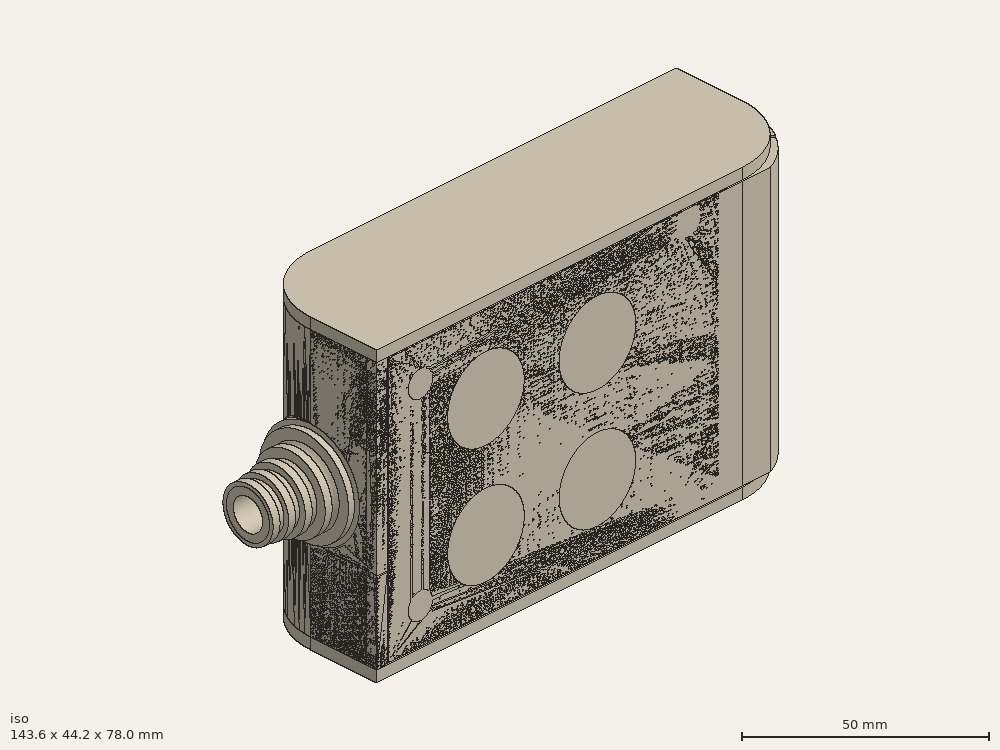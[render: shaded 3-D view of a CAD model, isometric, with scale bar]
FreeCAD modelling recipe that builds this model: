
FCSTD DOCUMENT  (FreeCAD 0.19R0.19.2)
Label: enclosure_157
License: All rights reserved
LicenseURL: http://en.wikipedia.org/wiki/All_rights_reserved
objects: Part::Feature×104, Part::Revolution×104, Part::MultiFuse×91, Sketcher::SketchObject×66, Part::Extrusion×51, Part::Cut×45, Part::Cylinder×42, Part::Fillet×41, Part::Box×27, App::MeasureDistance×4
note: 571 computed .brp shape members not serialized (recipe doc carries the construction recipe); baked Part::Feature solids carry a one-line shape summary decoded from their .brp

FEATURE [Sketcher::SketchObject] Sketch  label="topSketch"
  FullyConstrained = true
  sketch-geometry (20):
    g0: LineSegment StartX=5.21097e-06 StartY=3 StartZ=0 EndX=5.21097e-06 EndY=19 EndZ=0
    g1: ArcOfCircle CenterX=19 CenterY=19 CenterZ=0 NormalX=0 NormalY=0 NormalZ=1 AngleXU=0 Radius=19 StartAngle=1.5708 EndAngle=3.14159
    g2: ArcOfCircle CenterX=19 CenterY=19 CenterZ=0 NormalX=0 NormalY=0 NormalZ=1 AngleXU=0 Radius=16 StartAngle=1.5708 EndAngle=3.14159
    g3: LineSegment StartX=114 StartY=35 StartZ=0 EndX=19 EndY=35 EndZ=0
    g4: LineSegment StartX=5.21097e-06 StartY=3 StartZ=0 EndX=5.21097e-06 EndY=0 EndZ=0
    g5: LineSegment StartX=3 StartY=0 StartZ=0 EndX=5.21097e-06 EndY=0 EndZ=0
    g6: LineSegment StartX=3 StartY=19 StartZ=0 EndX=3 EndY=0 EndZ=0
    g7: LineSegment StartX=19 StartY=38 StartZ=0 EndX=124 EndY=38 EndZ=0
    g8: Circle CenterX=119 CenterY=35 CenterZ=0 NormalX=0 NormalY=0 NormalZ=1 AngleXU=0 Radius=1
    g9: Circle CenterX=121 CenterY=35 CenterZ=0 NormalX=0 NormalY=0 NormalZ=1 AngleXU=0 Radius=1
    g10: Circle CenterX=121 CenterY=33 CenterZ=0 NormalX=0 NormalY=0 NormalZ=1 AngleXU=0 Radius=1
    g11: BSplineCurve PolesCount=3 KnotsCount=2 Degree=2 IsPeriodic=0
    g12: GeomPoint X=119 Y=35 Z=0
    g13: GeomPoint X=121 Y=33 Z=0
    g14: LineSegment StartX=119 StartY=35 StartZ=0 EndX=114 EndY=35 EndZ=0
    g15: ArcOfCircle CenterX=105 CenterY=19 CenterZ=0 NormalX=0 NormalY=0 NormalZ=1 AngleXU=0 Radius=19 StartAngle=5.7297 EndAngle=6.28319
    g16: ArcOfCircle CenterX=105 CenterY=19 CenterZ=0 NormalX=0 NormalY=0 NormalZ=1 AngleXU=0 Radius=16 StartAngle=5.60905 EndAngle=6.28319
    g17: LineSegment StartX=121 StartY=33 StartZ=0 EndX=121 EndY=19 EndZ=0
    g18: LineSegment StartX=124 StartY=38 StartZ=0 EndX=124 EndY=19 EndZ=0
    g19: LineSegment StartX=117.5 StartY=9.01251 StartZ=0 EndX=121.163 EndY=9.0125 EndZ=0
  constraints (46):
    c: Vertical(g0)
    c: Block(g0)
    c: Coincident(g1,g0)
    c: Block(g1)
    c: Coincident(g2,g1)
    c: Block(g2)
    c: Coincident(g3,g2)
    c: Horizontal(g3)
    c: Tangent(g3,g2)
    c: Coincident(g4,g0)
    c: Distance(g4) = 3
    c: Vertical(g4)
    c: Coincident(g5,g4)
    c: Horizontal(g5)
    c: Coincident(g6,g2)
    c: Coincident(g6,g5)
    c: Vertical(g6)
    c: Horizontal(g7)
    c: Distance(g7) = 105
    c: Coincident(g7,g1)
    c: Block(g3)
    c: Weight(g8) = 1
    c: Equal(g8,g9)
    c: Equal(g8,g10)
    c: InternalAlignment(g8,g11)
    c: InternalAlignment(g9,g11)
    c: InternalAlignment(g10,g11)
    c: InternalAlignment(g12,g11)
    c: InternalAlignment(g13,g11)
    c: Block(g11)
    c: Coincident(g14,g11)
    c: Coincident(g14,g3)
    c: Horizontal(g14)
    c: Block(g15)
    c: Coincident(g16,g15)
    c: Block(g16)
    c: Coincident(g17,g11)
    c: Coincident(g17,g16)
    c: Vertical(g17)
    c: Distance(g17) = 14
    c: Coincident(g18,g7)
    c: Coincident(g18,g15)
    c: Vertical(g18)
    c: Distance(g18) = 19
    c: Coincident(g19,g16)
    c: Coincident(g19,g15)
FEATURE [Sketcher::SketchObject] Sketch001  label="bottomSketch"
  FullyConstrained = true
  sketch-geometry (32):
    g0: LineSegment StartX=3.3 StartY=-6.03275e-07 StartZ=0 EndX=98 EndY=-6.03275e-07 EndZ=0
    g1: ArcOfCircle CenterX=98 CenterY=19 CenterZ=0 NormalX=0 NormalY=0 NormalZ=1 AngleXU=0 Radius=19 StartAngle=4.71239 EndAngle=5.71103
    g2: LineSegment StartX=6.3 StartY=8 StartZ=0 EndX=3.3 EndY=8 EndZ=0
    g3: LineSegment StartX=3.3 StartY=8 StartZ=0 EndX=3.3 EndY=-6.03275e-07 EndZ=0
    g4: ArcOfCircle CenterX=8.3 CenterY=5 CenterZ=0 NormalX=0 NormalY=0 NormalZ=1 AngleXU=0 Radius=2 StartAngle=3.14159 EndAngle=4.71239
    g5: LineSegment StartX=6.3 StartY=8 StartZ=0 EndX=6.3 EndY=5 EndZ=0
    g6: ArcOfCircle CenterX=98 CenterY=19 CenterZ=0 NormalX=0 NormalY=0 NormalZ=1 AngleXU=0 Radius=12.7 StartAngle=4.71239 EndAngle=6.28319
    g7: LineSegment StartX=94.7 StartY=3 StartZ=0 EndX=8.3 EndY=3 EndZ=0
    g8-g12: Circle x5 (B-spline internal-alignment scaffolding for g13; pole/knot coordinates omitted)
    g13: BSplineCurve PolesCount=5 KnotsCount=3 Degree=3 IsPeriodic=0
    g14: GeomPoint X=98 Y=6.3 Z=0
    g15: GeomPoint X=96.3938 Y=4.71946 Z=0
    g16: GeomPoint X=94.7 Y=3 Z=0
    g17-g23: Circle x7 (B-spline internal-alignment scaffolding for g24; pole/knot coordinates omitted)
    g24: BSplineCurve PolesCount=7 KnotsCount=5 Degree=3 IsPeriodic=0
    g25-g29: GeomPoint x5 (B-spline internal-alignment scaffolding for g24; pole/knot coordinates omitted)
    g30: ArcOfCircle CenterX=98 CenterY=19 CenterZ=0 NormalX=0 NormalY=0 NormalZ=1 AngleXU=0 Radius=15.7 StartAngle=5.81226 EndAngle=6.28319
    g31: LineSegment StartX=110.7 StartY=19 StartZ=0 EndX=113.7 EndY=19 EndZ=0
  constraints (41):
    c: Horizontal(g0)
    c: Coincident(g1,g0)
    c: Block(g1)
    c: Horizontal(g2)
    c: Distance(g2) = 3
    c: Coincident(g3,g2)
    c: Vertical(g3)
    c: Coincident(g3,g0)
    c: Block(g4)
    c: Block(g2)
    c: Coincident(g5,g2)
    c: Coincident(g5,g4)
    c: Vertical(g5)
    c: Coincident(g6,g1)
    c: Block(g6)
    c: Coincident(g7,g4)
    c: Horizontal(g7)
    c: Block(g0)
    c: Block(g7)
    c: Block(g3)
    c: Coincident(g13,g6)
    c: Weight(g8) = 1
    c: Equal(g8, g9-g12) x4
    c: Coincident(g13,g7)
    c: InternalAlignment(g8-g12 -> g13) x5
    c: InternalAlignment(g14,g13)
    c: InternalAlignment(g15,g13)
    c: InternalAlignment(g16,g13)
    c: Block(g13)
    c: Weight(g17) = 1
    c: Equal(g17, g18-g23) x6
    c: Coincident(g24,g1)
    c: InternalAlignment(g17-g23 -> g24) x7
    c: InternalAlignment(g25-g29 -> g24) x5
    c: Block(g24)
    c: Coincident(g30,g24)
    c: Coincident(g31,g6)
    c: Coincident(g31,g30)
    c: Horizontal(g31)
    c: Block(g31)
    c: Block(g30)
FEATURE [Part::Extrusion] Extrude  label="top"
  Base = -> Sketch
  Dir = (0,0,1)
  DirMode = 2
  FaceMakerClass = Part::FaceMakerBullseye
  LengthFwd = 72
  LengthRev = 0
  Solid = true
  Symmetric = false
FEATURE [Part::Extrusion] Extrude001  label="bottom"
  Base = -> Sketch001
  Dir = (0,0,1)
  DirMode = 2
  FaceMakerClass = Part::FaceMakerBullseye
  LengthFwd = 71.4
  LengthRev = 0
  Placement = pos=(0,0,0.3) rot=(0,0,1;0rad)
  Solid = true
  Symmetric = false
FEATURE [Sketcher::SketchObject] Sketch002  label="topSketch001"
  FullyConstrained = true
  sketch-geometry (6):
    g0: ArcOfCircle CenterX=19 CenterY=19 CenterZ=0 NormalX=0 NormalY=0 NormalZ=1 AngleXU=0 Radius=19 StartAngle=1.5708 EndAngle=3.14159
    g1: LineSegment StartX=5.22862e-06 StartY=19 StartZ=0 EndX=5.22862e-06 EndY=1.19904e-11 EndZ=0
    g2: LineSegment StartX=19 StartY=38 StartZ=0 EndX=124 EndY=38 EndZ=0
    g3: LineSegment StartX=5.22862e-06 StartY=1.19904e-11 StartZ=0 EndX=105 EndY=1.19904e-11 EndZ=0
    g4: ArcOfCircle CenterX=105 CenterY=19 CenterZ=0 NormalX=0 NormalY=0 NormalZ=1 AngleXU=0 Radius=19 StartAngle=4.71239 EndAngle=6.28319
    g5: LineSegment StartX=124 StartY=38 StartZ=0 EndX=124 EndY=19 EndZ=0
  constraints (16):
    c: Block(g0)
    c: Coincident(g1,g0)
    c: Vertical(g1)
    c: Horizontal(g2)
    c: Distance(g2) = 105
    c: Coincident(g2,g0)
    c: Distance(g1) = 19
    c: Coincident(g3,g1)
    c: Horizontal(g3)
    c: Distance(g3) = 105
    c: Block(g4)
    c: Coincident(g4,g3)
    c: Coincident(g5,g2)
    c: Coincident(g5,g4)
    c: Vertical(g5)
    c: Distance(g5) = 19
FEATURE [Part::Extrusion] Extrude002  label="sideA"
  Base = -> Sketch002
  Dir = (0,0,1)
  DirMode = 2
  FaceMakerClass = Part::FaceMakerBullseye
  LengthFwd = 3
  LengthRev = 0
  Placement = pos=(0,0,-3) rot=(0,0,1;0rad)
  Solid = true
  Symmetric = false
FEATURE [Sketcher::SketchObject] Sketch003  label="topSketch002"
  FullyConstrained = true
  sketch-geometry (6):
    g0: LineSegment StartX=19 StartY=38 StartZ=0 EndX=117 EndY=38 EndZ=0
    g1: ArcOfCircle CenterX=19 CenterY=19 CenterZ=0 NormalX=0 NormalY=0 NormalZ=1 AngleXU=0 Radius=19 StartAngle=1.5708 EndAngle=3.14159
    g2: LineSegment StartX=117 StartY=38 StartZ=0 EndX=117 EndY=19 EndZ=0
    g3: LineSegment StartX=98 StartY=1.0161e-12 StartZ=0 EndX=5.22862e-06 EndY=1.0161e-12 EndZ=0
    g4: LineSegment StartX=5.22862e-06 StartY=19 StartZ=0 EndX=5.22862e-06 EndY=1.0161e-12 EndZ=0
    g5: ArcOfCircle CenterX=98 CenterY=19 CenterZ=0 NormalX=0 NormalY=0 NormalZ=1 AngleXU=0 Radius=19 StartAngle=4.71239 EndAngle=6.28319
  constraints (16):
    c: Horizontal(g0)
    c: Distance(g0) = 98
    c: Coincident(g1,g0)
    c: Block(g1)
    c: Coincident(g2,g0)
    c: Vertical(g2)
    c: Distance(g2) = 19
    c: Horizontal(g3)
    c: Coincident(g4,g1)
    c: Vertical(g4)
    c: Coincident(g3,g4)
    c: Block(g3)
    c: Coincident(g5,g2)
    c: Coincident(g5,g3)
    c: Block(g0)
    c: Block(g5)
FEATURE [Sketcher::SketchObject] Sketch004
  FullyConstrained = true
  MapMode = 3
  Placement = pos=(0,0,0) rot=(1,0,0;1.5708rad)
  Support = -> [Extrude]
  sketch-geometry (8):
    g0: Circle CenterX=80.351 CenterY=-67.6202 CenterZ=0 NormalX=0 NormalY=0 NormalZ=1 AngleXU=0 Radius=2
    g1: Circle CenterX=80.351 CenterY=-67.6202 CenterZ=0 NormalX=0 NormalY=0 NormalZ=1 AngleXU=0 Radius=3
    g2: Circle CenterX=80.351 CenterY=-4.92017 CenterZ=0 NormalX=0 NormalY=0 NormalZ=1 AngleXU=0 Radius=2
    g3: Circle CenterX=80.351 CenterY=-4.92017 CenterZ=0 NormalX=0 NormalY=0 NormalZ=1 AngleXU=0 Radius=3
    g4: Circle CenterX=23.851 CenterY=-4.92017 CenterZ=0 NormalX=0 NormalY=0 NormalZ=1 AngleXU=0 Radius=2
    g5: Circle CenterX=23.851 CenterY=-4.92017 CenterZ=0 NormalX=0 NormalY=0 NormalZ=1 AngleXU=0 Radius=3
    g6: Circle CenterX=23.851 CenterY=-67.6202 CenterZ=0 NormalX=0 NormalY=0 NormalZ=1 AngleXU=0 Radius=2
    g7: Circle CenterX=23.851 CenterY=-67.6202 CenterZ=0 NormalX=0 NormalY=0 NormalZ=1 AngleXU=0 Radius=3
  constraints (8):
    c: Block(g3)
    c: Block(g2)
    c: Block(g1)
    c: Block(g0)
    c: Block(g6)
    c: Block(g7)
    c: Block(g4)
    c: Block(g5)
FEATURE [Part::Extrusion] Extrude004
  Base = -> Sketch004
  Dir = (0,-1,2e-16)
  DirMode = 2
  FaceMakerClass = Part::FaceMakerBullseye
  LengthFwd = 6
  LengthRev = 0
  Placement = pos=(0,9,0) rot=(0,0,1;0rad)
  Solid = true
  Symmetric = false
FEATURE [Sketcher::SketchObject] Sketch005
  FullyConstrained = true
  MapMode = 3
  Placement = pos=(0,0,0) rot=(1,0,0;1.5708rad)
  Support = -> [Extrude]
  sketch-geometry (8):
    g0: Circle CenterX=80.351 CenterY=-67.6202 CenterZ=0 NormalX=0 NormalY=0 NormalZ=1 AngleXU=0 Radius=3
    g1: Circle CenterX=80.351 CenterY=-4.92017 CenterZ=0 NormalX=0 NormalY=0 NormalZ=1 AngleXU=0 Radius=3
    g2: Circle CenterX=23.851 CenterY=-4.92017 CenterZ=0 NormalX=0 NormalY=0 NormalZ=1 AngleXU=0 Radius=3
    g3: Circle CenterX=23.851 CenterY=-67.6202 CenterZ=0 NormalX=0 NormalY=0 NormalZ=1 AngleXU=0 Radius=3
    g4: Circle CenterX=23.851 CenterY=-67.6202 CenterZ=0 NormalX=0 NormalY=0 NormalZ=1 AngleXU=0 Radius=5
    g5: Circle CenterX=80.351 CenterY=-67.6202 CenterZ=0 NormalX=0 NormalY=0 NormalZ=1 AngleXU=0 Radius=5
    g6: Circle CenterX=23.851 CenterY=-4.92017 CenterZ=0 NormalX=0 NormalY=0 NormalZ=1 AngleXU=0 Radius=5
    g7: Circle CenterX=80.351 CenterY=-4.92017 CenterZ=0 NormalX=0 NormalY=0 NormalZ=1 AngleXU=0 Radius=5
  constraints (8):
    c: Block(g1)
    c: Block(g0)
    c: Block(g3)
    c: Block(g2)
    c: Block(g5)
    c: Block(g4)
    c: Block(g6)
    c: Block(g7)
FEATURE [Part::Extrusion] Extrude005
  Base = -> Sketch005
  Dir = (0,-1,2e-16)
  DirMode = 2
  FaceMakerClass = Part::FaceMakerBullseye
  LengthFwd = 2
  LengthRev = 0
  Solid = true
  Symmetric = false
FEATURE [Sketcher::SketchObject] Sketch006
  FullyConstrained = true
  MapMode = 3
  Placement = pos=(0,0,0) rot=(1,0,0;1.5708rad)
  sketch-geometry (8):
    g0: Circle CenterX=80.351 CenterY=-67.6202 CenterZ=0 NormalX=0 NormalY=0 NormalZ=1 AngleXU=0 Radius=3
    g1: Circle CenterX=80.351 CenterY=-4.92017 CenterZ=0 NormalX=0 NormalY=0 NormalZ=1 AngleXU=0 Radius=3
    g2: Circle CenterX=23.851 CenterY=-4.92017 CenterZ=0 NormalX=0 NormalY=0 NormalZ=1 AngleXU=0 Radius=3
    g3: Circle CenterX=23.851 CenterY=-67.6202 CenterZ=0 NormalX=0 NormalY=0 NormalZ=1 AngleXU=0 Radius=3
    g4: Circle CenterX=23.851 CenterY=-67.6202 CenterZ=0 NormalX=0 NormalY=0 NormalZ=1 AngleXU=0 Radius=5
    g5: Circle CenterX=80.351 CenterY=-67.6202 CenterZ=0 NormalX=0 NormalY=0 NormalZ=1 AngleXU=0 Radius=5
    g6: Circle CenterX=23.851 CenterY=-4.92017 CenterZ=0 NormalX=0 NormalY=0 NormalZ=1 AngleXU=0 Radius=5
    g7: Circle CenterX=80.351 CenterY=-4.92017 CenterZ=0 NormalX=0 NormalY=0 NormalZ=1 AngleXU=0 Radius=5
  constraints (8):
    c: Block(g1)
    c: Block(g0)
    c: Block(g3)
    c: Block(g2)
    c: Block(g5)
    c: Block(g4)
    c: Block(g6)
    c: Block(g7)
FEATURE [Part::Extrusion] Extrude007
  Base = -> Sketch006
  Dir = (0,-1,2e-16)
  DirMode = 2
  FaceMakerClass = Part::FaceMakerBullseye
  LengthFwd = 2
  LengthRev = 0
  Solid = true
  Symmetric = false
FEATURE [Part::Fillet] Fillet
  Base = -> Extrude007
  Edges = 4 edges r=1.99: [Edge6,Edge12,Edge18,Edge24]
FEATURE [Part::Cut] Cut
  Base = -> Extrude005
  Placement = pos=(0,5,0) rot=(0,0,1;0rad)
  Tool = -> Fillet
FEATURE [Part::MultiFuse] Fusion  label="pCBScrews"
  Placement = pos=(-2.5,0,72.3) rot=(0,0,1;0rad)
  Shapes = -> [Extrude004,Cut]
FEATURE [App::MeasureDistance] Distance  label="Distance: 0.69 mm"
  Distance = 0.685967
  P1 = (24.0138,2.9647,0.3)
  P2 = (23.8901,3,-0.373787)
FEATURE [App::MeasureDistance] Distance001  label="Distance: 0.53 mm"
  Distance = 0.533607
  P1 = (80.2939,3,72.2334)
  P2 = (80.281,2.99661,71.7)
FEATURE [Part::Fillet] Fillet001
  Base = -> Extrude001
  Edges = 1 edges r=2.4: [Edge17]
FEATURE [Part::Fillet] Fillet002  label="bottom001"
  Base = -> Fillet001
  Edges = 1 edges r=2.4: [Edge36]
FEATURE [Part::Fillet] Fillet003  label="top001"
  Base = -> Extrude
  Edges = 1 edges r=2: [Edge1]
FEATURE [Sketcher::SketchObject] Sketch007
  FullyConstrained = true
  sketch-geometry (16):
    g0: LineSegment StartX=4 StartY=0 StartZ=0 EndX=4 EndY=2.4 EndZ=0
    g1: LineSegment StartX=4 StartY=2.4 StartZ=0 EndX=7 EndY=2.4 EndZ=0
    g2: LineSegment StartX=4 StartY=0 StartZ=0 EndX=5.7 EndY=0 EndZ=0
    g3: LineSegment StartX=5.7 StartY=0 StartZ=0 EndX=5.7 EndY=-5.6 EndZ=0
    g4-g8: Circle x5 (B-spline internal-alignment scaffolding for g9; pole/knot coordinates omitted)
    g9: BSplineCurve PolesCount=5 KnotsCount=3 Degree=3 IsPeriodic=0
    g10: GeomPoint X=7 Y=2.4 Z=0
    g11: GeomPoint X=10.4582 Y=-1.55472 Z=0
    g12: GeomPoint X=14 Y=-5.6 Z=0
    g13: LineSegment StartX=14 StartY=-5.6 StartZ=0 EndX=14 EndY=-14.1 EndZ=0
    g14: LineSegment StartX=14 StartY=-14.1 StartZ=0 EndX=6.5 EndY=-14.1 EndZ=0
    g15: LineSegment StartX=5.7 StartY=-5.6 StartZ=0 EndX=6.5 EndY=-14.1 EndZ=0
  constraints (28):
    c: Distance(g0) = 2.4
    c: Vertical(g0)
    c: Block(g0)
    c: Coincident(g1,g0)
    c: Horizontal(g1)
    c: Distance(g1) = 3
    c: Coincident(g2,g0)
    c: Horizontal(g2)
    c: Distance(g2) = 1.7
    c: Coincident(g3,g2)
    c: Vertical(g3)
    c: Distance(g3) = 5.6
    c: Coincident(g9,g1)
    c: Weight(g4) = 1
    c: Equal(g4, g5-g8) x4
    c: InternalAlignment(g4-g8 -> g9) x5
    c: InternalAlignment(g10,g9)
    c: InternalAlignment(g11,g9)
    c: InternalAlignment(g12,g9)
    c: Block(g9)
    c: Coincident(g13,g9)
    c: Vertical(g13)
    c: Distance(g13) = 8.5
    c: Coincident(g14,g13)
    c: Horizontal(g14)
    c: Distance(g14) = 7.5
    c: Coincident(g15,g3)
    c: Coincident(g15,g14)
FEATURE [Part::Feature] Face
  shape: bbox 10 x 16.5 x 2e-07 mm, 1 faces, 0 solids (baked)
FEATURE [Part::Revolution] Revolve  label="plugHousing"
  Angle = 360
  Axis = (0,1,0)
  Base = (0,0,0)
  FaceMakerClass = Part::FaceMakerBullseye
  Placement = pos=(0,0,36.15) rot=(0,0,1;0rad)
  Solid = false
  Source = -> Face
  Symmetric = false
FEATURE [Part::Feature] Face001
  shape: bbox 10 x 16.5 x 2e-07 mm, 1 faces, 0 solids (baked)
FEATURE [Part::Revolution] Revolve001  label="plugHousing001"
  Angle = 360
  Axis = (0,1,0)
  Base = (0,0,0)
  FaceMakerClass = Part::FaceMakerBullseye
  Placement = pos=(0,0,36.15) rot=(0,0,1;0rad)
  Solid = false
  Source = -> Face001
  Symmetric = false
FEATURE [Part::MultiFuse] Fusion001  label="plugHousing002"
  Placement = pos=(0,0,0) rot=(0,0,1;1.5708rad)
  Shapes = -> [Revolve001,Revolve]
FEATURE [Part::Feature] Face002
  shape: bbox 10 x 16.5 x 2e-07 mm, 1 faces, 0 solids (baked)
FEATURE [Part::Revolution] Revolve003  label="plugHousing005"
  Angle = 360
  Axis = (0,1,0)
  Base = (0,0,0)
  FaceMakerClass = Part::FaceMakerBullseye
  Placement = pos=(0,0,36.15) rot=(0,0,1;0rad)
  Solid = false
  Source = -> Face002
  Symmetric = false
FEATURE [Part::Feature] Face003
  shape: bbox 10 x 16.5 x 2e-07 mm, 1 faces, 0 solids (baked)
FEATURE [Part::Revolution] Revolve002  label="plugHousing003"
  Angle = 360
  Axis = (0,1,0)
  Base = (0,0,0)
  FaceMakerClass = Part::FaceMakerBullseye
  Placement = pos=(0,0,36.15) rot=(0,0,1;0rad)
  Solid = false
  Source = -> Face003
  Symmetric = false
FEATURE [Part::MultiFuse] Fusion002  label="plugHousing004"
  Placement = pos=(0,0,0) rot=(0,0,1;1.5708rad)
  Shapes = -> [Revolve002,Revolve003]
FEATURE [Part::MultiFuse] Fusion003  label="plugHousing006"
  Placement = pos=(0,19,0) rot=(0,0,1;3.14159rad)
  Shapes = -> [Fusion002,Fusion001]
FEATURE [Part::Feature] Face004
  shape: bbox 10 x 16.5 x 2e-07 mm, 1 faces, 0 solids (baked)
FEATURE [Part::Revolution] Revolve006  label="plugHousing010"
  Angle = 360
  Axis = (0,1,0)
  Base = (0,0,0)
  FaceMakerClass = Part::FaceMakerBullseye
  Placement = pos=(0,0,36.15) rot=(0,0,1;0rad)
  Solid = false
  Source = -> Face004
  Symmetric = false
FEATURE [Part::Feature] Face005
  shape: bbox 10 x 16.5 x 2e-07 mm, 1 faces, 0 solids (baked)
FEATURE [Part::Revolution] Revolve007  label="plugHousing011"
  Angle = 360
  Axis = (0,1,0)
  Base = (0,0,0)
  FaceMakerClass = Part::FaceMakerBullseye
  Placement = pos=(0,0,36.15) rot=(0,0,1;0rad)
  Solid = false
  Source = -> Face005
  Symmetric = false
FEATURE [Part::Feature] Face006
  shape: bbox 10 x 16.5 x 2e-07 mm, 1 faces, 0 solids (baked)
FEATURE [Part::Revolution] Revolve004  label="plugHousing007"
  Angle = 360
  Axis = (0,1,0)
  Base = (0,0,0)
  FaceMakerClass = Part::FaceMakerBullseye
  Placement = pos=(0,0,36.15) rot=(0,0,1;0rad)
  Solid = false
  Source = -> Face006
  Symmetric = false
FEATURE [Part::MultiFuse] Fusion004  label="plugHousing009"
  Placement = pos=(0,0,0) rot=(0,0,1;1.5708rad)
  Shapes = -> [Revolve004,Revolve007]
FEATURE [Part::Feature] Face007
  shape: bbox 10 x 16.5 x 2e-07 mm, 1 faces, 0 solids (baked)
FEATURE [Part::Revolution] Revolve005  label="plugHousing008"
  Angle = 360
  Axis = (0,1,0)
  Base = (0,0,0)
  FaceMakerClass = Part::FaceMakerBullseye
  Placement = pos=(0,0,36.15) rot=(0,0,1;0rad)
  Solid = false
  Source = -> Face007
  Symmetric = false
FEATURE [Part::MultiFuse] Fusion005  label="plugHousing012"
  Placement = pos=(0,0,0) rot=(0,0,1;1.5708rad)
  Shapes = -> [Revolve006,Revolve005]
FEATURE [Part::MultiFuse] Fusion006  label="plugHousing013"
  Placement = pos=(0,19,0) rot=(0,0,1;3.14159rad)
  Shapes = -> [Fusion005,Fusion004]
FEATURE [Part::MultiFuse] Fusion007  label="plugHousing014"
  Placement = pos=(122.621,0,-0.15) rot=(0,0,1;0rad)
  Shapes = -> [Fusion003,Fusion006]
FEATURE [Part::Cylinder] Cylinder002
  Angle = 360
  AttacherType = Attacher::AttachEngine3D
  Height = 20
  Placement = pos=(0,0,36.15) rot=(0,0,1;0rad)
  Radius = 4
FEATURE [Part::Cylinder] Cylinder003
  Angle = 360
  AttacherType = Attacher::AttachEngine3D
  Height = 10
  Placement = pos=(0,0,36.15) rot=(0,0,1;0rad)
  Radius = 4
FEATURE [Part::MultiFuse] Fusion009  label="removeToCreateHoleForPlugHousing"
  Placement = pos=(70,19,36.15) rot=(0,1,0;1.5708rad)
  Shapes = -> [Cylinder002,Cylinder003]
FEATURE [Part::Cylinder] Cylinder004
  Angle = 360
  AttacherType = Attacher::AttachEngine3D
  Height = 20
  Placement = pos=(0,0,36.15) rot=(0,0,1;0rad)
  Radius = 4
FEATURE [Part::Cylinder] Cylinder005
  Angle = 360
  AttacherType = Attacher::AttachEngine3D
  Height = 10
  Placement = pos=(0,0,36.15) rot=(0,0,1;0rad)
  Radius = 4
FEATURE [Part::MultiFuse] Fusion010  label="removeToCreateHoleForPlugHousing001"
  Placement = pos=(70,19,36.15) rot=(0,1,0;1.5708rad)
  Shapes = -> [Cylinder004,Cylinder005]
FEATURE [Part::Cut] Cut001
  Base = -> Fillet003
  Tool = -> Fusion010
FEATURE [Part::Cut] Cut002  label="Bottom"
  Base = -> Fillet002
  Tool = -> Fusion009
FEATURE [Part::Feature] Face008
  shape: bbox 10 x 16.5 x 2e-07 mm, 1 faces, 0 solids (baked)
FEATURE [Part::Revolution] Revolve011  label="plugHousing021"
  Angle = 360
  Axis = (0,1,0)
  Base = (0,0,0)
  FaceMakerClass = Part::FaceMakerBullseye
  Placement = pos=(0,0,36.15) rot=(0,0,1;0rad)
  Solid = false
  Source = -> Face008
  Symmetric = false
FEATURE [Part::Feature] Face009
  shape: bbox 10 x 16.5 x 2e-07 mm, 1 faces, 0 solids (baked)
FEATURE [Part::Revolution] Revolve012  label="plugHousing022"
  Angle = 360
  Axis = (0,1,0)
  Base = (0,0,0)
  FaceMakerClass = Part::FaceMakerBullseye
  Placement = pos=(0,0,36.15) rot=(0,0,1;0rad)
  Solid = false
  Source = -> Face009
  Symmetric = false
FEATURE [Part::Feature] Face010 .. Face013  x4 (patterned run collapsed; names and placements below)
  shape: bbox 10 x 16.5 x 2e-07 mm, 1 faces, 0 solids (baked)
FEATURE [Part::Revolution] Revolve015  label="plugHousing027"
  Angle = 360
  Axis = (0,1,0)
  Base = (0,0,0)
  FaceMakerClass = Part::FaceMakerBullseye
  Placement = pos=(0,0,36.15) rot=(0,0,1;0rad)
  Solid = false
  Source = -> Face013
  Symmetric = false
FEATURE [Part::Feature] Face014
  shape: bbox 10 x 16.5 x 2e-07 mm, 1 faces, 0 solids (baked)
FEATURE [Part::Feature] Face015
  shape: bbox 10 x 16.5 x 2e-07 mm, 1 faces, 0 solids (baked)
FEATURE [Part::Feature] Face016
  shape: bbox 10 x 16.5 x 2e-07 mm, 1 faces, 0 solids (baked)
FEATURE [Part::Revolution] Revolve019  label="plugHousing033"
  Angle = 360
  Axis = (0,1,0)
  Base = (0,0,0)
  FaceMakerClass = Part::FaceMakerBullseye
  Placement = pos=(0,0,36.15) rot=(0,0,1;0rad)
  Solid = false
  Source = -> Face016
  Symmetric = false
FEATURE [Part::Feature] Face017
  shape: bbox 10 x 16.5 x 2e-07 mm, 1 faces, 0 solids (baked)
FEATURE [Part::Revolution] Revolve020  label="plugHousing034"
  Angle = 360
  Axis = (0,1,0)
  Base = (0,0,0)
  FaceMakerClass = Part::FaceMakerBullseye
  Placement = pos=(0,0,36.15) rot=(0,0,1;0rad)
  Solid = false
  Source = -> Face017
  Symmetric = false
FEATURE [Part::Feature] Face018
  shape: bbox 10 x 16.5 x 2e-07 mm, 1 faces, 0 solids (baked)
FEATURE [Part::Revolution] Revolve016  label="plugHousing030"
  Angle = 360
  Axis = (0,1,0)
  Base = (0,0,0)
  FaceMakerClass = Part::FaceMakerBullseye
  Placement = pos=(0,0,36.15) rot=(0,0,1;0rad)
  Solid = false
  Source = -> Face018
  Symmetric = false
FEATURE [Part::MultiFuse] Fusion020  label="plugHousing038"
  Placement = pos=(0,0,0) rot=(0,0,1;1.5708rad)
  Shapes = -> [Revolve016,Revolve020]
FEATURE [Part::Feature] Face019
  shape: bbox 10 x 16.5 x 2e-07 mm, 1 faces, 0 solids (baked)
FEATURE [Part::Feature] Face020
  shape: bbox 10 x 16.5 x 2e-07 mm, 1 faces, 0 solids (baked)
FEATURE [Part::Revolution] Revolve017  label="plugHousing031"
  Angle = 360
  Axis = (0,1,0)
  Base = (0,0,0)
  FaceMakerClass = Part::FaceMakerBullseye
  Placement = pos=(0,0,36.15) rot=(0,0,1;0rad)
  Solid = false
  Source = -> Face020
  Symmetric = false
FEATURE [Part::MultiFuse] Fusion021  label="plugHousing039"
  Placement = pos=(0,0,0) rot=(0,0,1;1.5708rad)
  Shapes = -> [Revolve019,Revolve017]
FEATURE [Part::MultiFuse] Fusion023  label="plugHousing041"
  Placement = pos=(0,19,0) rot=(0,0,1;3.14159rad)
  Shapes = -> [Fusion021,Fusion020]
FEATURE [Part::Revolution] Revolve022  label="plugHousing043"
  Angle = 360
  Axis = (0,1,0)
  Base = (0,0,0)
  FaceMakerClass = Part::FaceMakerBullseye
  Placement = pos=(0,0,36.15) rot=(0,0,1;0rad)
  Solid = false
  Source = -> Face019
  Symmetric = false
FEATURE [Part::Feature] Face021
  shape: bbox 10 x 16.5 x 2e-07 mm, 1 faces, 0 solids (baked)
FEATURE [Part::Revolution] Revolve023  label="plugHousing044"
  Angle = 360
  Axis = (0,1,0)
  Base = (0,0,0)
  FaceMakerClass = Part::FaceMakerBullseye
  Placement = pos=(0,0,36.15) rot=(0,0,1;0rad)
  Solid = false
  Source = -> Face021
  Symmetric = false
FEATURE [Part::Feature] Face022
  shape: bbox 10 x 16.5 x 2e-07 mm, 1 faces, 0 solids (baked)
FEATURE [Part::Revolution] Revolve018  label="plugHousing032"
  Angle = 360
  Axis = (0,1,0)
  Base = (0,0,0)
  FaceMakerClass = Part::FaceMakerBullseye
  Placement = pos=(0,0,36.15) rot=(0,0,1;0rad)
  Solid = false
  Source = -> Face022
  Symmetric = false
FEATURE [Part::MultiFuse] Fusion022  label="plugHousing040"
  Placement = pos=(0,0,0) rot=(0,0,1;1.5708rad)
  Shapes = -> [Revolve018,Revolve023]
FEATURE [Part::Feature] Face023
  shape: bbox 10 x 16.5 x 2e-07 mm, 1 faces, 0 solids (baked)
FEATURE [Part::Revolution] Revolve021  label="plugHousing035"
  Angle = 360
  Axis = (0,1,0)
  Base = (0,0,0)
  FaceMakerClass = Part::FaceMakerBullseye
  Placement = pos=(0,0,36.15) rot=(0,0,1;0rad)
  Solid = false
  Source = -> Face023
  Symmetric = false
FEATURE [Part::MultiFuse] Fusion018  label="plugHousing036"
  Placement = pos=(0,0,0) rot=(0,0,1;1.5708rad)
  Shapes = -> [Revolve022,Revolve021]
FEATURE [Part::MultiFuse] Fusion019  label="plugHousing037"
  Placement = pos=(0,19,0) rot=(0,0,1;3.14159rad)
  Shapes = -> [Fusion018,Fusion022]
FEATURE [Part::MultiFuse] Fusion024  label="plugHousing042"
  Placement = pos=(122.621,0,-0.15) rot=(0,0,1;0rad)
  Shapes = -> [Fusion023,Fusion019]
FEATURE [Part::Cylinder] Cylinder006
  Angle = 360
  AttacherType = Attacher::AttachEngine3D
  Height = 20
  Placement = pos=(0,0,36.15) rot=(0,0,1;0rad)
  Radius = 14.3
FEATURE [Part::Cylinder] Cylinder007
  Angle = 360
  AttacherType = Attacher::AttachEngine3D
  Height = 10
  Placement = pos=(0,0,36.15) rot=(0,0,1;0rad)
  Radius = 4
FEATURE [Part::MultiFuse] Fusion026  label="removeToCreteHoleForPlugHousing"
  Placement = pos=(70,19,36) rot=(0,1,0;1.5708rad)
  Shapes = -> [Cylinder006,Cylinder007]
FEATURE [Part::Box] Box001  label="Cube001"
  AttacherType = Attacher::AttachEngine3D
  Height = 28
  Length = 3
  Placement = pos=(110.7,19,22) rot=(0,0,1;0rad)
  Width = 15.7
FEATURE [Part::Cut] Cut003  label="top002"
  Base = -> Cut001
  Tool = -> Fusion007
FEATURE [Part::Revolution] Revolve008  label="plugHousing015"
  Angle = 360
  Axis = (0,1,0)
  Base = (0,0,0)
  FaceMakerClass = Part::FaceMakerBullseye
  Placement = pos=(0,0,36.15) rot=(0,0,1;0rad)
  Solid = false
  Source = -> Face010
  Symmetric = false
FEATURE [Part::MultiFuse] Fusion013  label="plugHousing020"
  Placement = pos=(0,0,0) rot=(0,0,1;1.5708rad)
  Shapes = -> [Revolve008,Revolve012]
FEATURE [Part::Cut] Cut004  label="top003"
  Base = -> Cut003
  Placement = pos=(1,0,0) rot=(0,0,1;0rad)
  Tool = -> Fusion026
FEATURE [Part::Cylinder] Cylinder008
  Angle = 360
  AttacherType = Attacher::AttachEngine3D
  Height = 20
  Placement = pos=(0,0,36.15) rot=(0,0,1;0rad)
  Radius = 10.3
FEATURE [Part::Cylinder] Cylinder009
  Angle = 360
  AttacherType = Attacher::AttachEngine3D
  Height = 10
  Placement = pos=(0,0,36.15) rot=(0,0,1;0rad)
  Radius = 4
FEATURE [Part::MultiFuse] Fusion027  label="removeToCreteHoleForPlugHousing001"
  Placement = pos=(70,19,36) rot=(0,1,0;1.5708rad)
  Shapes = -> [Cylinder008,Cylinder009]
FEATURE [Part::Cut] Cut005  label="plugHousingTab"
  Base = -> Box001
  Tool = -> Fusion027
FEATURE [Part::MultiFuse] Fusion028  label="plugHousing045"
  Shapes = -> [Fusion024,Cut005]
FEATURE [Part::Box] Box002  label="Cube002"
  AttacherType = Attacher::AttachEngine3D
  Height = 28.8
  Length = 3
  Placement = pos=(107.3,28,21.6) rot=(0,0,1;0rad)
  Width = 7
FEATURE [Part::Box] Box003  label="Cube003"
  AttacherType = Attacher::AttachEngine3D
  Height = 3
  Length = 6.4
  Placement = pos=(107.3,28,18.6) rot=(0,0,1;0rad)
  Width = 7
FEATURE [Part::Box] Box004  label="Cube004"
  AttacherType = Attacher::AttachEngine3D
  Height = 3
  Length = 6.4
  Placement = pos=(107.3,28,50.4) rot=(0,0,1;0rad)
  Width = 7
FEATURE [Part::MultiFuse] Fusion029  label="plugHousingBracketHolder"
  Shapes = -> [Box004,Box002,Box003]
FEATURE [Part::Cylinder] Cylinder010
  Angle = 360
  AttacherType = Attacher::AttachEngine3D
  Height = 20
  Placement = pos=(0,0,36.15) rot=(0,0,1;0rad)
  Radius = 14.3
FEATURE [Part::Cylinder] Cylinder011
  Angle = 360
  AttacherType = Attacher::AttachEngine3D
  Height = 10
  Placement = pos=(0,0,36.15) rot=(0,0,1;0rad)
  Radius = 4
FEATURE [Part::MultiFuse] Fusion030  label="removeToCreteHoleForPlugHousing002"
  Placement = pos=(70,19,36) rot=(0,1,0;1.5708rad)
  Shapes = -> [Cylinder010,Cylinder011]
FEATURE [Part::Cut] Cut006  label="plugHousingBracketHolder001"
  Base = -> Fusion029
  Tool = -> Fusion030
FEATURE [Part::Cylinder] Cylinder012
  Angle = 360
  AttacherType = Attacher::AttachEngine3D
  Height = 20
  Placement = pos=(0,0,36.15) rot=(0,0,1;0rad)
  Radius = 7
FEATURE [Part::Cylinder] Cylinder013
  Angle = 360
  AttacherType = Attacher::AttachEngine3D
  Height = 10
  Placement = pos=(0,0,36.15) rot=(0,0,1;0rad)
  Radius = 4
FEATURE [Part::MultiFuse] Fusion032  label="removeToCreteHoleForPlugHousing003"
  Placement = pos=(70,19,36) rot=(0,1,0;1.5708rad)
  Shapes = -> [Cylinder012,Cylinder013]
FEATURE [Part::Cut] Cut007  label="bottom002"
  Base = -> Cut002
  Tool = -> Fusion032
FEATURE [Sketcher::SketchObject] Sketch008
  FullyConstrained = true
  sketch-geometry (54):
    g0: LineSegment StartX=-4.2 StartY=0 StartZ=0 EndX=-6.2 EndY=0 EndZ=0
    g1: LineSegment StartX=-14 StartY=-18 StartZ=0 EndX=-14 EndY=-26.5 EndZ=0
    g2: LineSegment StartX=-4.2 StartY=0 StartZ=0 EndX=-4.2 EndY=-13.4877 EndZ=0
    g3: Circle CenterX=-4.2 CenterY=-13.4877 CenterZ=0 NormalX=0 NormalY=0 NormalZ=1 AngleXU=0 Radius=1
    g4: Circle CenterX=-4.2 CenterY=-26.5 CenterZ=0 NormalX=0 NormalY=0 NormalZ=1 AngleXU=0 Radius=1
    g5: Circle CenterX=-8.2 CenterY=-26.5 CenterZ=0 NormalX=0 NormalY=0 NormalZ=1 AngleXU=0 Radius=1
    g6: BSplineCurve PolesCount=3 KnotsCount=2 Degree=2 IsPeriodic=0
    g7: GeomPoint X=-4.2 Y=-13.4877 Z=0
    g8: GeomPoint X=-8.2 Y=-26.5 Z=0
    g9: LineSegment StartX=-14 StartY=-26.5 StartZ=0 EndX=-8.2 EndY=-26.5 EndZ=0
    g10: LineSegment StartX=-10.15 StartY=-12 StartZ=0 EndX=-10.15 EndY=-14 EndZ=0
    g11: LineSegment StartX=-12.8401 StartY=-16 StartZ=0 EndX=-10.1571 EndY=-16 EndZ=0
    g12: LineSegment StartX=-10.15 StartY=-14 StartZ=0 EndX=-8.70761 EndY=-14 EndZ=0
    g13: LineSegment StartX=-12.8401 StartY=-16 StartZ=0 EndX=-12.8401 EndY=-17.6958 EndZ=0
    g14: LineSegment StartX=-10.15 StartY=-12 StartZ=0 EndX=-7.79258 EndY=-12 EndZ=0
    g15: Circle CenterX=-6.2215 CenterY=-2 CenterZ=0 NormalX=0 NormalY=0 NormalZ=1 AngleXU=0 Radius=1
    g16: Circle CenterX=-6.22762 CenterY=-2.58724 CenterZ=0 NormalX=0 NormalY=0 NormalZ=1 AngleXU=0 Radius=1
    g17: Circle CenterX=-6.32538 CenterY=-4 CenterZ=0 NormalX=0 NormalY=0 NormalZ=1 AngleXU=0 Radius=1
    g18: BSplineCurve PolesCount=3 KnotsCount=2 Degree=2 IsPeriodic=0
    g19: GeomPoint X=-6.2215 Y=-2 Z=0
    g20: GeomPoint X=-6.32538 Y=-4 Z=0
    g21: Circle CenterX=-6.48644 CenterY=-5.99526 CenterZ=0 NormalX=0 NormalY=0 NormalZ=1 AngleXU=0 Radius=1
    g22: Circle CenterX=-6.58486 CenterY=-6.99526 CenterZ=0 NormalX=0 NormalY=0 NormalZ=1 AngleXU=0 Radius=1
    g23: Circle CenterX=-6.77343 CenterY=-8 CenterZ=0 NormalX=0 NormalY=0 NormalZ=1 AngleXU=0 Radius=1
    g24: BSplineCurve PolesCount=3 KnotsCount=2 Degree=2 IsPeriodic=0
    g25: GeomPoint X=-6.48644 Y=-5.99526 Z=0
    g26: GeomPoint X=-6.77343 Y=-8 Z=0
    g27: Circle CenterX=-7.19003 CenterY=-10 CenterZ=0 NormalX=0 NormalY=0 NormalZ=1 AngleXU=0 Radius=1
    g28: Circle CenterX=-7.44407 CenterY=-11.0915 CenterZ=0 NormalX=0 NormalY=0 NormalZ=1 AngleXU=0 Radius=1
    g29: Circle CenterX=-7.79258 CenterY=-12 CenterZ=0 NormalX=0 NormalY=0 NormalZ=1 AngleXU=0 Radius=1
    g30: BSplineCurve PolesCount=3 KnotsCount=2 Degree=2 IsPeriodic=0
    g31: GeomPoint X=-7.19003 Y=-10 Z=0
    g32: GeomPoint X=-7.79258 Y=-12 Z=0
    g33: Circle CenterX=-8.70761 CenterY=-14 CenterZ=0 NormalX=0 NormalY=0 NormalZ=1 AngleXU=0 Radius=1
    g34: Circle CenterX=-9.33087 CenterY=-15.1837 CenterZ=0 NormalX=0 NormalY=0 NormalZ=1 AngleXU=0 Radius=1
    g35: Circle CenterX=-10.1571 CenterY=-16 CenterZ=0 NormalX=0 NormalY=0 NormalZ=1 AngleXU=0 Radius=1
    g36: BSplineCurve PolesCount=3 KnotsCount=2 Degree=2 IsPeriodic=0
    g37: GeomPoint X=-8.70761 Y=-14 Z=0
    g38: GeomPoint X=-10.1571 Y=-16 Z=0
    g39: Circle CenterX=-12.8401 CenterY=-17.6958 CenterZ=0 NormalX=0 NormalY=0 NormalZ=1 AngleXU=0 Radius=1
    g40: Circle CenterX=-13.3521 CenterY=-17.9027 CenterZ=0 NormalX=0 NormalY=0 NormalZ=1 AngleXU=0 Radius=1
    g41: Circle CenterX=-14 CenterY=-18 CenterZ=0 NormalX=0 NormalY=0 NormalZ=1 AngleXU=0 Radius=1
    g42: BSplineCurve PolesCount=3 KnotsCount=2 Degree=2 IsPeriodic=0
    g43: GeomPoint X=-12.8401 Y=-17.6958 Z=0
    g44: GeomPoint X=-14 Y=-18 Z=0
    g45: LineSegment StartX=-6.2 StartY=0 StartZ=0 EndX=-7.2 EndY=0 EndZ=0
    g46: LineSegment StartX=-7.2 StartY=0 StartZ=0 EndX=-7.2 EndY=-2 EndZ=0
    g47: LineSegment StartX=-7.2 StartY=-2 StartZ=0 EndX=-6.2215 EndY=-2 EndZ=0
    g48: LineSegment StartX=-6.32538 StartY=-4 StartZ=0 EndX=-7.65538 EndY=-4 EndZ=0
    g49: LineSegment StartX=-7.65538 StartY=-4 StartZ=0 EndX=-7.65538 EndY=-5.99526 EndZ=0
    g50: LineSegment StartX=-7.65538 StartY=-5.99526 StartZ=0 EndX=-6.48644 EndY=-5.99526 EndZ=0
    g51: LineSegment StartX=-6.77343 StartY=-8 StartZ=0 EndX=-8.43343 EndY=-8 EndZ=0
    g52: LineSegment StartX=-8.43343 StartY=-8 StartZ=0 EndX=-8.43343 EndY=-10 EndZ=0
    g53: LineSegment StartX=-8.43343 StartY=-10 StartZ=0 EndX=-7.19003 EndY=-10 EndZ=0
  constraints (112):
    c: Horizontal(g0)
    c: Distance(g0) = 2
    c: Block(g0)
    c: Vertical(g1)
    c: Coincident(g2,g0)
    c: Vertical(g2)
    c: Block(g2)
    c: Coincident(g6,g2)
    c: Weight(g3) = 1
    c: Equal(g3,g4)
    c: Equal(g3,g5)
    c: InternalAlignment(g3,g6)
    c: InternalAlignment(g4,g6)
    c: InternalAlignment(g5,g6)
    c: InternalAlignment(g7,g6)
    c: InternalAlignment(g8,g6)
    c: Block(g6)
    c: Coincident(g9,g1)
    c: Coincident(g9,g6)
    c: Horizontal(g9)
    c: Vertical(g10)
    c: Block(g10)
    c: Horizontal(g11)
    c: Block(g11)
    c: Coincident(g12,g10)
    c: Horizontal(g12)
    c: Block(g12)
    c: Coincident(g13,g11)
    c: Vertical(g13)
    c: Block(g13)
    c: Coincident(g14,g10)
    c: Horizontal(g14)
    c: Block(g14)
    c: Block(g9)
    c: Block(g1)
    c: Weight(g15) = 1
    c: Equal(g15,g16)
    c: Equal(g15,g17)
    c: InternalAlignment(g15,g18)
    c: InternalAlignment(g16,g18)
    c: InternalAlignment(g17,g18)
    c: InternalAlignment(g19,g18)
    c: InternalAlignment(g20,g18)
    c: Weight(g21) = 1
    c: Equal(g21,g22)
    c: Equal(g21,g23)
    c: InternalAlignment(g21,g24)
    c: InternalAlignment(g22,g24)
    c: InternalAlignment(g23,g24)
    c: InternalAlignment(g25,g24)
    c: InternalAlignment(g26,g24)
    c: Weight(g27) = 1
    c: Equal(g27,g28)
    c: Equal(g27,g29)
    c: Coincident(g30,g14)
    c: InternalAlignment(g27,g30)
    c: InternalAlignment(g28,g30)
    c: InternalAlignment(g29,g30)
    c: InternalAlignment(g31,g30)
    c: InternalAlignment(g32,g30)
    c: Coincident(g36,g12)
    c: Weight(g33) = 1
    c: Equal(g33,g34)
    c: Equal(g33,g35)
    c: Coincident(g36,g11)
    c: InternalAlignment(g33,g36)
    c: InternalAlignment(g34,g36)
    c: InternalAlignment(g35,g36)
    c: InternalAlignment(g37,g36)
    c: InternalAlignment(g38,g36)
    c: Coincident(g42,g13)
    c: Weight(g39) = 1
    c: Equal(g39,g40)
    c: Equal(g39,g41)
    c: Coincident(g42,g1)
    c: InternalAlignment(g39,g42)
    c: InternalAlignment(g40,g42)
    c: InternalAlignment(g41,g42)
    c: InternalAlignment(g43,g42)
    c: InternalAlignment(g44,g42)
    c: Block(g18)
    c: Block(g24)
    c: Block(g30)
    c: Block(g36)
    c: Block(g42)
    c: Horizontal(g45)
    c: Coincident(g45,g0)
    c: Vertical(g46)
    c: Coincident(g46,g45)
    c: Coincident(g47,g46)
    c: Coincident(g47,g18)
    c: Horizontal(g47)
    c: Block(g46)
    c: Coincident(g48,g18)
    c: Horizontal(g48)
    c: Distance(g48) = 1.33
    c: Vertical(g49)
    c: Coincident(g49,g48)
    c: Coincident(g50,g49)
    c: Coincident(g50,g24)
    c: Horizontal(g50)
    c: Tangent(g50,g22)
    c: Horizontal(g51)
    c: Coincident(g51,g24)
    c: Block(g51)
    c: Vertical(g52)
    c: Block(g52)
    c: Coincident(g52,g51)
    c: Coincident(g53,g52)
    c: Coincident(g53,g30)
    c: Horizontal(g53)
    c: Distance(g1) = 8.5
FEATURE [Part::Feature] Face024
  shape: bbox 9.8 x 26.5 x 2e-07 mm, 1 faces, 0 solids (baked)
FEATURE [Part::Revolution] Revolve024
  Angle = 360
  Axis = (0,1,0)
  Base = (0,0,0)
  FaceMakerClass = Part::FaceMakerBullseye
  Placement = pos=(0,0,0) rot=(0,0,1;1.5708rad)
  Solid = false
  Source = -> Face024
  Symmetric = false
FEATURE [Part::Feature] Face025
  shape: bbox 9.8 x 26.5 x 2e-07 mm, 1 faces, 0 solids (baked)
FEATURE [Part::Revolution] Revolve025
  Angle = 360
  Axis = (0,1,0)
  Base = (0,0,0)
  FaceMakerClass = Part::FaceMakerBullseye
  Placement = pos=(0,0,0) rot=(0,0,1;1.5708rad)
  Solid = false
  Source = -> Face025
  Symmetric = false
FEATURE [Part::MultiFuse] Fusion033
  Placement = pos=(-18,19,36) rot=(0,0,1;0rad)
  Shapes = -> [Revolve025,Revolve024]
FEATURE [Part::Cylinder] Cylinder014
  Angle = 360
  AttacherType = Attacher::AttachEngine3D
  Height = 20
  Placement = pos=(0,0,36.15) rot=(0,0,1;0rad)
  Radius = 14.3
FEATURE [Part::Cylinder] Cylinder015
  Angle = 360
  AttacherType = Attacher::AttachEngine3D
  Height = 10
  Placement = pos=(0,0,36.15) rot=(0,0,1;0rad)
  Radius = 4
FEATURE [Part::MultiFuse] Fusion034  label="removeToCreteHoleForPlugHousing004"
  Placement = pos=(-42,19,36) rot=(0,1,0;1.5708rad)
  Shapes = -> [Cylinder014,Cylinder015]
FEATURE [Part::Cut] Cut008  label="top004"
  Base = -> Cut004
  Placement = pos=(-1,0,0) rot=(0,0,1;0rad)
  Tool = -> Fusion034
FEATURE [Part::Box] Box005  label="Cube005"
  AttacherType = Attacher::AttachEngine3D
  Height = 28
  Length = 3
  Placement = pos=(110.7,19,22) rot=(0,0,1;0rad)
  Width = 15.7
FEATURE [Part::Cylinder] Cylinder016
  Angle = 360
  AttacherType = Attacher::AttachEngine3D
  Height = 10
  Placement = pos=(0,0,36.15) rot=(0,0,1;0rad)
  Radius = 4
FEATURE [Part::Cylinder] Cylinder017
  Angle = 360
  AttacherType = Attacher::AttachEngine3D
  Height = 20
  Placement = pos=(0,0,36.15) rot=(0,0,1;0rad)
  Radius = 10.3
FEATURE [Part::MultiFuse] Fusion035  label="removeToCreteHoleForPlugHousing005"
  Placement = pos=(70,19,36) rot=(0,1,0;1.5708rad)
  Shapes = -> [Cylinder017,Cylinder016]
FEATURE [Part::Cut] Cut009  label="plugHousingTab001"
  Base = -> Box005
  Placement = pos=(-107.4,-14,0) rot=(0,0,1;0rad)
  Tool = -> Fusion035
FEATURE [Part::Box] Box006  label="Cube006"
  AttacherType = Attacher::AttachEngine3D
  Height = 28
  Length = 3
  Placement = pos=(110.7,19,22) rot=(0,0,1;0rad)
  Width = 15.7
FEATURE [Part::Cylinder] Cylinder018
  Angle = 360
  AttacherType = Attacher::AttachEngine3D
  Height = 10
  Placement = pos=(0,0,36.15) rot=(0,0,1;0rad)
  Radius = 4
FEATURE [Part::Cylinder] Cylinder019
  Angle = 360
  AttacherType = Attacher::AttachEngine3D
  Height = 20
  Placement = pos=(0,0,36.15) rot=(0,0,1;0rad)
  Radius = 10.3
FEATURE [Part::MultiFuse] Fusion036  label="removeToCreteHoleForPlugHousing006"
  Placement = pos=(70,19,36) rot=(0,1,0;1.5708rad)
  Shapes = -> [Cylinder019,Cylinder018]
FEATURE [Part::Cut] Cut010  label="plugHousingTab002"
  Base = -> Box006
  Placement = pos=(-107.4,-14,0) rot=(0,0,1;0rad)
  Tool = -> Fusion036
FEATURE [Part::MultiFuse] Fusion037
  Placement = pos=(9.6,23,0) rot=(0,0,1;3.14159rad)
  Shapes = -> [Cut009,Cut010]
FEATURE [Part::Box] Box  label="Cube"
  AttacherType = Attacher::AttachEngine3D
  Height = 10
  Length = 3
  Placement = pos=(3.3,4,12) rot=(0,0,1;0rad)
  Width = 10
FEATURE [Part::Fillet] Fillet004
  Base = -> Fusion028
  Edges = 1 edges r=2: [Edge25]
FEATURE [Part::Fillet] Fillet005  label="plugHousing046"
  Base = -> Fillet004
  Edges = 1 edges r=2: [Edge8]
FEATURE [Part::Fillet] Fillet006
  Base = -> Box
  Edges = 1 edges r=2: [Edge11]
FEATURE [Part::Box] Box007  label="Cube007"
  AttacherType = Attacher::AttachEngine3D
  Height = 10
  Length = 3
  Placement = pos=(3.3,4,50) rot=(0,0,1;0rad)
  Width = 10
FEATURE [Part::Fillet] Fillet007
  Base = -> Box007
  Edges = 1 edges r=2: [Edge12]
FEATURE [Part::Box] Box008  label="Cube008"
  AttacherType = Attacher::AttachEngine3D
  Height = 28
  Length = 4
  Placement = pos=(5,0,22) rot=(0,0,1;0rad)
  Width = 10
FEATURE [Part::Fillet] Fillet008
  Base = -> Box008
  Edges = 1 edges r=1: [Edge7]
FEATURE [Part::Fillet] Fillet009
  Base = -> Fillet008
  Edges = 1 edges r=2: [Edge5]
FEATURE [Part::Fillet] Fillet010
  Base = -> Fillet009
  Edges = 1 edges r=2: [Edge2]
FEATURE [Sketcher::SketchObject] Sketch009  label="topSketch003"
  FullyConstrained = true
  sketch-geometry (4):
    g0: LineSegment StartX=16.8446 StartY=31.512 StartZ=0 EndX=16.3251 EndY=34.4666 EndZ=0
    g1: ArcOfCircle CenterX=19 CenterY=19.2524 CenterZ=0 NormalX=0 NormalY=0 NormalZ=1 AngleXU=0 Radius=15.4476 StartAngle=1.74483 EndAngle=2.72717
    g2: ArcOfCircle CenterX=19 CenterY=19.2524 CenterZ=0 NormalX=0 NormalY=0 NormalZ=1 AngleXU=0 Radius=12.4476 StartAngle=1.74483 EndAngle=2.73189
    g3: LineSegment StartX=4.86004 StartY=25.4725 StartZ=0 EndX=7.58253 EndY=24.2107 EndZ=0
  constraints (7):
    c: Block(g0)
    c: Coincident(g1,g0)
    c: Coincident(g2,g0)
    c: Coincident(g3,g1)
    c: Coincident(g3,g2)
    c: Block(g1)
    c: Block(g2)
FEATURE [Part::Extrusion] Extrude008
  Base = -> Sketch009
  Dir = (0,0,1)
  DirMode = 2
  FaceMakerClass = Part::FaceMakerBullseye
  LengthFwd = 10
  LengthRev = 0
  Placement = pos=(0,0,31) rot=(0,0,1;0rad)
  Solid = true
  Symmetric = false
FEATURE [Part::Cylinder] Cylinder020
  Angle = 360
  AttacherType = Attacher::AttachEngine3D
  Height = 20
  Placement = pos=(0,0,36.15) rot=(0,0,1;0rad)
  Radius = 8.2
FEATURE [Part::Cylinder] Cylinder021
  Angle = 360
  AttacherType = Attacher::AttachEngine3D
  Height = 10
  Placement = pos=(0,0,36.15) rot=(0,0,1;0rad)
  Radius = 4
FEATURE [Part::MultiFuse] Fusion038  label="removeToCreteHoleForPlugHousing007"
  Placement = pos=(-42,19,36) rot=(0,1,0;1.5708rad)
  Shapes = -> [Cylinder020,Cylinder021]
FEATURE [Part::Cut] Cut011
  Base = -> Extrude008
  Tool = -> Fusion038
FEATURE [Part::Fillet] Fillet011
  Base = -> Cut011
  Edges = 1 edges r=2: [Edge1]
FEATURE [Part::Fillet] Fillet012
  Base = -> Fillet011
  Edges = 1 edges r=2.5: [Edge1]
FEATURE [Part::Fillet] Fillet013
  Base = -> Fillet012
  Edges = 1 edges r=2.5: [Edge2]
FEATURE [Part::Box] Box010  label="Cube010"
  AttacherType = Attacher::AttachEngine3D
  Height = 16
  Length = 8
  Placement = pos=(12.7,31.52,28) rot=(0,0,1;0rad)
  Width = 4
FEATURE [Sketcher::SketchObject] Sketch010  label="topSketch004"
  FullyConstrained = true
  sketch-geometry (4):
    g0: LineSegment StartX=16.8446 StartY=31.512 StartZ=0 EndX=16.3251 EndY=34.4666 EndZ=0
    g1: ArcOfCircle CenterX=19 CenterY=19.2524 CenterZ=0 NormalX=0 NormalY=0 NormalZ=1 AngleXU=0 Radius=15.4476 StartAngle=1.74483 EndAngle=2.72717
    g2: ArcOfCircle CenterX=19 CenterY=19.2524 CenterZ=0 NormalX=0 NormalY=0 NormalZ=1 AngleXU=0 Radius=12.4476 StartAngle=1.74483 EndAngle=2.73189
    g3: LineSegment StartX=4.86004 StartY=25.4725 StartZ=0 EndX=7.58253 EndY=24.2107 EndZ=0
  constraints (7):
    c: Block(g0)
    c: Coincident(g1,g0)
    c: Coincident(g2,g0)
    c: Coincident(g3,g1)
    c: Coincident(g3,g2)
    c: Block(g1)
    c: Block(g2)
FEATURE [Part::Cylinder] Cylinder022
  Angle = 360
  AttacherType = Attacher::AttachEngine3D
  Height = 10
  Placement = pos=(0,0,36.15) rot=(0,0,1;0rad)
  Radius = 4
FEATURE [Sketcher::SketchObject] Sketch011  label="topSketch005"
  FullyConstrained = true
  sketch-geometry (4):
    g0: LineSegment StartX=16.8446 StartY=31.512 StartZ=0 EndX=16.3251 EndY=34.4666 EndZ=0
    g1: ArcOfCircle CenterX=19 CenterY=19.2524 CenterZ=0 NormalX=0 NormalY=0 NormalZ=1 AngleXU=0 Radius=15.4476 StartAngle=1.74483 EndAngle=2.72717
    g2: ArcOfCircle CenterX=19 CenterY=19.2524 CenterZ=0 NormalX=0 NormalY=0 NormalZ=1 AngleXU=0 Radius=12.4476 StartAngle=1.74483 EndAngle=2.73189
    g3: LineSegment StartX=4.86004 StartY=25.4725 StartZ=0 EndX=7.58253 EndY=24.2107 EndZ=0
  constraints (7):
    c: Block(g0)
    c: Coincident(g1,g0)
    c: Coincident(g2,g0)
    c: Coincident(g3,g1)
    c: Coincident(g3,g2)
    c: Block(g1)
    c: Block(g2)
FEATURE [Part::Extrusion] Extrude010
  Base = -> Sketch011
  Dir = (0,0,1)
  DirMode = 2
  FaceMakerClass = Part::FaceMakerBullseye
  LengthFwd = 10.6
  LengthRev = 0
  Placement = pos=(0,0,31) rot=(0,0,1;0rad)
  Solid = true
  Symmetric = false
FEATURE [Part::Cylinder] Cylinder023
  Angle = 360
  AttacherType = Attacher::AttachEngine3D
  Height = 20
  Placement = pos=(0,0,36.15) rot=(0,0,1;0rad)
  Radius = 8.2
FEATURE [Part::MultiFuse] Fusion039  label="removeToCreteHoleForPlugHousing008"
  Placement = pos=(-42,19,36) rot=(0,1,0;1.5708rad)
  Shapes = -> [Cylinder023,Cylinder022]
FEATURE [Part::Cut] Cut012
  Base = -> Extrude010
  Placement = pos=(0,0,-0.3) rot=(0,0,1;0rad)
  Tool = -> Fusion039
FEATURE [Part::Cut] Cut013
  Base = -> Box010
  Tool = -> Cut012
FEATURE [Part::Fillet] Fillet014
  Base = -> Cut013
  Edges = 1 edges r=0.7: [Edge13]
FEATURE [Part::Fillet] Fillet015
  Base = -> Fillet014
  Edges = 1 edges r=0.7: [Edge13]
FEATURE [Part::Fillet] Fillet016
  Base = -> Fillet015
  Edges = 1 edges r=0.7: [Edge16]
FEATURE [Part::Fillet] Fillet017
  Base = -> Fillet016
  Edges = 1 edges r=0.7: [Edge11]
FEATURE [Part::Fillet] Fillet018
  Base = -> Fillet017
  Edges = 1 edges r=0.7: [Edge10]
FEATURE [Part::Fillet] Fillet019
  Base = -> Fillet018
  Edges = 1 edges r=1.2: [Edge5]
FEATURE [Part::Fillet] Fillet020
  Base = -> Fillet019
  Edges = 1 edges r=1.2: [Edge12]
FEATURE [Part::Fillet] Fillet021
  Base = -> Fillet020
  Edges = 1 edges r=2: [Edge1]
  Placement = pos=(0.3,0,0) rot=(0,0,1;0rad)
FEATURE [Part::MultiFuse] Fusion040  label="top005"
  Shapes = -> [Cut008,Fillet021]
FEATURE [Part::MultiFuse] Fusion041  label="wireHolder"
  Shapes = -> [Fusion033,Fillet013]
FEATURE [Part::MultiFuse] Fusion042
  Shapes = -> [Fillet007,Fusion041]
FEATURE [Part::MultiFuse] Fusion043  label="wireHolder001"
  Shapes = -> [Fusion042,Fillet010]
FEATURE [Part::MultiFuse] Fusion044  label="wireHolder002"
  Shapes = -> [Fillet006,Fusion037,Fusion043]
FEATURE [Part::Feature] Face026
  shape: bbox 11 x 6 x 2e-07 mm, 1 faces, 0 solids (baked)
FEATURE [Part::Revolution] Revolve026
  Angle = 360
  Axis = (0,1,0)
  Base = (0,0,0)
  FaceMakerClass = Part::FaceMakerBullseye
  Placement = pos=(30.3,-1,19.7) rot=(0,0,1;0rad)
  Solid = false
  Source = -> Face026
  Symmetric = false
FEATURE [Sketcher::SketchObject] Sketch013  label="topSketch006"
  FullyConstrained = true
  sketch-geometry (13):
    g0: LineSegment StartX=117 StartY=19 StartZ=0 EndX=117 EndY=38 EndZ=0
    g1: ArcOfCircle CenterX=98 CenterY=19 CenterZ=0 NormalX=0 NormalY=0 NormalZ=1 AngleXU=0 Radius=19 StartAngle=5.7297 EndAngle=6.28319
    g2: LineSegment StartX=0 StartY=3 StartZ=0 EndX=0 EndY=19 EndZ=0
    g3: LineSegment StartX=19 StartY=38 StartZ=0 EndX=117 EndY=38 EndZ=0
    g4: ArcOfCircle CenterX=19 CenterY=19 CenterZ=0 NormalX=0 NormalY=0 NormalZ=1 AngleXU=0 Radius=19 StartAngle=1.5708 EndAngle=3.14159
    g5: ArcOfCircle CenterX=19 CenterY=19 CenterZ=0 NormalX=0 NormalY=0 NormalZ=1 AngleXU=0 Radius=16 StartAngle=1.5708 EndAngle=3.14159
    g6: ArcOfCircle CenterX=98 CenterY=19 CenterZ=0 NormalX=0 NormalY=0 NormalZ=1 AngleXU=0 Radius=16 StartAngle=5.60905 EndAngle=6.28319
    g7: LineSegment StartX=114 StartY=19 StartZ=0 EndX=114 EndY=35 EndZ=0
    g8: LineSegment StartX=110.5 StartY=9.01251 StartZ=0 EndX=114.163 EndY=9.01251 EndZ=0
    g9: LineSegment StartX=114 StartY=35 StartZ=0 EndX=19 EndY=35 EndZ=0
    g10: LineSegment StartX=0 StartY=3 StartZ=0 EndX=0 EndY=0 EndZ=0
    g11: LineSegment StartX=3 StartY=0 StartZ=0 EndX=0 EndY=0 EndZ=0
    g12: LineSegment StartX=3 StartY=19 StartZ=0 EndX=3 EndY=0 EndZ=0
  constraints (33):
    c: Vertical(g0)
    c: Distance(g0) = 19
    c: Block(g0)
    c: Coincident(g1,g0)
    c: Block(g1)
    c: Vertical(g2)
    c: Block(g2)
    c: Coincident(g3,g0)
    c: Horizontal(g3)
    c: Distance(g3) = 98
    c: Coincident(g4,g3)
    c: Coincident(g4,g2)
    c: Block(g4)
    c: Coincident(g5,g4)
    c: Coincident(g6,g1)
    c: Block(g6)
    c: Block(g5)
    c: Coincident(g7,g6)
    c: Vertical(g7)
    c: Coincident(g8,g6)
    c: Coincident(g8,g1)
    c: Coincident(g9,g7)
    c: Coincident(g9,g5)
    c: Horizontal(g9)
    c: Tangent(g9,g5)
    c: Coincident(g10,g2)
    c: Distance(g10) = 3
    c: Vertical(g10)
    c: Coincident(g11,g10)
    c: Horizontal(g11)
    c: Coincident(g12,g5)
    c: Coincident(g12,g11)
    c: Vertical(g12)
FEATURE [Part::Extrusion] Extrude011  label="top006"
  Base = -> Sketch013
  Dir = (0,0,1)
  DirMode = 2
  FaceMakerClass = Part::FaceMakerBullseye
  LengthFwd = 72
  LengthRev = 0
  Solid = true
  Symmetric = false
FEATURE [Sketcher::SketchObject] Sketch014
  FullyConstrained = true
  MapMode = 3
  Placement = pos=(0,0,0) rot=(1,0,0;1.5708rad)
  Support = -> [Extrude011]
  sketch-geometry (8):
    g0: Circle CenterX=80.351 CenterY=-67.6202 CenterZ=0 NormalX=0 NormalY=0 NormalZ=1 AngleXU=0 Radius=2
    g1: Circle CenterX=80.351 CenterY=-67.6202 CenterZ=0 NormalX=0 NormalY=0 NormalZ=1 AngleXU=0 Radius=3
    g2: Circle CenterX=80.351 CenterY=-4.92017 CenterZ=0 NormalX=0 NormalY=0 NormalZ=1 AngleXU=0 Radius=2
    g3: Circle CenterX=80.351 CenterY=-4.92017 CenterZ=0 NormalX=0 NormalY=0 NormalZ=1 AngleXU=0 Radius=3
    g4: Circle CenterX=23.851 CenterY=-4.92017 CenterZ=0 NormalX=0 NormalY=0 NormalZ=1 AngleXU=0 Radius=2
    g5: Circle CenterX=23.851 CenterY=-4.92017 CenterZ=0 NormalX=0 NormalY=0 NormalZ=1 AngleXU=0 Radius=3
    g6: Circle CenterX=23.851 CenterY=-67.6202 CenterZ=0 NormalX=0 NormalY=0 NormalZ=1 AngleXU=0 Radius=2
    g7: Circle CenterX=23.851 CenterY=-67.6202 CenterZ=0 NormalX=0 NormalY=0 NormalZ=1 AngleXU=0 Radius=3
  constraints (8):
    c: Block(g3)
    c: Block(g2)
    c: Block(g1)
    c: Block(g0)
    c: Block(g6)
    c: Block(g7)
    c: Block(g4)
    c: Block(g5)
FEATURE [Part::Feature] Face027
  shape: bbox 11 x 6 x 2e-07 mm, 1 faces, 0 solids (baked)
FEATURE [Part::Revolution] Revolve027
  Angle = 360
  Axis = (0,1,0)
  Base = (0,0,0)
  FaceMakerClass = Part::FaceMakerBullseye
  Placement = pos=(30.3,-1,51.7) rot=(0,0,1;0rad)
  Solid = false
  Source = -> Face027
  Symmetric = false
FEATURE [Part::Feature] Face028
  shape: bbox 11 x 6 x 2e-07 mm, 1 faces, 0 solids (baked)
FEATURE [Part::Revolution] Revolve028
  Angle = 360
  Axis = (0,1,0)
  Base = (0,0,0)
  FaceMakerClass = Part::FaceMakerBullseye
  Placement = pos=(62.3,-1,19.7) rot=(0,0,1;0rad)
  Solid = false
  Source = -> Face028
  Symmetric = false
FEATURE [Part::Feature] Face029
  shape: bbox 11 x 6 x 2e-07 mm, 1 faces, 0 solids (baked)
FEATURE [Part::Revolution] Revolve029
  Angle = 360
  Axis = (0,1,0)
  Base = (0,0,0)
  FaceMakerClass = Part::FaceMakerBullseye
  Placement = pos=(62.3,-1,51.7) rot=(0,0,1;0rad)
  Solid = false
  Source = -> Face029
  Symmetric = false
FEATURE [Part::Feature] Wire
  shape: bbox 11 x 5.2 x 2e-07 mm, 0 faces, 0 solids (baked)
FEATURE [Part::Revolution] Revolve030
  Angle = 360
  Axis = (0,1,0)
  Base = (0,0,0)
  FaceMakerClass = Part::FaceMakerBullseye
  Placement = pos=(30.3,38,19.7) rot=(0,0,1;0rad)
  Solid = true
  Source = -> Wire
  Symmetric = false
FEATURE [Part::Feature] Wire001
  shape: bbox 11 x 5.2 x 2e-07 mm, 0 faces, 0 solids (baked)
FEATURE [Part::Revolution] Revolve031
  Angle = 360
  Axis = (0,1,0)
  Base = (0,0,0)
  FaceMakerClass = Part::FaceMakerBullseye
  Placement = pos=(30.3,38,51.7) rot=(0,0,1;0rad)
  Solid = true
  Source = -> Wire001
  Symmetric = false
FEATURE [Part::Feature] Wire002
  shape: bbox 11 x 5.2 x 2e-07 mm, 0 faces, 0 solids (baked)
FEATURE [Part::Revolution] Revolve032
  Angle = 360
  Axis = (0,1,0)
  Base = (0,0,0)
  FaceMakerClass = Part::FaceMakerBullseye
  Placement = pos=(62.3,38,51.7) rot=(0,0,1;0rad)
  Solid = true
  Source = -> Wire002
  Symmetric = false
FEATURE [Part::Feature] Wire003
  shape: bbox 11 x 5.2 x 2e-07 mm, 0 faces, 0 solids (baked)
FEATURE [Part::Revolution] Revolve033
  Angle = 360
  Axis = (0,1,0)
  Base = (0,0,0)
  FaceMakerClass = Part::FaceMakerBullseye
  Placement = pos=(62.3,38,19.7) rot=(0,0,1;0rad)
  Solid = true
  Source = -> Wire003
  Symmetric = false
FEATURE [Part::MultiFuse] Fusion045  label="altRandScrewHousing"
  Shapes = -> [Revolve029,Revolve027,Revolve028,Revolve026]
FEATURE [Part::MultiFuse] Fusion046  label="fanScrewHousing"
  Shapes = -> [Revolve033,Revolve032,Revolve031,Revolve030]
FEATURE [Sketcher::SketchObject] Sketch015
  FullyConstrained = true
  sketch-geometry (17):
    g0: Circle CenterX=-3.5 CenterY=23.5 CenterZ=0 NormalX=0 NormalY=0 NormalZ=1 AngleXU=0 Radius=1
    g1: Circle CenterX=-1 CenterY=15.25 CenterZ=0 NormalX=0 NormalY=0 NormalZ=1 AngleXU=0 Radius=1
    g2: Circle CenterX=-3.5 CenterY=7 CenterZ=0 NormalX=0 NormalY=0 NormalZ=1 AngleXU=0 Radius=1
    g3: BSplineCurve PolesCount=3 KnotsCount=2 Degree=2 IsPeriodic=0
    g4: GeomPoint X=-3.5 Y=23.5 Z=0
    g5: GeomPoint X=-3.5 Y=7 Z=0
    g6: Circle CenterX=-4.8 CenterY=30.5 CenterZ=0 NormalX=0 NormalY=0 NormalZ=1 AngleXU=0 Radius=1
    g7: Circle CenterX=-3.5 CenterY=30.5 CenterZ=0 NormalX=0 NormalY=0 NormalZ=1 AngleXU=0 Radius=1
    g8: Circle CenterX=-3.5 CenterY=29.2 CenterZ=0 NormalX=0 NormalY=0 NormalZ=1 AngleXU=0 Radius=1
    g9: BSplineCurve PolesCount=3 KnotsCount=2 Degree=2 IsPeriodic=0
    g10: GeomPoint X=-4.8 Y=30.5 Z=0
    g11: GeomPoint X=-3.5 Y=29.2 Z=0
    g12: LineSegment StartX=-3.5 StartY=29.2 StartZ=0 EndX=-3.5 EndY=23.5 EndZ=0
    g13: LineSegment StartX=-4.8 StartY=30.5 StartZ=0 EndX=0 EndY=30.5 EndZ=0
    g14: LineSegment StartX=-3.5 StartY=0.3 StartZ=0 EndX=0 EndY=0.3 EndZ=0
    g15: LineSegment StartX=-3.5 StartY=0.3 StartZ=0 EndX=-3.5 EndY=7 EndZ=0
    g16: LineSegment StartX=0 StartY=0.3 StartZ=0 EndX=0 EndY=30.5 EndZ=0
  constraints (33):
    c: Weight(g0) = 1
    c: Equal(g0,g1)
    c: Equal(g0,g2)
    c: InternalAlignment(g0,g3)
    c: InternalAlignment(g1,g3)
    c: InternalAlignment(g2,g3)
    c: InternalAlignment(g4,g3)
    c: InternalAlignment(g5,g3)
    c: Block(g3)
    c: Weight(g6) = 1
    c: Equal(g6,g7)
    c: Equal(g6,g8)
    c: InternalAlignment(g6,g9)
    c: InternalAlignment(g7,g9)
    c: InternalAlignment(g8,g9)
    c: InternalAlignment(g10,g9)
    c: InternalAlignment(g11,g9)
    c: Block(g9)
    c: Coincident(g12,g9)
    c: Coincident(g12,g3)
    c: Vertical(g12)
    c: Coincident(g13,g9)
    c: Horizontal(g13)
    c: Distance(g13) = 4.8
    c: Horizontal(g14)
    c: Block(g14)
    c: Coincident(g15,g14)
    c: Coincident(g15,g3)
    c: Vertical(g15)
    c: Coincident(g16,g14)
    c: Coincident(g16,g13)
    c: Vertical(g16)
    c: Tangent(g16,g1)
FEATURE [Sketcher::SketchObject] Sketch016
  FullyConstrained = true
  sketch-geometry (16):
    g0: Circle CenterX=-3.5 CenterY=23.5 CenterZ=0 NormalX=0 NormalY=0 NormalZ=1 AngleXU=0 Radius=1
    g1: Circle CenterX=-1 CenterY=15.25 CenterZ=0 NormalX=0 NormalY=0 NormalZ=1 AngleXU=0 Radius=1
    g2: Circle CenterX=-3.5 CenterY=7 CenterZ=0 NormalX=0 NormalY=0 NormalZ=1 AngleXU=0 Radius=1
    g3: BSplineCurve PolesCount=3 KnotsCount=2 Degree=2 IsPeriodic=0
    g4: GeomPoint X=-3.5 Y=23.5 Z=0
    g5: GeomPoint X=-3.5 Y=7 Z=0
    g6: LineSegment StartX=-3.5 StartY=28.2 StartZ=0 EndX=-3.5 EndY=23.5 EndZ=0
    g7: LineSegment StartX=0 StartY=29.5 StartZ=0 EndX=0 EndY=30 EndZ=0
    g8: LineSegment StartX=-3.5 StartY=28.2 StartZ=0 EndX=-3.5 EndY=30 EndZ=0
    g9: LineSegment StartX=0 StartY=30 StartZ=0 EndX=0 EndY=30.5 EndZ=0
    g10: LineSegment StartX=0 StartY=30.5 StartZ=0 EndX=-3.5 EndY=30.5 EndZ=0
    g11: LineSegment StartX=-3.5 StartY=30.5 StartZ=0 EndX=-3.5 EndY=30 EndZ=0
    g12: LineSegment StartX=0 StartY=29.5 StartZ=0 EndX=0 EndY=5 EndZ=0
    g13: LineSegment StartX=-3.5 StartY=0.3 StartZ=0 EndX=-3.5 EndY=7 EndZ=0
    g14: LineSegment StartX=-3.5 StartY=0.3 StartZ=0 EndX=0 EndY=0.3 EndZ=0
    g15: LineSegment StartX=0 StartY=5 StartZ=0 EndX=0 EndY=0.3 EndZ=0
  constraints (39):
    c: Weight(g0) = 1
    c: Equal(g0,g1)
    c: Equal(g0,g2)
    c: InternalAlignment(g0,g3)
    c: InternalAlignment(g1,g3)
    c: InternalAlignment(g2,g3)
    c: InternalAlignment(g4,g3)
    c: InternalAlignment(g5,g3)
    c: Block(g3)
    c: Coincident(g6,g3)
    c: Vertical(g6)
    c: Vertical(g7)
    c: Distance(g7) = 0.5
    c: Coincident(g8,g6)
    c: Vertical(g8)
    c: Block(g6)
    c: Block(g7)
    c: Vertical(g9)
    c: Equal(g7,g9) = 0.5
    c: Block(g9)
    c: Coincident(g9,g7)
    c: Horizontal(g10)
    c: Coincident(g10,g9)
    c: Coincident(g11,g10)
    c: Coincident(g11,g8)
    c: Vertical(g11)
    c: Block(g11)
    c: Coincident(g12,g7)
    c: Vertical(g12)
    c: Coincident(g13,g3)
    c: Vertical(g13)
    c: Distance(g13) = 6.7
    c: Coincident(g14,g13)
    c: Horizontal(g14)
    c: Block(g14)
    c: Coincident(g15,g12)
    c: Coincident(g15,g14)
    c: Vertical(g15)
    c: Block(g15)
FEATURE [Sketcher::SketchObject] Sketch017
  FullyConstrained = true
  sketch-geometry (11):
    g0: LineSegment StartX=-3.5 StartY=1e-16 StartZ=0 EndX=-1.6 EndY=1e-16 EndZ=0
    g1: LineSegment StartX=-1.6 StartY=1e-16 StartZ=0 EndX=-1.6 EndY=1.5 EndZ=0
    g2: LineSegment StartX=-3.5 StartY=1.5 StartZ=0 EndX=-1.6 EndY=1.5 EndZ=0
    g3: LineSegment StartX=-3.5 StartY=1e-16 StartZ=0 EndX=-4.8 EndY=1e-16 EndZ=0
    g4: Circle CenterX=-3.5 CenterY=1.3 CenterZ=0 NormalX=0 NormalY=0 NormalZ=1 AngleXU=0 Radius=1
    g5: Circle CenterX=-3.5 CenterY=1e-16 CenterZ=0 NormalX=0 NormalY=0 NormalZ=1 AngleXU=0 Radius=1
    g6: Circle CenterX=-4.8 CenterY=1e-16 CenterZ=0 NormalX=0 NormalY=0 NormalZ=1 AngleXU=0 Radius=1
    g7: BSplineCurve PolesCount=3 KnotsCount=2 Degree=2 IsPeriodic=0
    g8: GeomPoint X=-3.5 Y=1.3 Z=0
    g9: GeomPoint X=-4.8 Y=1e-16 Z=0
    g10: LineSegment StartX=-3.5 StartY=1.3 StartZ=0 EndX=-3.5 EndY=1.5 EndZ=0
  constraints (24):
    c: Horizontal(g0)
    c: Distance(g0) = 1.9
    c: Block(g0)
    c: Coincident(g1,g0)
    c: Vertical(g1)
    c: Coincident(g2,g1)
    c: Horizontal(g2)
    c: Coincident(g3,g0)
    c: Horizontal(g3)
    c: Distance(g3) = 1.3
    c: Weight(g4) = 1
    c: Equal(g4,g5)
    c: Coincident(g5,g0)
    c: Equal(g4,g6)
    c: Coincident(g7,g3)
    c: InternalAlignment(g4,g7)
    c: InternalAlignment(g5,g7)
    c: InternalAlignment(g6,g7)
    c: InternalAlignment(g8,g7)
    c: InternalAlignment(g9,g7)
    c: Coincident(g10,g7)
    c: Coincident(g10,g2)
    c: Vertical(g10)
    c: Block(g10)
FEATURE [Part::Feature] Face035
  shape: bbox 3.2 x 1.5 x 2e-07 mm, 1 faces, 0 solids (baked)
FEATURE [Part::Revolution] Revolve039  label="backCaseScrewRetainer"
  Angle = 360
  Axis = (0,1,0)
  Base = (0,0,0)
  FaceMakerClass = Part::FaceMakerBullseye
  Placement = pos=(12.5,3,62) rot=(0,0,1;0rad)
  Solid = false
  Source = -> Face035
  Symmetric = false
FEATURE [Part::Feature] Face036
  shape: bbox 3.2 x 1.5 x 2e-07 mm, 1 faces, 0 solids (baked)
FEATURE [Part::Feature] Face039
  shape: bbox 4.8 x 30.2 x 2e-07 mm, 1 faces, 0 solids (baked)
FEATURE [Part::Revolution] Revolve043  label="frontCaseScrewPost002"
  Angle = 360
  Axis = (0,1,0)
  Base = (0,0,0)
  FaceMakerClass = Part::FaceMakerBullseye
  Placement = pos=(89.5,4.5,3.5) rot=(0,0,1;0rad)
  Solid = false
  Source = -> Face039
  Symmetric = false
FEATURE [Part::Feature] Face042
  shape: bbox 4.8 x 30.2 x 2e-07 mm, 1 faces, 0 solids (baked)
FEATURE [Part::Revolution] Revolve046  label="frontCaseScrewPost003"
  Angle = 360
  Axis = (0,1,0)
  Base = (0,0,0)
  FaceMakerClass = Part::FaceMakerBullseye
  Placement = pos=(89.5,4.5,68.5) rot=(0,0,1;0rad)
  Solid = false
  Source = -> Face042
  Symmetric = false
FEATURE [Part::Feature] Face043
  shape: bbox 3.2 x 1.5 x 2e-07 mm, 1 faces, 0 solids (baked)
FEATURE [Part::Revolution] Revolve047  label="frontCaseScrewRetainer002"
  Angle = 360
  Axis = (0,1,0)
  Base = (0,0,0)
  FaceMakerClass = Part::FaceMakerBullseye
  Placement = pos=(89.5,3,68.5) rot=(0,0,1;0rad)
  Solid = false
  Source = -> Face043
  Symmetric = false
FEATURE [Part::Feature] Face044
  shape: bbox 3.2 x 1.5 x 2e-07 mm, 1 faces, 0 solids (baked)
FEATURE [Part::Revolution] Revolve048  label="frontCaseScrewRetainer003"
  Angle = 360
  Axis = (0,1,0)
  Base = (0,0,0)
  FaceMakerClass = Part::FaceMakerBullseye
  Placement = pos=(89.5,3,3.5) rot=(0,0,1;0rad)
  Solid = false
  Source = -> Face044
  Symmetric = false
FEATURE [App::MeasureDistance] Distance002  label="Distance: 1.67 mm"
  Distance = 1.66921
  P1 = (99.2361,4.7524,71.7)
  P2 = (99.2347,6.42161,71.7)
FEATURE [Sketcher::SketchObject] Sketch018
  FullyConstrained = true
  sketch-geometry (7):
    g0: LineSegment StartX=0 StartY=0 StartZ=0 EndX=0 EndY=6 EndZ=0
    g1: Circle CenterX=0 CenterY=0 CenterZ=0 NormalX=0 NormalY=0 NormalZ=1 AngleXU=0 Radius=1
    g2: Circle CenterX=8 CenterY=6 CenterZ=0 NormalX=0 NormalY=0 NormalZ=1 AngleXU=0 Radius=1
    g3: BSplineCurve PolesCount=3 KnotsCount=2 Degree=2 IsPeriodic=0
    g4: GeomPoint X=0 Y=0 Z=0
    g5: GeomPoint X=8 Y=6 Z=0
    g6: LineSegment StartX=0 StartY=6 StartZ=0 EndX=8 EndY=6 EndZ=0
  constraints (14):
    c: Coincident(g0,g-1)
    c: Distance(g0) = 6
    c: Vertical(g0)
    c: Coincident(g3,g0)
    c: Weight(g1) = 1
    c: Equal(g1,g2)
    c: InternalAlignment(g1,g3)
    c: InternalAlignment(g2,g3)
    c: InternalAlignment(g4,g3)
    c: InternalAlignment(g5,g3)
    c: Block(g3)
    c: Coincident(g6,g0)
    c: Coincident(g6,g3)
    c: Horizontal(g6)
FEATURE [Part::Extrusion] Extrude012  label="caseScrewPillarBracket"
  Base = -> Sketch018
  Dir = (0,0,1)
  DirMode = 2
  FaceMakerClass = Part::FaceMakerBullseye
  LengthFwd = 2.4
  LengthRev = 0
  Placement = pos=(15.76,29,8.8) rot=(0,1,0;0rad)
  Solid = true
  Symmetric = false
FEATURE [Sketcher::SketchObject] Sketch019
  FullyConstrained = true
  sketch-geometry (7):
    g0: LineSegment StartX=0 StartY=0 StartZ=0 EndX=0 EndY=6 EndZ=0
    g1: Circle CenterX=0 CenterY=0 CenterZ=0 NormalX=0 NormalY=0 NormalZ=1 AngleXU=0 Radius=1
    g2: Circle CenterX=8 CenterY=6 CenterZ=0 NormalX=0 NormalY=0 NormalZ=1 AngleXU=0 Radius=1
    g3: BSplineCurve PolesCount=3 KnotsCount=2 Degree=2 IsPeriodic=0
    g4: GeomPoint X=0 Y=0 Z=0
    g5: GeomPoint X=8 Y=6 Z=0
    g6: LineSegment StartX=0 StartY=6 StartZ=0 EndX=8 EndY=6 EndZ=0
  constraints (14):
    c: Coincident(g0,g-1)
    c: Distance(g0) = 6
    c: Vertical(g0)
    c: Coincident(g3,g0)
    c: Weight(g1) = 1
    c: Equal(g1,g2)
    c: InternalAlignment(g1,g3)
    c: InternalAlignment(g2,g3)
    c: InternalAlignment(g4,g3)
    c: InternalAlignment(g5,g3)
    c: Block(g3)
    c: Coincident(g6,g0)
    c: Coincident(g6,g3)
    c: Horizontal(g6)
FEATURE [Part::Extrusion] Extrude013  label="caseScrewPillarBracket001"
  Base = -> Sketch019
  Dir = (0,0,1)
  DirMode = 2
  FaceMakerClass = Part::FaceMakerBullseye
  LengthFwd = 2.4
  LengthRev = 0
  Placement = pos=(15.76,29,60.8) rot=(0,0,1;0rad)
  Solid = true
  Symmetric = false
FEATURE [Sketcher::SketchObject] Sketch020
  FullyConstrained = true
  sketch-geometry (7):
    g0: LineSegment StartX=0 StartY=0 StartZ=0 EndX=0 EndY=6 EndZ=0
    g1: Circle CenterX=0 CenterY=0 CenterZ=0 NormalX=0 NormalY=0 NormalZ=1 AngleXU=0 Radius=1
    g2: Circle CenterX=8 CenterY=6 CenterZ=0 NormalX=0 NormalY=0 NormalZ=1 AngleXU=0 Radius=1
    g3: BSplineCurve PolesCount=3 KnotsCount=2 Degree=2 IsPeriodic=0
    g4: GeomPoint X=0 Y=0 Z=0
    g5: GeomPoint X=8 Y=6 Z=0
    g6: LineSegment StartX=0 StartY=6 StartZ=0 EndX=8 EndY=6 EndZ=0
  constraints (14):
    c: Coincident(g0,g-1)
    c: Distance(g0) = 6
    c: Vertical(g0)
    c: Coincident(g3,g0)
    c: Weight(g1) = 1
    c: Equal(g1,g2)
    c: InternalAlignment(g1,g3)
    c: InternalAlignment(g2,g3)
    c: InternalAlignment(g4,g3)
    c: InternalAlignment(g5,g3)
    c: Block(g3)
    c: Coincident(g6,g0)
    c: Coincident(g6,g3)
    c: Horizontal(g6)
FEATURE [Part::Extrusion] Extrude014  label="caseScrewPillarBracket002"
  Base = -> Sketch020
  Dir = (0,0,1)
  DirMode = 2
  FaceMakerClass = Part::FaceMakerBullseye
  LengthFwd = 2.4
  LengthRev = 0
  Placement = pos=(13.7,29,13.26) rot=(0,-1,0;1.5708rad)
  Solid = true
  Symmetric = false
FEATURE [Sketcher::SketchObject] Sketch021
  FullyConstrained = true
  sketch-geometry (7):
    g0: LineSegment StartX=0 StartY=0 StartZ=0 EndX=0 EndY=6 EndZ=0
    g1: Circle CenterX=0 CenterY=0 CenterZ=0 NormalX=0 NormalY=0 NormalZ=1 AngleXU=0 Radius=1
    g2: Circle CenterX=8 CenterY=6 CenterZ=0 NormalX=0 NormalY=0 NormalZ=1 AngleXU=0 Radius=1
    g3: BSplineCurve PolesCount=3 KnotsCount=2 Degree=2 IsPeriodic=0
    g4: GeomPoint X=0 Y=0 Z=0
    g5: GeomPoint X=8 Y=6 Z=0
    g6: LineSegment StartX=0 StartY=6 StartZ=0 EndX=8 EndY=6 EndZ=0
  constraints (14):
    c: Coincident(g0,g-1)
    c: Distance(g0) = 6
    c: Vertical(g0)
    c: Coincident(g3,g0)
    c: Weight(g1) = 1
    c: Equal(g1,g2)
    c: InternalAlignment(g1,g3)
    c: InternalAlignment(g2,g3)
    c: InternalAlignment(g4,g3)
    c: InternalAlignment(g5,g3)
    c: Block(g3)
    c: Coincident(g6,g0)
    c: Coincident(g6,g3)
    c: Horizontal(g6)
FEATURE [Part::Extrusion] Extrude015  label="caseScrewPillarBracket003"
  Base = -> Sketch021
  Dir = (0,0,1)
  DirMode = 2
  FaceMakerClass = Part::FaceMakerBullseye
  LengthFwd = 2.4
  LengthRev = 0
  Placement = pos=(11.3,29,58.74) rot=(0,1,0;1.5708rad)
  Solid = true
  Symmetric = false
FEATURE [Sketcher::SketchObject] Sketch022
  FullyConstrained = true
  sketch-geometry (7):
    g0: LineSegment StartX=0 StartY=0 StartZ=0 EndX=0 EndY=6 EndZ=0
    g1: Circle CenterX=0 CenterY=0 CenterZ=0 NormalX=0 NormalY=0 NormalZ=1 AngleXU=0 Radius=1
    g2: Circle CenterX=8 CenterY=6 CenterZ=0 NormalX=0 NormalY=0 NormalZ=1 AngleXU=0 Radius=1
    g3: BSplineCurve PolesCount=3 KnotsCount=2 Degree=2 IsPeriodic=0
    g4: GeomPoint X=0 Y=0 Z=0
    g5: GeomPoint X=8 Y=6 Z=0
    g6: LineSegment StartX=0 StartY=6 StartZ=0 EndX=8 EndY=6 EndZ=0
  constraints (14):
    c: Coincident(g0,g-1)
    c: Distance(g0) = 6
    c: Vertical(g0)
    c: Coincident(g3,g0)
    c: Weight(g1) = 1
    c: Equal(g1,g2)
    c: InternalAlignment(g1,g3)
    c: InternalAlignment(g2,g3)
    c: InternalAlignment(g4,g3)
    c: InternalAlignment(g5,g3)
    c: Block(g3)
    c: Coincident(g6,g0)
    c: Coincident(g6,g3)
    c: Horizontal(g6)
FEATURE [Part::Extrusion] Extrude016  label="caseScrewPillarBracket004"
  Base = -> Sketch022
  Dir = (0,0,1)
  DirMode = 2
  FaceMakerClass = Part::FaceMakerBullseye
  LengthFwd = 2.4
  LengthRev = 0
  Placement = pos=(88.3,29,65.23) rot=(0,1,0;1.5708rad)
  Solid = true
  Symmetric = false
FEATURE [Sketcher::SketchObject] Sketch023
  FullyConstrained = true
  sketch-geometry (7):
    g0: LineSegment StartX=0 StartY=0 StartZ=0 EndX=0 EndY=6 EndZ=0
    g1: Circle CenterX=0 CenterY=0 CenterZ=0 NormalX=0 NormalY=0 NormalZ=1 AngleXU=0 Radius=1
    g2: Circle CenterX=8 CenterY=6 CenterZ=0 NormalX=0 NormalY=0 NormalZ=1 AngleXU=0 Radius=1
    g3: BSplineCurve PolesCount=3 KnotsCount=2 Degree=2 IsPeriodic=0
    g4: GeomPoint X=0 Y=0 Z=0
    g5: GeomPoint X=8 Y=6 Z=0
    g6: LineSegment StartX=0 StartY=6 StartZ=0 EndX=8 EndY=6 EndZ=0
  constraints (14):
    c: Coincident(g0,g-1)
    c: Distance(g0) = 6
    c: Vertical(g0)
    c: Coincident(g3,g0)
    c: Weight(g1) = 1
    c: Equal(g1,g2)
    c: InternalAlignment(g1,g3)
    c: InternalAlignment(g2,g3)
    c: InternalAlignment(g4,g3)
    c: InternalAlignment(g5,g3)
    c: Block(g3)
    c: Coincident(g6,g0)
    c: Coincident(g6,g3)
    c: Horizontal(g6)
FEATURE [Part::Extrusion] Extrude017  label="caseScrewPillarBracket005"
  Base = -> Sketch023
  Dir = (0,0,1)
  DirMode = 2
  FaceMakerClass = Part::FaceMakerBullseye
  LengthFwd = 2.4
  LengthRev = 0
  Placement = pos=(90.7,29,6.77) rot=(0,-1,0;1.5708rad)
  Solid = true
  Symmetric = false
FEATURE [Sketcher::SketchObject] Sketch024
  FullyConstrained = true
  sketch-geometry (7):
    g0: LineSegment StartX=0 StartY=0 StartZ=0 EndX=0 EndY=6 EndZ=0
    g1: Circle CenterX=0 CenterY=0 CenterZ=0 NormalX=0 NormalY=0 NormalZ=1 AngleXU=0 Radius=1
    g2: Circle CenterX=8 CenterY=6 CenterZ=0 NormalX=0 NormalY=0 NormalZ=1 AngleXU=0 Radius=1
    g3: BSplineCurve PolesCount=3 KnotsCount=2 Degree=2 IsPeriodic=0
    g4: GeomPoint X=0 Y=0 Z=0
    g5: GeomPoint X=8 Y=6 Z=0
    g6: LineSegment StartX=0 StartY=6 StartZ=0 EndX=8 EndY=6 EndZ=0
  constraints (14):
    c: Coincident(g0,g-1)
    c: Distance(g0) = 6
    c: Vertical(g0)
    c: Coincident(g3,g0)
    c: Weight(g1) = 1
    c: Equal(g1,g2)
    c: InternalAlignment(g1,g3)
    c: InternalAlignment(g2,g3)
    c: InternalAlignment(g4,g3)
    c: InternalAlignment(g5,g3)
    c: Block(g3)
    c: Coincident(g6,g0)
    c: Coincident(g6,g3)
    c: Horizontal(g6)
FEATURE [Part::Extrusion] Extrude018  label="caseScrewPillarBracket006"
  Base = -> Sketch024
  Dir = (0,0,1)
  DirMode = 2
  FaceMakerClass = Part::FaceMakerBullseye
  LengthFwd = 2.4
  LengthRev = 0
  Placement = pos=(103.7,29,6.77) rot=(0,-1,0;1.5708rad)
  Solid = true
  Symmetric = false
FEATURE [Sketcher::SketchObject] Sketch025
  FullyConstrained = true
  sketch-geometry (7):
    g0: LineSegment StartX=0 StartY=0 StartZ=0 EndX=0 EndY=6 EndZ=0
    g1: Circle CenterX=0 CenterY=0 CenterZ=0 NormalX=0 NormalY=0 NormalZ=1 AngleXU=0 Radius=1
    g2: Circle CenterX=8 CenterY=6 CenterZ=0 NormalX=0 NormalY=0 NormalZ=1 AngleXU=0 Radius=1
    g3: BSplineCurve PolesCount=3 KnotsCount=2 Degree=2 IsPeriodic=0
    g4: GeomPoint X=0 Y=0 Z=0
    g5: GeomPoint X=8 Y=6 Z=0
    g6: LineSegment StartX=0 StartY=6 StartZ=0 EndX=8 EndY=6 EndZ=0
  constraints (14):
    c: Coincident(g0,g-1)
    c: Distance(g0) = 6
    c: Vertical(g0)
    c: Coincident(g3,g0)
    c: Weight(g1) = 1
    c: Equal(g1,g2)
    c: InternalAlignment(g1,g3)
    c: InternalAlignment(g2,g3)
    c: InternalAlignment(g4,g3)
    c: InternalAlignment(g5,g3)
    c: Block(g3)
    c: Coincident(g6,g0)
    c: Coincident(g6,g3)
    c: Horizontal(g6)
FEATURE [Part::Extrusion] Extrude019  label="caseScrewPillarBracket007"
  Base = -> Sketch025
  Dir = (0,0,1)
  DirMode = 2
  FaceMakerClass = Part::FaceMakerBullseye
  LengthFwd = 2.4
  LengthRev = 0
  Placement = pos=(101.3,29,65.23) rot=(0,1,0;1.5708rad)
  Solid = true
  Symmetric = false
FEATURE [Part::Box] Box011  label="frontCaseScrewPillarBracket"
  AttacherType = Attacher::AttachEngine3D
  Height = 2.4
  Length = 16
  Placement = pos=(87,28,2.3) rot=(0,0,1;0rad)
  Width = 7
FEATURE [Part::Box] Box012  label="frontCaseScrewPillarBracket001"
  AttacherType = Attacher::AttachEngine3D
  Height = 2.4
  Length = 16
  Placement = pos=(87,28,67.3) rot=(0,0,1;0rad)
  Width = 7
FEATURE [Sketcher::SketchObject] Sketch026
  FullyConstrained = true
  sketch-geometry (17):
    g0: Circle CenterX=-3.5 CenterY=23.5 CenterZ=0 NormalX=0 NormalY=0 NormalZ=1 AngleXU=0 Radius=1
    g1: Circle CenterX=-1 CenterY=15.25 CenterZ=0 NormalX=0 NormalY=0 NormalZ=1 AngleXU=0 Radius=1
    g2: Circle CenterX=-3.5 CenterY=7 CenterZ=0 NormalX=0 NormalY=0 NormalZ=1 AngleXU=0 Radius=1
    g3: BSplineCurve PolesCount=3 KnotsCount=2 Degree=2 IsPeriodic=0
    g4: GeomPoint X=-3.5 Y=23.5 Z=0
    g5: GeomPoint X=-3.5 Y=7 Z=0
    g6: Circle CenterX=-4.8 CenterY=30.5 CenterZ=0 NormalX=0 NormalY=0 NormalZ=1 AngleXU=0 Radius=1
    g7: Circle CenterX=-3.5 CenterY=30.5 CenterZ=0 NormalX=0 NormalY=0 NormalZ=1 AngleXU=0 Radius=1
    g8: Circle CenterX=-3.5 CenterY=29.2 CenterZ=0 NormalX=0 NormalY=0 NormalZ=1 AngleXU=0 Radius=1
    g9: BSplineCurve PolesCount=3 KnotsCount=2 Degree=2 IsPeriodic=0
    g10: GeomPoint X=-4.8 Y=30.5 Z=0
    g11: GeomPoint X=-3.5 Y=29.2 Z=0
    g12: LineSegment StartX=-3.5 StartY=29.2 StartZ=0 EndX=-3.5 EndY=23.5 EndZ=0
    g13: LineSegment StartX=-4.8 StartY=30.5 StartZ=0 EndX=0 EndY=30.5 EndZ=0
    g14: LineSegment StartX=-3.5 StartY=5 StartZ=0 EndX=-3.5 EndY=7 EndZ=0
    g15: LineSegment StartX=0 StartY=5 StartZ=0 EndX=0 EndY=30.5 EndZ=0
    g16: LineSegment StartX=-3.5 StartY=5 StartZ=0 EndX=0 EndY=5 EndZ=0
  constraints (33):
    c: Weight(g0) = 1
    c: Equal(g0,g1)
    c: Equal(g0,g2)
    c: InternalAlignment(g0,g3)
    c: InternalAlignment(g1,g3)
    c: InternalAlignment(g2,g3)
    c: InternalAlignment(g4,g3)
    c: InternalAlignment(g5,g3)
    c: Block(g3)
    c: Weight(g6) = 1
    c: Equal(g6,g7)
    c: Equal(g6,g8)
    c: InternalAlignment(g6,g9)
    c: InternalAlignment(g7,g9)
    c: InternalAlignment(g8,g9)
    c: InternalAlignment(g10,g9)
    c: InternalAlignment(g11,g9)
    c: Block(g9)
    c: Coincident(g12,g9)
    c: Coincident(g12,g3)
    c: Vertical(g12)
    c: Coincident(g13,g9)
    c: Horizontal(g13)
    c: Distance(g13) = 4.8
    c: Coincident(g14,g3)
    c: Vertical(g14)
    c: Coincident(g15,g13)
    c: Vertical(g15)
    c: Tangent(g15,g1)
    c: Distance(g14) = 2
    c: Coincident(g16,g14)
    c: Horizontal(g16)
    c: Coincident(g15,g16)
FEATURE [Part::Feature] Face050
  shape: bbox 4.8 x 25.5 x 2e-07 mm, 1 faces, 0 solids (baked)
FEATURE [Part::Revolution] Revolve054  label="moreFrontCaseScrewPost001"
  Angle = 360
  Axis = (0,1,0)
  Base = (0,0,0)
  FaceMakerClass = Part::FaceMakerBullseye
  Placement = pos=(102.5,4.5,3.5) rot=(0,0,1;0rad)
  Solid = false
  Source = -> Face050
  Symmetric = false
FEATURE [Part::Feature] Face051
  shape: bbox 4.8 x 25.5 x 2e-07 mm, 1 faces, 0 solids (baked)
FEATURE [Part::Revolution] Revolve055  label="moreFrontCaseScrewPost002"
  Angle = 360
  Axis = (0,1,0)
  Base = (0,0,0)
  FaceMakerClass = Part::FaceMakerBullseye
  Placement = pos=(102.5,4.5,68.5) rot=(0,0,1;0rad)
  Solid = false
  Source = -> Face051
  Symmetric = false
FEATURE [Sketcher::SketchObject] Sketch027
  FullyConstrained = true
  sketch-geometry (10):
    g0: LineSegment StartX=-1.6 StartY=4.7 StartZ=0 EndX=-1.6 EndY=1.7 EndZ=0
    g1: LineSegment StartX=-3.5 StartY=4.7 StartZ=0 EndX=-1.6 EndY=4.7 EndZ=0
    g2: LineSegment StartX=-1.6 StartY=1.7 StartZ=0 EndX=-1.6 EndY=1.5 EndZ=0
    g3: LineSegment StartX=-1.6 StartY=1.5 StartZ=0 EndX=-5.2 EndY=1.5 EndZ=0
    g4: Circle CenterX=-3.5 CenterY=4.7 CenterZ=0 NormalX=0 NormalY=0 NormalZ=1 AngleXU=0 Radius=1
    g5: Circle CenterX=-3.59627 CenterY=2.99743 CenterZ=0 NormalX=0 NormalY=0 NormalZ=1 AngleXU=0 Radius=1
    g6: Circle CenterX=-5.2 CenterY=1.5 CenterZ=0 NormalX=0 NormalY=0 NormalZ=1 AngleXU=0 Radius=1
    g7: BSplineCurve PolesCount=3 KnotsCount=2 Degree=2 IsPeriodic=0
    g8: GeomPoint X=-3.5 Y=4.7 Z=0
    g9: GeomPoint X=-5.2 Y=1.5 Z=0
  constraints (23):
    c: Vertical(g0)
    c: Distance(g0) = 3
    c: Coincident(g1,g0)
    c: Horizontal(g1)
    c: Block(g0)
    c: Block(g1)
    c: Coincident(g2,g0)
    c: Vertical(g2)
    c: Distance(g2) = 0.2
    c: Coincident(g3,g2)
    c: Horizontal(g3)
    c: Block(g3)
    c: Coincident(g7,g1)
    c: Weight(g4) = 1
    c: Equal(g4,g5)
    c: Equal(g4,g6)
    c: Coincident(g7,g3)
    c: InternalAlignment(g4,g7)
    c: InternalAlignment(g5,g7)
    c: InternalAlignment(g6,g7)
    c: InternalAlignment(g8,g7)
    c: InternalAlignment(g9,g7)
    c: Block(g7)
FEATURE [Sketcher::SketchObject] Sketch028
  FullyConstrained = true
  sketch-geometry (18):
    g0: LineSegment StartX=0 StartY=3e-16 StartZ=0 EndX=0 EndY=1.7 EndZ=0
    g1: LineSegment StartX=-3.5 StartY=0 StartZ=0 EndX=-3.5 EndY=0.9 EndZ=0
    g2: Circle CenterX=-2.7 CenterY=1.7 CenterZ=0 NormalX=0 NormalY=0 NormalZ=1 AngleXU=0 Radius=1
    g3: Circle CenterX=-3.5 CenterY=1.7 CenterZ=0 NormalX=0 NormalY=0 NormalZ=1 AngleXU=0 Radius=1
    g4: Circle CenterX=-3.5 CenterY=0.9 CenterZ=0 NormalX=0 NormalY=0 NormalZ=1 AngleXU=0 Radius=1
    g5: BSplineCurve PolesCount=3 KnotsCount=2 Degree=2 IsPeriodic=0
    g6: GeomPoint X=-2.7 Y=1.7 Z=0
    g7: GeomPoint X=-3.5 Y=0.9 Z=0
    g8: LineSegment StartX=-3.5 StartY=0 StartZ=0 EndX=-3.5 EndY=-7 EndZ=0
    g9: LineSegment StartX=0 StartY=3e-16 StartZ=0 EndX=0 EndY=-7 EndZ=0
    g10: LineSegment StartX=-3.5 StartY=-7 StartZ=0 EndX=0 EndY=-7 EndZ=0
    g11: LineSegment StartX=-2.7 StartY=1.7 StartZ=0 EndX=-1.6 EndY=1.7 EndZ=0
    g12: LineSegment StartX=0 StartY=1.7 StartZ=0 EndX=0 EndY=4.5 EndZ=0
    g13: LineSegment StartX=0 StartY=4.5 StartZ=0 EndX=0 EndY=10.8 EndZ=0
    g14: LineSegment StartX=0 StartY=10.8 StartZ=0 EndX=-2 EndY=10.8 EndZ=0
    g15: LineSegment StartX=-1.6 StartY=4.7 StartZ=0 EndX=-1.6 EndY=1.7 EndZ=0
    g16: LineSegment StartX=-1.6 StartY=4.7 StartZ=0 EndX=-2 EndY=4.7 EndZ=0
    g17: LineSegment StartX=-2 StartY=4.7 StartZ=0 EndX=-2 EndY=10.8 EndZ=0
  constraints (44):
    c: Vertical(g0)
    c: Vertical(g1)
    c: Distance(g1) = 0.9
    c: Block(g0)
    c: Distance(g0) = 1.7
    c: Weight(g2) = 1
    c: Equal(g2,g3)
    c: Equal(g2,g4)
    c: Coincident(g5,g1)
    c: InternalAlignment(g2,g5)
    c: InternalAlignment(g3,g5)
    c: InternalAlignment(g4,g5)
    c: InternalAlignment(g6,g5)
    c: InternalAlignment(g7,g5)
    c: Block(g5)
    c: Coincident(g8,g1)
    c: Vertical(g8)
    c: Distance(g8) = 7
    c: Vertical(g9)
    c: Equal(g8,g9) = 7
    c: Coincident(g9,g0)
    c: Coincident(g10,g8)
    c: Coincident(g10,g9)
    c: Horizontal(g10)
    c: Coincident(g11,g5)
    c: Horizontal(g11)
    c: Coincident(g12,g0)
    c: Vertical(g12)
    c: Distance(g12) = 2.8
    c: Coincident(g13,g12)
    c: Vertical(g13)
    c: Distance(g13) = 6.3
    c: Coincident(g14,g13)
    c: Horizontal(g14)
    c: Distance(g14) = 2
    c: Vertical(g15)
    c: Distance(g15) = 3
    c: Block(g11)
    c: Coincident(g15,g11)
    c: Coincident(g16,g15)
    c: Horizontal(g16)
    c: Coincident(g17,g16)
    c: Coincident(g17,g14)
    c: Vertical(g17)
FEATURE [Part::Revolution] Revolve040  label="backCaseScrewRetainer001"
  Angle = 360
  Axis = (0,1,0)
  Base = (0,0,0)
  FaceMakerClass = Part::FaceMakerBullseye
  Placement = pos=(12.5,3,10) rot=(0,0,1;0rad)
  Solid = false
  Source = -> Face036
  Symmetric = false
FEATURE [Part::Feature] Face055
  shape: bbox 3.5 x 30.2 x 2e-07 mm, 1 faces, 0 solids (baked)
FEATURE [Part::Revolution] Revolve059  label="backCaseScrewPost"
  Angle = 360
  Axis = (0,1,0)
  Base = (0,0,0)
  FaceMakerClass = Part::FaceMakerBullseye
  Placement = pos=(12.5,4.5,10) rot=(0,0,1;0rad)
  Solid = false
  Source = -> Face055
  Symmetric = false
FEATURE [Part::Feature] Face056
  shape: bbox 3.5 x 30.2 x 2e-07 mm, 1 faces, 0 solids (baked)
FEATURE [Part::Revolution] Revolve060  label="backCaseScrewPost001"
  Angle = 360
  Axis = (0,1,0)
  Base = (0,0,0)
  FaceMakerClass = Part::FaceMakerBullseye
  Placement = pos=(12.5,4.5,62) rot=(0,0,1;0rad)
  Solid = false
  Source = -> Face056
  Symmetric = false
FEATURE [Part::Feature] Face057
  shape: bbox 3.5 x 17.8 x 2e-07 mm, 1 faces, 0 solids (baked)
FEATURE [Part::Revolution] Revolve061  label="removeToCreateScrewAndThreadedInsertHole"
  Angle = 360
  Axis = (0,1,0)
  Base = (0,0,0)
  FaceMakerClass = Part::FaceMakerBullseye
  Placement = pos=(12.5,0,10) rot=(0,0,1;0rad)
  Solid = false
  Source = -> Face057
  Symmetric = false
FEATURE [Part::Feature] Face058
  shape: bbox 3.5 x 17.8 x 2e-07 mm, 1 faces, 0 solids (baked)
FEATURE [Part::Revolution] Revolve062  label="removeToCreateScrewAndThreadedInsertHole001"
  Angle = 360
  Axis = (0,1,0)
  Base = (0,0,0)
  FaceMakerClass = Part::FaceMakerBullseye
  Placement = pos=(12.5,0,62) rot=(0,0,1;0rad)
  Solid = false
  Source = -> Face058
  Symmetric = false
FEATURE [Part::Feature] Face059
  shape: bbox 3.5 x 17.8 x 2e-07 mm, 1 faces, 0 solids (baked)
FEATURE [Part::Revolution] Revolve063  label="removeToCreateScrewAndThreadedInsertHole002"
  Angle = 360
  Axis = (0,1,0)
  Base = (0,0,0)
  FaceMakerClass = Part::FaceMakerBullseye
  Placement = pos=(89.5,0,68.5) rot=(0,0,1;0rad)
  Solid = false
  Source = -> Face059
  Symmetric = false
FEATURE [Part::Feature] Face060
  shape: bbox 3.5 x 17.8 x 2e-07 mm, 1 faces, 0 solids (baked)
FEATURE [Part::Revolution] Revolve064  label="removeToCreateScrewAndThreadedInsertHole003"
  Angle = 360
  Axis = (0,1,0)
  Base = (0,0,0)
  FaceMakerClass = Part::FaceMakerBullseye
  Placement = pos=(89.5,0,3.5) rot=(0,0,1;0rad)
  Solid = false
  Source = -> Face060
  Symmetric = false
FEATURE [Part::Feature] Face061
  shape: bbox 3.5 x 17.8 x 2e-07 mm, 1 faces, 0 solids (baked)
FEATURE [Part::Revolution] Revolve065  label="removeToCreateScrewAndThreadedInsertHole004"
  Angle = 360
  Axis = (0,1,0)
  Base = (0,0,0)
  FaceMakerClass = Part::FaceMakerBullseye
  Placement = pos=(102.5,4.7,3.5) rot=(0,0,1;0rad)
  Solid = false
  Source = -> Face061
  Symmetric = false
FEATURE [Part::Feature] Face062
  shape: bbox 3.5 x 17.8 x 2e-07 mm, 1 faces, 0 solids (baked)
FEATURE [Part::Revolution] Revolve066  label="removeToCreateScrewAndThreadedInsertHole005"
  Angle = 360
  Axis = (0,1,0)
  Base = (0,0,0)
  FaceMakerClass = Part::FaceMakerBullseye
  Placement = pos=(102.5,4.7,68.5) rot=(0,0,1;0rad)
  Solid = false
  Source = -> Face062
  Symmetric = false
FEATURE [Part::MultiFuse] Fusion047  label="makeHoles"
  Shapes = -> [Revolve066,Revolve065,Revolve064,Revolve063,Revolve062,Revolve061]
FEATURE [Part::Feature] Face063
  shape: bbox 3.6 x 3.2 x 2e-07 mm, 1 faces, 0 solids (baked)
FEATURE [Part::Revolution] Revolve067  label="moreFrontCaseScrewRetainer002"
  Angle = 360
  Axis = (0,1,0)
  Base = (0,0,0)
  FaceMakerClass = Part::FaceMakerBullseye
  Placement = pos=(102.5,4.5,68.5) rot=(0,0,1;0rad)
  Solid = false
  Source = -> Face063
  Symmetric = false
FEATURE [Part::Feature] Face064
  shape: bbox 3.6 x 3.2 x 2e-07 mm, 1 faces, 0 solids (baked)
FEATURE [Part::Revolution] Revolve068  label="moreFrontCaseScrewRetainer003"
  Angle = 360
  Axis = (0,1,0)
  Base = (0,0,0)
  FaceMakerClass = Part::FaceMakerBullseye
  Placement = pos=(102.5,4.5,3.5) rot=(0,0,1;0rad)
  Solid = false
  Source = -> Face064
  Symmetric = false
FEATURE [Part::Feature] Face065
  shape: bbox 3.5 x 17.8 x 2e-07 mm, 1 faces, 0 solids (baked)
FEATURE [Part::Revolution] Revolve069  label="removeToCreateScrewAndThreadedInsertHole006"
  Angle = 360
  Axis = (0,1,0)
  Base = (0,0,0)
  FaceMakerClass = Part::FaceMakerBullseye
  Placement = pos=(12.5,0,10) rot=(0,0,1;0rad)
  Solid = false
  Source = -> Face065
  Symmetric = false
FEATURE [Part::Feature] Face066
  shape: bbox 3.5 x 17.8 x 2e-07 mm, 1 faces, 0 solids (baked)
FEATURE [Part::Revolution] Revolve070  label="removeToCreateScrewAndThreadedInsertHole007"
  Angle = 360
  Axis = (0,1,0)
  Base = (0,0,0)
  FaceMakerClass = Part::FaceMakerBullseye
  Placement = pos=(12.5,0,62) rot=(0,0,1;0rad)
  Solid = false
  Source = -> Face066
  Symmetric = false
FEATURE [Part::Feature] Face067
  shape: bbox 3.5 x 17.8 x 2e-07 mm, 1 faces, 0 solids (baked)
FEATURE [Part::Revolution] Revolve071  label="removeToCreateScrewAndThreadedInsertHole008"
  Angle = 360
  Axis = (0,1,0)
  Base = (0,0,0)
  FaceMakerClass = Part::FaceMakerBullseye
  Placement = pos=(89.5,0,68.5) rot=(0,0,1;0rad)
  Solid = false
  Source = -> Face067
  Symmetric = false
FEATURE [Part::Feature] Face068
  shape: bbox 3.5 x 17.8 x 2e-07 mm, 1 faces, 0 solids (baked)
FEATURE [Part::Revolution] Revolve072  label="removeToCreateScrewAndThreadedInsertHole009"
  Angle = 360
  Axis = (0,1,0)
  Base = (0,0,0)
  FaceMakerClass = Part::FaceMakerBullseye
  Placement = pos=(89.5,0,3.5) rot=(0,0,1;0rad)
  Solid = false
  Source = -> Face068
  Symmetric = false
FEATURE [Part::Feature] Face069
  shape: bbox 3.5 x 17.8 x 2e-07 mm, 1 faces, 0 solids (baked)
FEATURE [Part::Feature] Face070
  shape: bbox 3.5 x 17.8 x 2e-07 mm, 1 faces, 0 solids (baked)
FEATURE [Part::Revolution] Revolve073  label="removeToCreateScrewAndThreadedInsertHole010"
  Angle = 360
  Axis = (0,1,0)
  Base = (0,0,0)
  FaceMakerClass = Part::FaceMakerBullseye
  Placement = pos=(102.5,4.7,3.5) rot=(0,0,1;0rad)
  Solid = false
  Source = -> Face069
  Symmetric = false
FEATURE [Part::Revolution] Revolve074  label="removeToCreateScrewAndThreadedInsertHole011"
  Angle = 360
  Axis = (0,1,0)
  Base = (0,0,0)
  FaceMakerClass = Part::FaceMakerBullseye
  Placement = pos=(102.5,4.7,68.5) rot=(0,0,1;0rad)
  Solid = false
  Source = -> Face070
  Symmetric = false
FEATURE [Part::MultiFuse] Fusion048  label="makeHoles001"
  Shapes = -> [Revolve074,Revolve073,Revolve072,Revolve071,Revolve070,Revolve069]
FEATURE [Part::MultiFuse] Fusion049  label="caseScrewRetainers"
  Shapes = -> [Revolve067,Revolve068,Revolve048,Revolve047,Revolve039,Revolve040]
FEATURE [Part::Cut] Cut015  label="caseScrewRetainers001"
  Base = -> Fusion049
  Tool = -> Fusion048
FEATURE [Part::MultiFuse] Fusion050  label="casePillars"
  Shapes = -> [Revolve055,Revolve054,Revolve043,Revolve046,Revolve059,Revolve060]
FEATURE [Part::Feature] Face071 .. Face076  x6 (patterned run collapsed; names and placements below)
  shape: bbox 3.5 x 17.8 x 2e-07 mm, 1 faces, 0 solids (baked)
FEATURE [Part::Revolution] Revolve075  label="removeToCreateScrewAndThreadedInsertHole012"
  Angle = 360
  Axis = (0,1,0)
  Base = (0,0,0)
  FaceMakerClass = Part::FaceMakerBullseye
  Placement = pos=(12.5,0,10) rot=(0,0,1;0rad)
  Solid = false
  Source = -> Face071
  Symmetric = false
FEATURE [Part::Revolution] Revolve076  label="removeToCreateScrewAndThreadedInsertHole013"
  Angle = 360
  Axis = (0,1,0)
  Base = (0,0,0)
  FaceMakerClass = Part::FaceMakerBullseye
  Placement = pos=(12.5,0,62) rot=(0,0,1;0rad)
  Solid = false
  Source = -> Face072
  Symmetric = false
FEATURE [Part::Revolution] Revolve077  label="removeToCreateScrewAndThreadedInsertHole014"
  Angle = 360
  Axis = (0,1,0)
  Base = (0,0,0)
  FaceMakerClass = Part::FaceMakerBullseye
  Placement = pos=(89.5,0,68.5) rot=(0,0,1;0rad)
  Solid = false
  Source = -> Face073
  Symmetric = false
FEATURE [Part::Revolution] Revolve078  label="removeToCreateScrewAndThreadedInsertHole015"
  Angle = 360
  Axis = (0,1,0)
  Base = (0,0,0)
  FaceMakerClass = Part::FaceMakerBullseye
  Placement = pos=(89.5,0,3.5) rot=(0,0,1;0rad)
  Solid = false
  Source = -> Face074
  Symmetric = false
FEATURE [Part::Revolution] Revolve079  label="removeToCreateScrewAndThreadedInsertHole016"
  Angle = 360
  Axis = (0,1,0)
  Base = (0,0,0)
  FaceMakerClass = Part::FaceMakerBullseye
  Placement = pos=(102.5,4.7,3.5) rot=(0,0,1;0rad)
  Solid = false
  Source = -> Face075
  Symmetric = false
FEATURE [Part::Revolution] Revolve080  label="removeToCreateScrewAndThreadedInsertHole017"
  Angle = 360
  Axis = (0,1,0)
  Base = (0,0,0)
  FaceMakerClass = Part::FaceMakerBullseye
  Placement = pos=(102.5,4.7,68.5) rot=(0,0,1;0rad)
  Solid = false
  Source = -> Face076
  Symmetric = false
FEATURE [Part::MultiFuse] Fusion051  label="makeHoles002"
  Shapes = -> [Revolve080,Revolve079,Revolve078,Revolve077,Revolve076,Revolve075]
FEATURE [Part::Cut] Cut016  label="caesPillars"
  Base = -> Fusion050
  Tool = -> Fusion051
FEATURE [Part::Revolution] Revolve009  label="plugHousing016"
  Angle = 360
  Axis = (0,1,0)
  Base = (0,0,0)
  FaceMakerClass = Part::FaceMakerBullseye
  Placement = pos=(0,0,36.15) rot=(0,0,1;0rad)
  Solid = false
  Source = -> Face012
  Symmetric = false
FEATURE [Part::MultiFuse] Fusion014  label="plugHousing023"
  Placement = pos=(0,0,0) rot=(0,0,1;1.5708rad)
  Shapes = -> [Revolve011,Revolve009]
FEATURE [Part::Revolution] Revolve010  label="plugHousing017"
  Angle = 360
  Axis = (0,1,0)
  Base = (0,0,0)
  FaceMakerClass = Part::FaceMakerBullseye
  Placement = pos=(0,0,36.15) rot=(0,0,1;0rad)
  Solid = false
  Source = -> Face014
  Symmetric = false
FEATURE [Part::MultiFuse] Fusion015  label="plugHousing024"
  Placement = pos=(0,0,0) rot=(0,0,1;1.5708rad)
  Shapes = -> [Revolve010,Revolve015]
FEATURE [Part::Revolution] Revolve014  label="plugHousing026"
  Angle = 360
  Axis = (0,1,0)
  Base = (0,0,0)
  FaceMakerClass = Part::FaceMakerBullseye
  Placement = pos=(0,0,36.15) rot=(0,0,1;0rad)
  Solid = false
  Source = -> Face011
  Symmetric = false
FEATURE [Part::Revolution] Revolve013  label="plugHousing025"
  Angle = 360
  Axis = (0,1,0)
  Base = (0,0,0)
  FaceMakerClass = Part::FaceMakerBullseye
  Placement = pos=(0,0,36.15) rot=(0,0,1;0rad)
  Solid = false
  Source = -> Face015
  Symmetric = false
FEATURE [Part::MultiFuse] Fusion016  label="plugHousing028"
  Placement = pos=(0,19,0) rot=(0,0,1;3.14159rad)
  Shapes = -> [Fusion014,Fusion013]
FEATURE [Part::MultiFuse] Fusion011  label="plugHousing018"
  Placement = pos=(0,0,0) rot=(0,0,1;1.5708rad)
  Shapes = -> [Revolve014,Revolve013]
FEATURE [Part::MultiFuse] Fusion012  label="plugHousing019"
  Placement = pos=(0,19,0) rot=(0,0,1;3.14159rad)
  Shapes = -> [Fusion011,Fusion015]
FEATURE [Part::MultiFuse] Fusion017  label="plugHousing029"
  Placement = pos=(122.621,0,-0.15) rot=(0,0,1;0rad)
  Shapes = -> [Fusion016,Fusion012]
FEATURE [Part::MultiFuse] Fusion052  label="casePillarRetainers"
  Shapes = -> [Extrude012,Extrude013,Extrude014,Extrude015,Extrude016,Extrude017,Extrude018,Extrude019,Box011,Box012]
FEATURE [Part::Feature] Face077
  shape: bbox 3.5 x 17.8 x 2e-07 mm, 1 faces, 0 solids (baked)
FEATURE [Part::Revolution] Revolve081  label="removeToCreateScrewAndThreadedInsertHole018"
  Angle = 360
  Axis = (0,1,0)
  Base = (0,0,0)
  FaceMakerClass = Part::FaceMakerBullseye
  Placement = pos=(62.3,30.3,19.7) rot=(0,0,1;0rad)
  Solid = false
  Source = -> Face077
  Symmetric = false
FEATURE [Part::Feature] Face078
  shape: bbox 3.5 x 17.8 x 2e-07 mm, 1 faces, 0 solids (baked)
FEATURE [Part::Revolution] Revolve082  label="removeToCreateScrewAndThreadedInsertHole019"
  Angle = 360
  Axis = (0,1,0)
  Base = (0,0,0)
  FaceMakerClass = Part::FaceMakerBullseye
  Placement = pos=(62.3,30.3,51.7) rot=(0,0,1;0rad)
  Solid = false
  Source = -> Face078
  Symmetric = false
FEATURE [Part::Feature] Face079
  shape: bbox 3.5 x 17.8 x 2e-07 mm, 1 faces, 0 solids (baked)
FEATURE [Part::Revolution] Revolve083  label="removeToCreateScrewAndThreadedInsertHole020"
  Angle = 360
  Axis = (0,1,0)
  Base = (0,0,0)
  FaceMakerClass = Part::FaceMakerBullseye
  Placement = pos=(30.3,30.3,19.7) rot=(0,0,1;0rad)
  Solid = false
  Source = -> Face079
  Symmetric = false
FEATURE [Part::Feature] Face080
  shape: bbox 3.5 x 17.8 x 2e-07 mm, 1 faces, 0 solids (baked)
FEATURE [Part::Revolution] Revolve084  label="removeToCreateScrewAndThreadedInsertHole021"
  Angle = 360
  Axis = (0,1,0)
  Base = (0,0,0)
  FaceMakerClass = Part::FaceMakerBullseye
  Placement = pos=(30.3,30.3,51.7) rot=(0,0,1;0rad)
  Solid = false
  Source = -> Face080
  Symmetric = false
FEATURE [Part::MultiFuse] Fusion053  label="createThreadedInsertHolesForFan"
  Shapes = -> [Revolve081,Revolve082,Revolve083,Revolve084]
FEATURE [Part::Cut] Cut017  label="fanScrewHousing001"
  Base = -> Fusion046
  Tool = -> Fusion053
FEATURE [Part::Feature] Face081
  shape: bbox 3.5 x 17.8 x 2e-07 mm, 1 faces, 0 solids (baked)
FEATURE [Part::Revolution] Revolve085  label="removeToCreateScrewAndThreadedInsertHole022"
  Angle = 360
  Axis = (0,1,0)
  Base = (0,0,0)
  FaceMakerClass = Part::FaceMakerBullseye
  Placement = pos=(62.3,30.3,19.7) rot=(0,0,1;0rad)
  Solid = false
  Source = -> Face081
  Symmetric = false
FEATURE [Part::Feature] Face082
  shape: bbox 3.5 x 17.8 x 2e-07 mm, 1 faces, 0 solids (baked)
FEATURE [Part::Revolution] Revolve086  label="removeToCreateScrewAndThreadedInsertHole023"
  Angle = 360
  Axis = (0,1,0)
  Base = (0,0,0)
  FaceMakerClass = Part::FaceMakerBullseye
  Placement = pos=(62.3,30.3,51.7) rot=(0,0,1;0rad)
  Solid = false
  Source = -> Face082
  Symmetric = false
FEATURE [Part::Feature] Face083
  shape: bbox 3.5 x 17.8 x 2e-07 mm, 1 faces, 0 solids (baked)
FEATURE [Part::Revolution] Revolve087  label="removeToCreateScrewAndThreadedInsertHole024"
  Angle = 360
  Axis = (0,1,0)
  Base = (0,0,0)
  FaceMakerClass = Part::FaceMakerBullseye
  Placement = pos=(30.3,30.3,19.7) rot=(0,0,1;0rad)
  Solid = false
  Source = -> Face083
  Symmetric = false
FEATURE [Part::Feature] Face084
  shape: bbox 3.5 x 17.8 x 2e-07 mm, 1 faces, 0 solids (baked)
FEATURE [Part::Revolution] Revolve088  label="removeToCreateScrewAndThreadedInsertHole025"
  Angle = 360
  Axis = (0,1,0)
  Base = (0,0,0)
  FaceMakerClass = Part::FaceMakerBullseye
  Placement = pos=(30.3,30.3,51.7) rot=(0,0,1;0rad)
  Solid = false
  Source = -> Face084
  Symmetric = false
FEATURE [Part::MultiFuse] Fusion054  label="createThreadedInsertHolesForFan001"
  Shapes = -> [Revolve085,Revolve086,Revolve087,Revolve088]
FEATURE [Part::Cut] Cut018  label="top007"
  Base = -> Fusion040
  Tool = -> Fusion054
FEATURE [Sketcher::SketchObject] Sketch029
  FullyConstrained = false
  Placement = pos=(0,0,0) rot=(1,0,0;1.5708rad)
  sketch-geometry (24):
    g0: ArcOfCircle CenterX=-4 CenterY=-10.5 CenterZ=0 NormalX=0 NormalY=0 NormalZ=1 AngleXU=0 Radius=1.5 StartAngle=6e-16 EndAngle=3.14159
    g1: ArcOfCircle CenterX=-34.2 CenterY=-10.5 CenterZ=0 NormalX=0 NormalY=0 NormalZ=1 AngleXU=0 Radius=1.5 StartAngle=0 EndAngle=3.14159
    g2: ArcOfCircle CenterX=-34.2 CenterY=-27.7 CenterZ=0 NormalX=0 NormalY=0 NormalZ=1 AngleXU=0 Radius=1.5 StartAngle=3.14159 EndAngle=6.28319
    g3: ArcOfCircle CenterX=-4 CenterY=-27.7 CenterZ=0 NormalX=0 NormalY=0 NormalZ=1 AngleXU=0 Radius=1.5 StartAngle=3.1416 EndAngle=6.28319
    g4: ArcOfCircle CenterX=-10 CenterY=-4.3 CenterZ=0 NormalX=0 NormalY=0 NormalZ=1 AngleXU=0 Radius=1.5 StartAngle=2e-16 EndAngle=3.14159
    g5: ArcOfCircle CenterX=-16.1 CenterY=-1.8 CenterZ=0 NormalX=0 NormalY=0 NormalZ=1 AngleXU=0 Radius=1.5 StartAngle=5e-16 EndAngle=3.14159
    g6: ArcOfCircle CenterX=-22.1 CenterY=-1.8 CenterZ=0 NormalX=0 NormalY=0 NormalZ=1 AngleXU=0 Radius=1.5 StartAngle=5e-16 EndAngle=3.14159
    g7: ArcOfCircle CenterX=-28.2 CenterY=-4.3 CenterZ=0 NormalX=0 NormalY=0 NormalZ=1 AngleXU=0 Radius=1.5 StartAngle=2e-16 EndAngle=3.14159
    g8: ArcOfCircle CenterX=-10 CenterY=-33.9 CenterZ=0 NormalX=0 NormalY=0 NormalZ=1 AngleXU=0 Radius=1.5 StartAngle=3.14159 EndAngle=6.28319
    g9: ArcOfCircle CenterX=-16.1 CenterY=-36.4 CenterZ=0 NormalX=0 NormalY=0 NormalZ=1 AngleXU=0 Radius=1.5 StartAngle=3.14159 EndAngle=6.28319
    g10: ArcOfCircle CenterX=-22.1 CenterY=-36.4 CenterZ=0 NormalX=0 NormalY=0 NormalZ=1 AngleXU=0 Radius=1.5 StartAngle=3.14159 EndAngle=6.28319
    g11: ArcOfCircle CenterX=-28.2 CenterY=-33.9 CenterZ=0 NormalX=0 NormalY=0 NormalZ=1 AngleXU=0 Radius=1.5 StartAngle=3.14159 EndAngle=6.28319
    g12: LineSegment StartX=-35.7 StartY=-10.5 StartZ=0 EndX=-35.7 EndY=-27.7 EndZ=0
    g13: LineSegment StartX=-32.7 StartY=-10.5 StartZ=0 EndX=-32.7 EndY=-27.7 EndZ=0
    g14: LineSegment StartX=-29.7 StartY=-33.9 StartZ=0 EndX=-29.7 EndY=-4.3 EndZ=0
    g15: LineSegment StartX=-26.7 StartY=-33.9 StartZ=0 EndX=-26.7 EndY=-4.3 EndZ=0
    g16: LineSegment StartX=-2.5 StartY=-10.5 StartZ=0 EndX=-2.5 EndY=-27.7 EndZ=0
    g17: LineSegment StartX=-8.5 StartY=-4.3 StartZ=0 EndX=-8.5 EndY=-33.9 EndZ=0
    g18: LineSegment StartX=-5.5 StartY=-10.5 StartZ=0 EndX=-5.5 EndY=-27.7 EndZ=0
    g19: LineSegment StartX=-11.5 StartY=-4.3 StartZ=0 EndX=-11.5 EndY=-33.9 EndZ=0
    g20: LineSegment StartX=-14.6 StartY=-1.8 StartZ=0 EndX=-14.6 EndY=-36.4 EndZ=0
    g21: LineSegment StartX=-17.6 StartY=-1.8 StartZ=0 EndX=-17.6 EndY=-36.4 EndZ=0
    g22: LineSegment StartX=-20.6 StartY=-36.4 StartZ=0 EndX=-20.6 EndY=-1.8 EndZ=0
    g23: LineSegment StartX=-23.6 StartY=-1.8 StartZ=0 EndX=-23.6 EndY=-36.4 EndZ=0
  constraints (48):
    c: Block(g0)
    c: Block(g1)
    c: Block(g2)
    c: Block(g3)
    c: Block(g4)
    c: Block(g5)
    c: Block(g6)
    c: Block(g7)
    c: Block(g8)
    c: Block(g9)
    c: Block(g10)
    c: Block(g11)
    c: Coincident(g12,g1)
    c: Coincident(g12,g2)
    c: Vertical(g12)
    c: Coincident(g13,g1)
    c: Coincident(g13,g2)
    c: Vertical(g13)
    c: Coincident(g14,g11)
    c: Coincident(g14,g7)
    c: Vertical(g14)
    c: Coincident(g15,g11)
    c: Coincident(g15,g7)
    c: Vertical(g15)
    c: Coincident(g16,g0)
    c: Coincident(g16,g3)
    c: Vertical(g16)
    c: Coincident(g17,g4)
    c: Coincident(g17,g8)
    c: Vertical(g17)
    c: Coincident(g18,g0)
    c: Coincident(g18,g3)
    c: Vertical(g18)
    c: Coincident(g19,g4)
    c: Coincident(g19,g8)
    c: Vertical(g19)
    c: Coincident(g20,g5)
    c: Coincident(g20,g9)
    c: Vertical(g20)
    c: Coincident(g21,g5)
    c: Coincident(g21,g9)
    c: Vertical(g21)
    c: Coincident(g22,g10)
    c: Coincident(g22,g6)
    c: Vertical(g22)
    c: Coincident(g23,g6)
    c: Coincident(g23,g10)
    c: Vertical(g23)
FEATURE [Part::Extrusion] Extrude020  label="removeToCreateFanGrillHoles"
  Base = -> Sketch029
  Dir = (0,-1,6e-16)
  DirMode = 2
  FaceMakerClass = Part::FaceMakerBullseye
  LengthFwd = 10
  LengthRev = 0
  Placement = pos=(65.4,44,54.82) rot=(0,0,1;0rad)
  Solid = true
  Symmetric = false
FEATURE [Part::MultiFuse] Fusion055  label="top008"
  Shapes = -> [Cut017,Cut018]
FEATURE [Part::Cut] Cut019  label="top009"
  Base = -> Fusion055
  Tool = -> Extrude020
FEATURE [App::MeasureDistance] Distance003  label="Distance: 71.95 mm"
  Distance = 71.9513
  P1 = (117,38,72)
  P2 = (117,38,0.0487319)
FEATURE [Sketcher::SketchObject] Sketch030
  FullyConstrained = true
  Placement = pos=(117,19,0) rot=(0.57735,0.57735,0.57735;2.0944rad)
  sketch-geometry (48):
    g0: LineSegment StartX=-49.19 StartY=69.25 StartZ=0 EndX=-49.19 EndY=66.25 EndZ=0
    g1: LineSegment StartX=-49.19 StartY=63.5 StartZ=0 EndX=-49.19 EndY=60.5 EndZ=0
    g2: LineSegment StartX=-49.19 StartY=57.75 StartZ=0 EndX=-49.19 EndY=54.75 EndZ=0
    g3: LineSegment StartX=-49.19 StartY=52 StartZ=0 EndX=-49.19 EndY=49 EndZ=0
    g4: LineSegment StartX=-49.19 StartY=46.25 StartZ=0 EndX=-49.19 EndY=43.25 EndZ=0
    g5: LineSegment StartX=-49.19 StartY=40.5 StartZ=0 EndX=-49.19 EndY=37.5 EndZ=0
    g6: LineSegment StartX=-49.19 StartY=34.5 StartZ=0 EndX=-49.19 EndY=31.5 EndZ=0
    g7: LineSegment StartX=-49.19 StartY=28.75 StartZ=0 EndX=-49.19 EndY=25.75 EndZ=0
    g8: LineSegment StartX=-49.19 StartY=23 StartZ=0 EndX=-49.19 EndY=20 EndZ=0
    g9: LineSegment StartX=-49.19 StartY=17.25 StartZ=0 EndX=-49.19 EndY=14.25 EndZ=0
    g10: LineSegment StartX=-49.19 StartY=11.5 StartZ=0 EndX=-49.19 EndY=8.5 EndZ=0
    g11: LineSegment StartX=-49.19 StartY=5.75 StartZ=0 EndX=-49.19 EndY=2.75 EndZ=0
    g12: ArcOfCircle CenterX=-1.5 CenterY=67.75 CenterZ=0 NormalX=0 NormalY=0 NormalZ=1 AngleXU=0 Radius=1.5 StartAngle=4.71239 EndAngle=7.85398
    g13: ArcOfCircle CenterX=-1.5 CenterY=62 CenterZ=0 NormalX=0 NormalY=0 NormalZ=1 AngleXU=0 Radius=1.5 StartAngle=4.71239 EndAngle=7.85398
    g14: ArcOfCircle CenterX=-1.5 CenterY=56.25 CenterZ=0 NormalX=0 NormalY=0 NormalZ=1 AngleXU=0 Radius=1.5 StartAngle=4.71239 EndAngle=7.85398
    g15: ArcOfCircle CenterX=-11.49 CenterY=50.5 CenterZ=0 NormalX=0 NormalY=0 NormalZ=1 AngleXU=0 Radius=1.5 StartAngle=4.71239 EndAngle=7.85398
    g16: ArcOfCircle CenterX=-16.28 CenterY=44.75 CenterZ=0 NormalX=0 NormalY=0 NormalZ=1 AngleXU=0 Radius=1.5 StartAngle=4.71239 EndAngle=7.85398
    g17: ArcOfCircle CenterX=-18.2337 CenterY=39 CenterZ=0 NormalX=0 NormalY=0 NormalZ=1 AngleXU=0 Radius=1.5 StartAngle=4.71485 EndAngle=7.85398
    g18: ArcOfCircle CenterX=-16.2837 CenterY=27.25 CenterZ=0 NormalX=0 NormalY=0 NormalZ=1 AngleXU=0 Radius=1.5 StartAngle=4.71485 EndAngle=7.85398
    g19: ArcOfCircle CenterX=-18.2337 CenterY=33 CenterZ=0 NormalX=0 NormalY=0 NormalZ=1 AngleXU=0 Radius=1.5 StartAngle=4.71485 EndAngle=7.85398
    g20: ArcOfCircle CenterX=-11.49 CenterY=21.5 CenterZ=0 NormalX=0 NormalY=0 NormalZ=1 AngleXU=0 Radius=1.5 StartAngle=4.71239 EndAngle=7.85398
    g21: ArcOfCircle CenterX=-1.5 CenterY=4.25 CenterZ=0 NormalX=0 NormalY=0 NormalZ=1 AngleXU=0 Radius=1.5 StartAngle=4.71239 EndAngle=7.85398
    g22: ArcOfCircle CenterX=-1.5 CenterY=10 CenterZ=0 NormalX=0 NormalY=0 NormalZ=1 AngleXU=0 Radius=1.5 StartAngle=4.71239 EndAngle=7.85398
    g23: ArcOfCircle CenterX=-1.5 CenterY=15.75 CenterZ=0 NormalX=0 NormalY=0 NormalZ=1 AngleXU=0 Radius=1.5 StartAngle=4.71239 EndAngle=7.85398
    g24: LineSegment StartX=-49.19 StartY=69.25 StartZ=0 EndX=-1.5 EndY=69.25 EndZ=0
    g25: LineSegment StartX=-49.19 StartY=66.25 StartZ=0 EndX=-1.5 EndY=66.25 EndZ=0
    g26: LineSegment StartX=-49.19 StartY=63.5 StartZ=0 EndX=-1.5 EndY=63.5 EndZ=0
    g27: LineSegment StartX=-49.19 StartY=60.5 StartZ=0 EndX=-1.5 EndY=60.5 EndZ=0
    g28: LineSegment StartX=-49.19 StartY=57.75 StartZ=0 EndX=-1.5 EndY=57.75 EndZ=0
    g29: LineSegment StartX=-49.19 StartY=54.75 StartZ=0 EndX=-1.5 EndY=54.75 EndZ=0
    g30: LineSegment StartX=-49.19 StartY=52 StartZ=0 EndX=-11.49 EndY=52 EndZ=0
    g31: LineSegment StartX=-49.19 StartY=49 StartZ=0 EndX=-11.49 EndY=49 EndZ=0
    g32: LineSegment StartX=-49.19 StartY=46.25 StartZ=0 EndX=-16.28 EndY=46.25 EndZ=0
    g33: LineSegment StartX=-49.19 StartY=43.25 StartZ=0 EndX=-16.28 EndY=43.25 EndZ=0
    g34: LineSegment StartX=-49.19 StartY=40.5 StartZ=0 EndX=-18.2337 EndY=40.5 EndZ=0
    g35: LineSegment StartX=-49.19 StartY=37.5 StartZ=0 EndX=-18.23 EndY=37.5 EndZ=0
    g36: LineSegment StartX=-49.19 StartY=34.5 StartZ=0 EndX=-18.2337 EndY=34.5 EndZ=0
    g37: LineSegment StartX=-49.19 StartY=31.5 StartZ=0 EndX=-18.23 EndY=31.5 EndZ=0
    g38: LineSegment StartX=-49.19 StartY=28.75 StartZ=0 EndX=-16.2837 EndY=28.75 EndZ=0
    g39: LineSegment StartX=-49.19 StartY=25.75 StartZ=0 EndX=-16.28 EndY=25.75 EndZ=0
    g40: LineSegment StartX=-49.19 StartY=23 StartZ=0 EndX=-11.49 EndY=23 EndZ=0
    g41: LineSegment StartX=-49.19 StartY=20 StartZ=0 EndX=-11.49 EndY=20 EndZ=0
    g42: LineSegment StartX=-49.19 StartY=17.25 StartZ=0 EndX=-1.5 EndY=17.25 EndZ=0
    g43: LineSegment StartX=-49.19 StartY=14.25 StartZ=0 EndX=-1.5 EndY=14.25 EndZ=0
    g44: LineSegment StartX=-49.19 StartY=11.5 StartZ=0 EndX=-1.5 EndY=11.5 EndZ=0
    g45: LineSegment StartX=-49.19 StartY=8.5 StartZ=0 EndX=-1.5 EndY=8.5 EndZ=0
    g46: LineSegment StartX=-49.19 StartY=5.75 StartZ=0 EndX=-1.5 EndY=5.75 EndZ=0
    g47: LineSegment StartX=-49.19 StartY=2.75 StartZ=0 EndX=-1.5 EndY=2.75 EndZ=0
  constraints (120):
    c: Vertical(g0)
    c: Distance(g0) = 3
    c: Block(g0)
    c: Vertical(g1)
    c: Distance(g1) = 3
    c: Vertical(g2)
    c: Equal(g0,g2) = 3
    c: Block(g2)
    c: Vertical(g3)
    c: Equal(g1,g3) = 3
    c: Vertical(g4)
    c: Equal(g0,g4) = 3
    c: Block(g4)
    c: Vertical(g5)
    c: Equal(g1,g5) = 3
    c: Vertical(g6)
    c: Equal(g0,g6) = 3
    c: Block(g6)
    c: Vertical(g7)
    c: Equal(g1,g7) = 3
    c: Vertical(g8)
    c: Equal(g0,g8) = 3
    c: Block(g8)
    c: Vertical(g9)
    c: Equal(g1,g9) = 3
    c: Vertical(g10)
    c: Equal(g0,g10) = 3
    c: Block(g10)
    c: Vertical(g11)
    c: Equal(g1,g11) = 3
    c: Block(g12)
    c: Block(g13)
    c: Block(g14)
    c: Block(g15)
    c: Block(g16)
    c: Block(g17)
    c: Block(g18)
    c: Block(g19)
    c: Block(g20)
    c: Block(g21)
    c: Block(g22)
    c: Block(g23)
    c: Block(g11)
    c: Block(g9)
    c: Block(g7)
    c: Block(g5)
    c: Block(g3)
    c: Block(g1)
    c: Coincident(g24,g0)
    c: Coincident(g24,g12)
    c: Horizontal(g24)
    c: Coincident(g25,g0)
    c: Coincident(g25,g12)
    c: Horizontal(g25)
    c: Coincident(g26,g1)
    c: Coincident(g26,g13)
    c: Horizontal(g26)
    c: Coincident(g27,g1)
    c: Coincident(g27,g13)
    c: Horizontal(g27)
    c: Coincident(g28,g2)
    c: Coincident(g28,g14)
    c: Horizontal(g28)
    c: Coincident(g29,g2)
    c: Coincident(g29,g14)
    c: Horizontal(g29)
    c: Coincident(g30,g3)
    c: Coincident(g30,g15)
    c: Horizontal(g30)
    c: Coincident(g31,g3)
    c: Coincident(g31,g15)
    c: Horizontal(g31)
    c: Coincident(g32,g4)
    c: Coincident(g32,g16)
    c: Horizontal(g32)
    c: Coincident(g33,g4)
    c: Coincident(g33,g16)
    c: Horizontal(g33)
    c: Coincident(g34,g5)
    c: Coincident(g34,g17)
    c: Horizontal(g34)
    c: Coincident(g35,g5)
    c: Coincident(g35,g17)
    c: Horizontal(g35)
    c: Coincident(g36,g6)
    c: Coincident(g36,g19)
    c: Horizontal(g36)
    c: Coincident(g37,g6)
    c: Coincident(g37,g19)
    c: Horizontal(g37)
    c: Coincident(g38,g7)
    c: Coincident(g38,g18)
    c: Horizontal(g38)
    c: Coincident(g39,g7)
    c: Coincident(g39,g18)
    c: Horizontal(g39)
    c: Coincident(g40,g8)
    c: Coincident(g40,g20)
    c: Horizontal(g40)
    c: Coincident(g41,g8)
    c: Coincident(g41,g20)
    c: Horizontal(g41)
    c: Coincident(g42,g9)
    c: Coincident(g42,g23)
    c: Horizontal(g42)
    c: Coincident(g43,g9)
    c: Coincident(g43,g23)
    c: Horizontal(g43)
    c: Coincident(g44,g10)
    c: Coincident(g44,g22)
    c: Horizontal(g44)
    c: Coincident(g45,g10)
    c: Coincident(g45,g22)
    c: Horizontal(g45)
    c: Coincident(g46,g11)
    c: Coincident(g46,g21)
    c: Horizontal(g46)
    c: Coincident(g47,g11)
    c: Coincident(g47,g21)
    c: Horizontal(g47)
FEATURE [Sketcher::SketchObject] Sketch031
  FullyConstrained = true
  Placement = pos=(117,19,0) rot=(0.57735,0.57735,0.57735;2.0944rad)
  sketch-geometry (24):
    g0: ArcOfCircle CenterX=-49.19 CenterY=67.75 CenterZ=0 NormalX=0 NormalY=0 NormalZ=1 AngleXU=0 Radius=1.5 StartAngle=1.5708 EndAngle=4.71239
    g1: ArcOfCircle CenterX=-49.19 CenterY=62 CenterZ=0 NormalX=0 NormalY=0 NormalZ=1 AngleXU=0 Radius=1.5 StartAngle=1.5708 EndAngle=4.71239
    g2: ArcOfCircle CenterX=-49.19 CenterY=56.25 CenterZ=0 NormalX=0 NormalY=0 NormalZ=1 AngleXU=0 Radius=1.5 StartAngle=1.5708 EndAngle=4.71239
    g3: ArcOfCircle CenterX=-49.19 CenterY=50.5 CenterZ=0 NormalX=0 NormalY=0 NormalZ=1 AngleXU=0 Radius=1.5 StartAngle=1.5708 EndAngle=4.71239
    g4: ArcOfCircle CenterX=-49.19 CenterY=44.75 CenterZ=0 NormalX=0 NormalY=0 NormalZ=1 AngleXU=0 Radius=1.5 StartAngle=1.5708 EndAngle=4.71239
    g5: ArcOfCircle CenterX=-49.19 CenterY=39 CenterZ=0 NormalX=0 NormalY=0 NormalZ=1 AngleXU=0 Radius=1.5 StartAngle=1.5708 EndAngle=4.71239
    g6: ArcOfCircle CenterX=-49.19 CenterY=33 CenterZ=0 NormalX=0 NormalY=0 NormalZ=1 AngleXU=0 Radius=1.5 StartAngle=1.5708 EndAngle=4.71239
    g7: ArcOfCircle CenterX=-49.19 CenterY=27.25 CenterZ=0 NormalX=0 NormalY=0 NormalZ=1 AngleXU=0 Radius=1.5 StartAngle=1.5708 EndAngle=4.71239
    g8: ArcOfCircle CenterX=-49.19 CenterY=21.5 CenterZ=0 NormalX=0 NormalY=0 NormalZ=1 AngleXU=0 Radius=1.5 StartAngle=1.5708 EndAngle=4.71239
    g9: ArcOfCircle CenterX=-49.19 CenterY=15.75 CenterZ=0 NormalX=0 NormalY=0 NormalZ=1 AngleXU=0 Radius=1.5 StartAngle=1.5708 EndAngle=4.71239
    g10: ArcOfCircle CenterX=-49.19 CenterY=10 CenterZ=0 NormalX=0 NormalY=0 NormalZ=1 AngleXU=0 Radius=1.5 StartAngle=1.5708 EndAngle=4.71239
    g11: ArcOfCircle CenterX=-49.19 CenterY=4.25 CenterZ=0 NormalX=0 NormalY=0 NormalZ=1 AngleXU=0 Radius=1.5 StartAngle=1.5708 EndAngle=4.71239
    g12: LineSegment StartX=-49.19 StartY=69.25 StartZ=0 EndX=-49.19 EndY=66.25 EndZ=0
    g13: LineSegment StartX=-49.19 StartY=63.5 StartZ=0 EndX=-49.19 EndY=60.5 EndZ=0
    g14: LineSegment StartX=-49.19 StartY=57.75 StartZ=0 EndX=-49.19 EndY=54.75 EndZ=0
    g15: LineSegment StartX=-49.19 StartY=52 StartZ=0 EndX=-49.19 EndY=49 EndZ=0
    g16: LineSegment StartX=-49.19 StartY=46.25 StartZ=0 EndX=-49.19 EndY=43.25 EndZ=0
    g17: LineSegment StartX=-49.19 StartY=40.5 StartZ=0 EndX=-49.19 EndY=37.5 EndZ=0
    g18: LineSegment StartX=-49.19 StartY=34.5 StartZ=0 EndX=-49.19 EndY=31.5 EndZ=0
    g19: LineSegment StartX=-49.19 StartY=28.75 StartZ=0 EndX=-49.19 EndY=25.75 EndZ=0
    g20: LineSegment StartX=-49.19 StartY=23 StartZ=0 EndX=-49.19 EndY=20 EndZ=0
    g21: LineSegment StartX=-49.19 StartY=17.25 StartZ=0 EndX=-49.19 EndY=14.25 EndZ=0
    g22: LineSegment StartX=-49.19 StartY=11.5 StartZ=0 EndX=-49.19 EndY=8.5 EndZ=0
    g23: LineSegment StartX=-49.19 StartY=5.75 StartZ=0 EndX=-49.19 EndY=2.75 EndZ=0
  constraints (48):
    c: Block(g0)
    c: Block(g1)
    c: Block(g2)
    c: Block(g3)
    c: Block(g4)
    c: Block(g5)
    c: Block(g6)
    c: Block(g7)
    c: Block(g8)
    c: Block(g9)
    c: Block(g10)
    c: Block(g11)
    c: Coincident(g12,g0)
    c: Coincident(g12,g0)
    c: Vertical(g12)
    c: Vertical(g13)
    c: Coincident(g13,g1)
    c: Vertical(g14)
    c: Coincident(g14,g2)
    c: Vertical(g15)
    c: Coincident(g15,g3)
    c: Vertical(g16)
    c: Coincident(g16,g4)
    c: Vertical(g17)
    c: Coincident(g17,g5)
    c: Vertical(g18)
    c: Coincident(g18,g6)
    c: Vertical(g19)
    c: Coincident(g19,g7)
    c: Vertical(g20)
    c: Coincident(g20,g8)
    c: Vertical(g21)
    c: Coincident(g21,g9)
    c: Vertical(g22)
    c: Coincident(g22,g10)
    c: Vertical(g23)
    c: Coincident(g23,g11)
    c: Block(g23)
    c: Block(g22)
    c: Block(g21)
    c: Block(g20)
    c: Block(g13)
    c: Block(g14)
    c: Block(g15)
    c: Block(g16)
    c: Block(g17)
    c: Block(g18)
    c: Block(g19)
FEATURE [Part::Extrusion] Extrude022
  Base = -> Sketch030
  Dir = (1,-2e-16,2e-16)
  DirMode = 2
  FaceMakerClass = Part::FaceMakerBullseye
  LengthFwd = 19
  LengthRev = 0
  Placement = pos=(-19,0,0) rot=(0,0,1;0rad)
  Solid = true
  Symmetric = false
FEATURE [Part::Fillet] Fillet022
  Base = -> Extrude022
  Edges = 24 edges r=1.49: [Edge6,Edge11,Edge18,Edge23,Edge30,Edge35,Edge42,Edge47,Edge54,Edge59,Edge66,Edge71,Edge78,Edge83,Edge90,Edge95,Edge102,Edge107,Edge114,Edge119,Edge126,Edge131,Edge138,Edge143]
FEATURE [Part::Cut] Cut020  label="top010"
  Base = -> Cut019
  Tool = -> Fillet022
FEATURE [Sketcher::SketchObject] Sketch032
  FullyConstrained = true
  Placement = pos=(117,19,0) rot=(0.57735,0.57735,0.57735;2.0944rad)
  sketch-geometry (48):
    g0: LineSegment StartX=-49.19 StartY=69.25 StartZ=0 EndX=-49.19 EndY=66.25 EndZ=0
    g1: LineSegment StartX=-49.19 StartY=63.5 StartZ=0 EndX=-49.19 EndY=60.5 EndZ=0
    g2: LineSegment StartX=-49.19 StartY=57.75 StartZ=0 EndX=-49.19 EndY=54.75 EndZ=0
    g3: LineSegment StartX=-49.19 StartY=52 StartZ=0 EndX=-49.19 EndY=49 EndZ=0
    g4: LineSegment StartX=-49.19 StartY=46.25 StartZ=0 EndX=-49.19 EndY=43.25 EndZ=0
    g5: LineSegment StartX=-49.19 StartY=40.5 StartZ=0 EndX=-49.19 EndY=37.5 EndZ=0
    g6: LineSegment StartX=-49.19 StartY=34.5 StartZ=0 EndX=-49.19 EndY=31.5 EndZ=0
    g7: LineSegment StartX=-49.19 StartY=28.75 StartZ=0 EndX=-49.19 EndY=25.75 EndZ=0
    g8: LineSegment StartX=-49.19 StartY=23 StartZ=0 EndX=-49.19 EndY=20 EndZ=0
    g9: LineSegment StartX=-49.19 StartY=17.25 StartZ=0 EndX=-49.19 EndY=14.25 EndZ=0
    g10: LineSegment StartX=-49.19 StartY=11.5 StartZ=0 EndX=-49.19 EndY=8.5 EndZ=0
    g11: LineSegment StartX=-49.19 StartY=5.75 StartZ=0 EndX=-49.19 EndY=2.75 EndZ=0
    g12: ArcOfCircle CenterX=-1.5 CenterY=67.75 CenterZ=0 NormalX=0 NormalY=0 NormalZ=1 AngleXU=0 Radius=1.5 StartAngle=4.71239 EndAngle=7.85398
    g13: ArcOfCircle CenterX=-1.5 CenterY=62 CenterZ=0 NormalX=0 NormalY=0 NormalZ=1 AngleXU=0 Radius=1.5 StartAngle=4.71239 EndAngle=7.85398
    g14: ArcOfCircle CenterX=-1.5 CenterY=56.25 CenterZ=0 NormalX=0 NormalY=0 NormalZ=1 AngleXU=0 Radius=1.5 StartAngle=4.71239 EndAngle=7.85398
    g15: ArcOfCircle CenterX=-11.49 CenterY=50.5 CenterZ=0 NormalX=0 NormalY=0 NormalZ=1 AngleXU=0 Radius=1.5 StartAngle=4.71239 EndAngle=7.85398
    g16: ArcOfCircle CenterX=-16.28 CenterY=44.75 CenterZ=0 NormalX=0 NormalY=0 NormalZ=1 AngleXU=0 Radius=1.5 StartAngle=4.71239 EndAngle=7.85398
    g17: ArcOfCircle CenterX=-18.2337 CenterY=39 CenterZ=0 NormalX=0 NormalY=0 NormalZ=1 AngleXU=0 Radius=1.5 StartAngle=4.71485 EndAngle=7.85398
    g18: ArcOfCircle CenterX=-16.2837 CenterY=27.25 CenterZ=0 NormalX=0 NormalY=0 NormalZ=1 AngleXU=0 Radius=1.5 StartAngle=4.71485 EndAngle=7.85398
    g19: ArcOfCircle CenterX=-18.2337 CenterY=33 CenterZ=0 NormalX=0 NormalY=0 NormalZ=1 AngleXU=0 Radius=1.5 StartAngle=4.71485 EndAngle=7.85398
    g20: ArcOfCircle CenterX=-11.49 CenterY=21.5 CenterZ=0 NormalX=0 NormalY=0 NormalZ=1 AngleXU=0 Radius=1.5 StartAngle=4.71239 EndAngle=7.85398
    g21: ArcOfCircle CenterX=-1.5 CenterY=4.25 CenterZ=0 NormalX=0 NormalY=0 NormalZ=1 AngleXU=0 Radius=1.5 StartAngle=4.71239 EndAngle=7.85398
    g22: ArcOfCircle CenterX=-1.5 CenterY=10 CenterZ=0 NormalX=0 NormalY=0 NormalZ=1 AngleXU=0 Radius=1.5 StartAngle=4.71239 EndAngle=7.85398
    g23: ArcOfCircle CenterX=-1.5 CenterY=15.75 CenterZ=0 NormalX=0 NormalY=0 NormalZ=1 AngleXU=0 Radius=1.5 StartAngle=4.71239 EndAngle=7.85398
    g24: LineSegment StartX=-49.19 StartY=69.25 StartZ=0 EndX=-1.5 EndY=69.25 EndZ=0
    g25: LineSegment StartX=-49.19 StartY=66.25 StartZ=0 EndX=-1.5 EndY=66.25 EndZ=0
    g26: LineSegment StartX=-49.19 StartY=63.5 StartZ=0 EndX=-1.5 EndY=63.5 EndZ=0
    g27: LineSegment StartX=-49.19 StartY=60.5 StartZ=0 EndX=-1.5 EndY=60.5 EndZ=0
    g28: LineSegment StartX=-49.19 StartY=57.75 StartZ=0 EndX=-1.5 EndY=57.75 EndZ=0
    g29: LineSegment StartX=-49.19 StartY=54.75 StartZ=0 EndX=-1.5 EndY=54.75 EndZ=0
    g30: LineSegment StartX=-49.19 StartY=52 StartZ=0 EndX=-11.49 EndY=52 EndZ=0
    g31: LineSegment StartX=-49.19 StartY=49 StartZ=0 EndX=-11.49 EndY=49 EndZ=0
    g32: LineSegment StartX=-49.19 StartY=46.25 StartZ=0 EndX=-16.28 EndY=46.25 EndZ=0
    g33: LineSegment StartX=-49.19 StartY=43.25 StartZ=0 EndX=-16.28 EndY=43.25 EndZ=0
    g34: LineSegment StartX=-49.19 StartY=40.5 StartZ=0 EndX=-18.2337 EndY=40.5 EndZ=0
    g35: LineSegment StartX=-49.19 StartY=37.5 StartZ=0 EndX=-18.23 EndY=37.5 EndZ=0
    g36: LineSegment StartX=-49.19 StartY=34.5 StartZ=0 EndX=-18.2337 EndY=34.5 EndZ=0
    g37: LineSegment StartX=-49.19 StartY=31.5 StartZ=0 EndX=-18.23 EndY=31.5 EndZ=0
    g38: LineSegment StartX=-49.19 StartY=28.75 StartZ=0 EndX=-16.2837 EndY=28.75 EndZ=0
    g39: LineSegment StartX=-49.19 StartY=25.75 StartZ=0 EndX=-16.28 EndY=25.75 EndZ=0
    g40: LineSegment StartX=-49.19 StartY=23 StartZ=0 EndX=-11.49 EndY=23 EndZ=0
    g41: LineSegment StartX=-49.19 StartY=20 StartZ=0 EndX=-11.49 EndY=20 EndZ=0
    g42: LineSegment StartX=-49.19 StartY=17.25 StartZ=0 EndX=-1.5 EndY=17.25 EndZ=0
    g43: LineSegment StartX=-49.19 StartY=14.25 StartZ=0 EndX=-1.5 EndY=14.25 EndZ=0
    g44: LineSegment StartX=-49.19 StartY=11.5 StartZ=0 EndX=-1.5 EndY=11.5 EndZ=0
    g45: LineSegment StartX=-49.19 StartY=8.5 StartZ=0 EndX=-1.5 EndY=8.5 EndZ=0
    g46: LineSegment StartX=-49.19 StartY=5.75 StartZ=0 EndX=-1.5 EndY=5.75 EndZ=0
    g47: LineSegment StartX=-49.19 StartY=2.75 StartZ=0 EndX=-1.5 EndY=2.75 EndZ=0
  constraints (120):
    c: Vertical(g0)
    c: Distance(g0) = 3
    c: Block(g0)
    c: Vertical(g1)
    c: Distance(g1) = 3
    c: Vertical(g2)
    c: Equal(g0,g2) = 3
    c: Block(g2)
    c: Vertical(g3)
    c: Equal(g1,g3) = 3
    c: Vertical(g4)
    c: Equal(g0,g4) = 3
    c: Block(g4)
    c: Vertical(g5)
    c: Equal(g1,g5) = 3
    c: Vertical(g6)
    c: Equal(g0,g6) = 3
    c: Block(g6)
    c: Vertical(g7)
    c: Equal(g1,g7) = 3
    c: Vertical(g8)
    c: Equal(g0,g8) = 3
    c: Block(g8)
    c: Vertical(g9)
    c: Equal(g1,g9) = 3
    c: Vertical(g10)
    c: Equal(g0,g10) = 3
    c: Block(g10)
    c: Vertical(g11)
    c: Equal(g1,g11) = 3
    c: Block(g12)
    c: Block(g13)
    c: Block(g14)
    c: Block(g15)
    c: Block(g16)
    c: Block(g17)
    c: Block(g18)
    c: Block(g19)
    c: Block(g20)
    c: Block(g21)
    c: Block(g22)
    c: Block(g23)
    c: Block(g11)
    c: Block(g9)
    c: Block(g7)
    c: Block(g5)
    c: Block(g3)
    c: Block(g1)
    c: Coincident(g24,g0)
    c: Coincident(g24,g12)
    c: Horizontal(g24)
    c: Coincident(g25,g0)
    c: Coincident(g25,g12)
    c: Horizontal(g25)
    c: Coincident(g26,g1)
    c: Coincident(g26,g13)
    c: Horizontal(g26)
    c: Coincident(g27,g1)
    c: Coincident(g27,g13)
    c: Horizontal(g27)
    c: Coincident(g28,g2)
    c: Coincident(g28,g14)
    c: Horizontal(g28)
    c: Coincident(g29,g2)
    c: Coincident(g29,g14)
    c: Horizontal(g29)
    c: Coincident(g30,g3)
    c: Coincident(g30,g15)
    c: Horizontal(g30)
    c: Coincident(g31,g3)
    c: Coincident(g31,g15)
    c: Horizontal(g31)
    c: Coincident(g32,g4)
    c: Coincident(g32,g16)
    c: Horizontal(g32)
    c: Coincident(g33,g4)
    c: Coincident(g33,g16)
    c: Horizontal(g33)
    c: Coincident(g34,g5)
    c: Coincident(g34,g17)
    c: Horizontal(g34)
    c: Coincident(g35,g5)
    c: Coincident(g35,g17)
    c: Horizontal(g35)
    c: Coincident(g36,g6)
    c: Coincident(g36,g19)
    c: Horizontal(g36)
    c: Coincident(g37,g6)
    c: Coincident(g37,g19)
    c: Horizontal(g37)
    c: Coincident(g38,g7)
    c: Coincident(g38,g18)
    c: Horizontal(g38)
    c: Coincident(g39,g7)
    c: Coincident(g39,g18)
    c: Horizontal(g39)
    c: Coincident(g40,g8)
    c: Coincident(g40,g20)
    c: Horizontal(g40)
    c: Coincident(g41,g8)
    c: Coincident(g41,g20)
    c: Horizontal(g41)
    c: Coincident(g42,g9)
    c: Coincident(g42,g23)
    c: Horizontal(g42)
    c: Coincident(g43,g9)
    c: Coincident(g43,g23)
    c: Horizontal(g43)
    c: Coincident(g44,g10)
    c: Coincident(g44,g22)
    c: Horizontal(g44)
    c: Coincident(g45,g10)
    c: Coincident(g45,g22)
    c: Horizontal(g45)
    c: Coincident(g46,g11)
    c: Coincident(g46,g21)
    c: Horizontal(g46)
    c: Coincident(g47,g11)
    c: Coincident(g47,g21)
    c: Horizontal(g47)
FEATURE [Part::Extrusion] Extrude023
  Base = -> Sketch032
  Dir = (1,-2e-16,2e-16)
  DirMode = 2
  FaceMakerClass = Part::FaceMakerBullseye
  LengthFwd = 19
  LengthRev = 0
  Placement = pos=(-19,0,0) rot=(0,0,1;0rad)
  Solid = true
  Symmetric = false
FEATURE [Part::Fillet] Fillet023
  Base = -> Extrude023
  Edges = <same value as first occurrence — deduplicated (x4 in doc)>
  Placement = pos=(0,0.05,0) rot=(0,0,1;0rad)
FEATURE [Part::Cut] Cut014  label="bottom003"
  Base = -> Cut007
  Tool = -> Fusion047
FEATURE [Part::Cut] Cut021  label="bottom004"
  Base = -> Cut014
  Tool = -> Fillet023
FEATURE [Sketcher::SketchObject] Sketch033
  FullyConstrained = true
  Placement = pos=(117,19,0) rot=(0.57735,0.57735,0.57735;2.0944rad)
  sketch-geometry (8):
    g0: LineSegment StartX=-49.19 StartY=69.25 StartZ=0 EndX=-49.19 EndY=66.25 EndZ=0
    g1: LineSegment StartX=-49.19 StartY=5.75 StartZ=0 EndX=-49.19 EndY=2.75 EndZ=0
    g2: ArcOfCircle CenterX=-1.5 CenterY=67.75 CenterZ=0 NormalX=0 NormalY=0 NormalZ=1 AngleXU=0 Radius=1.5 StartAngle=4.71239 EndAngle=7.85398
    g3: ArcOfCircle CenterX=-1.5 CenterY=4.25 CenterZ=0 NormalX=0 NormalY=0 NormalZ=1 AngleXU=0 Radius=1.5 StartAngle=4.71239 EndAngle=7.85398
    g4: LineSegment StartX=-49.19 StartY=69.25 StartZ=0 EndX=-1.5 EndY=69.25 EndZ=0
    g5: LineSegment StartX=-49.19 StartY=66.25 StartZ=0 EndX=-1.5 EndY=66.25 EndZ=0
    g6: LineSegment StartX=-49.19 StartY=5.75 StartZ=0 EndX=-1.5 EndY=5.75 EndZ=0
    g7: LineSegment StartX=-49.19 StartY=2.75 StartZ=0 EndX=-1.5 EndY=2.75 EndZ=0
  constraints (19):
    c: Vertical(g0)
    c: Distance(g0) = 3
    c: Block(g0)
    c: Vertical(g1)
    c: Block(g2)
    c: Block(g3)
    c: Block(g1)
    c: Coincident(g4,g0)
    c: Coincident(g4,g2)
    c: Horizontal(g4)
    c: Coincident(g5,g0)
    c: Coincident(g5,g2)
    c: Horizontal(g5)
    c: Coincident(g6,g1)
    c: Coincident(g6,g3)
    c: Horizontal(g6)
    c: Coincident(g7,g1)
    c: Coincident(g7,g3)
    c: Horizontal(g7)
FEATURE [Sketcher::SketchObject] Sketch034
  FullyConstrained = true
  Placement = pos=(117,19,0) rot=(0.57735,0.57735,0.57735;2.0944rad)
  sketch-geometry (8):
    g0: LineSegment StartX=-49.19 StartY=63.5 StartZ=0 EndX=-49.19 EndY=60.5 EndZ=0
    g1: LineSegment StartX=-49.19 StartY=11.5 StartZ=0 EndX=-49.19 EndY=8.5 EndZ=0
    g2: ArcOfCircle CenterX=-1.5 CenterY=62 CenterZ=0 NormalX=0 NormalY=0 NormalZ=1 AngleXU=0 Radius=1.5 StartAngle=4.71239 EndAngle=7.85398
    g3: ArcOfCircle CenterX=-1.5 CenterY=10 CenterZ=0 NormalX=0 NormalY=0 NormalZ=1 AngleXU=0 Radius=1.5 StartAngle=4.71239 EndAngle=7.85398
    g4: LineSegment StartX=-49.19 StartY=63.5 StartZ=0 EndX=-1.5 EndY=63.5 EndZ=0
    g5: LineSegment StartX=-49.19 StartY=60.5 StartZ=0 EndX=-1.5 EndY=60.5 EndZ=0
    g6: LineSegment StartX=-49.19 StartY=11.5 StartZ=0 EndX=-1.5 EndY=11.5 EndZ=0
    g7: LineSegment StartX=-49.19 StartY=8.5 StartZ=0 EndX=-1.5 EndY=8.5 EndZ=0
  constraints (19):
    c: Vertical(g0)
    c: Distance(g0) = 3
    c: Vertical(g1)
    c: Block(g1)
    c: Block(g2)
    c: Block(g3)
    c: Block(g0)
    c: Coincident(g4,g0)
    c: Coincident(g4,g2)
    c: Horizontal(g4)
    c: Coincident(g5,g0)
    c: Coincident(g5,g2)
    c: Horizontal(g5)
    c: Coincident(g6,g1)
    c: Coincident(g6,g3)
    c: Horizontal(g6)
    c: Coincident(g7,g1)
    c: Coincident(g7,g3)
    c: Horizontal(g7)
FEATURE [Part::Extrusion] Extrude024
  Base = -> Sketch033
  Dir = (1,0,0)
  DirMode = 2
  FaceMakerClass = Part::FaceMakerBullseye
  LengthFwd = 10
  LengthRev = 0
  Solid = true
  Symmetric = false
FEATURE [Part::Extrusion] Extrude025
  Base = -> Sketch034
  Dir = (1,0,0)
  DirMode = 2
  FaceMakerClass = Part::FaceMakerBullseye
  LengthFwd = 10
  LengthRev = 0
  Solid = true
  Symmetric = false
FEATURE [Part::Fillet] Fillet024  label="removeFromtMoreFrontCaseScrewRetainers"
  Base = -> Extrude024
  Edges = 4 edges r=1.49: [Edge6,Edge11,Edge18,Edge23]
  Placement = pos=(-11,0,0) rot=(0,0,1;0rad)
FEATURE [Part::Fillet] Fillet025  label="removeFromtMoreFrontCaseScrewRetainers001"
  Base = -> Extrude025
  Edges = 4 edges r=1.49: [Edge6,Edge11,Edge18,Edge23]
  Placement = pos=(-19,0,0) rot=(0,0,1;0rad)
FEATURE [Part::Cut] Cut022
  Base = -> Cut015
  Tool = -> Fillet025
FEATURE [Part::Cut] Cut023  label="screwRetainers"
  Base = -> Cut022
  Tool = -> Fillet024
FEATURE [Part::MultiFuse] Fusion056  label="bottom005"
  Shapes = -> [Fusion044,Cut021]
FEATURE [Part::MultiFuse] Fusion057  label="casePillars001"
  Shapes = -> [Cut016,Fusion052]
FEATURE [Part::MultiFuse] Fusion058  label="bottom006"
  Shapes = -> [Fusion056,Cut023]
FEATURE [Part::MultiFuse] Fusion059  label="bottom007"
  Shapes = -> [Fusion058,Fillet005]
FEATURE [Part::MultiFuse] Fusion060  label="bottom008"
  Shapes = -> [Fusion059,Fusion]
FEATURE [Part::MultiFuse] Fusion061  label="top011"
  Shapes = -> [Cut006,Cut020]
FEATURE [Part::MultiFuse] Fusion062  label="top012"
  Shapes = -> [Fusion057,Fusion061]
FEATURE [Sketcher::SketchObject] Sketch035  label="topSketch007"
  FullyConstrained = true
  sketch-geometry (6):
    g0: LineSegment StartX=19 StartY=38 StartZ=0 EndX=117 EndY=38 EndZ=0
    g1: ArcOfCircle CenterX=19 CenterY=19 CenterZ=0 NormalX=0 NormalY=0 NormalZ=1 AngleXU=0 Radius=19 StartAngle=1.5708 EndAngle=3.14159
    g2: LineSegment StartX=117 StartY=38 StartZ=0 EndX=117 EndY=19 EndZ=0
    g3: LineSegment StartX=98 StartY=1.0161e-12 StartZ=0 EndX=5.22862e-06 EndY=1.0161e-12 EndZ=0
    g4: LineSegment StartX=5.22862e-06 StartY=19 StartZ=0 EndX=5.22862e-06 EndY=1.0161e-12 EndZ=0
    g5: ArcOfCircle CenterX=98 CenterY=19 CenterZ=0 NormalX=0 NormalY=0 NormalZ=1 AngleXU=0 Radius=19 StartAngle=4.71239 EndAngle=6.28319
  constraints (16):
    c: Horizontal(g0)
    c: Distance(g0) = 98
    c: Coincident(g1,g0)
    c: Block(g1)
    c: Coincident(g2,g0)
    c: Vertical(g2)
    c: Distance(g2) = 19
    c: Horizontal(g3)
    c: Coincident(g4,g1)
    c: Vertical(g4)
    c: Coincident(g3,g4)
    c: Block(g3)
    c: Coincident(g5,g2)
    c: Coincident(g5,g3)
    c: Block(g0)
    c: Block(g5)
FEATURE [Part::Extrusion] Extrude026  label="sideA001"
  Base = -> Sketch035
  Dir = (0,0,1)
  DirMode = 2
  FaceMakerClass = Part::FaceMakerBullseye
  LengthFwd = 3
  LengthRev = 0
  Placement = pos=(0,0,-2.7) rot=(0,0,1;0rad)
  Solid = true
  Symmetric = false
FEATURE [Sketcher::SketchObject] Sketch036  label="topSketch008"
  FullyConstrained = true
  sketch-geometry (6):
    g0: LineSegment StartX=19 StartY=38 StartZ=0 EndX=117 EndY=38 EndZ=0
    g1: ArcOfCircle CenterX=19 CenterY=19 CenterZ=0 NormalX=0 NormalY=0 NormalZ=1 AngleXU=0 Radius=19 StartAngle=1.5708 EndAngle=3.14159
    g2: LineSegment StartX=117 StartY=38 StartZ=0 EndX=117 EndY=19 EndZ=0
    g3: LineSegment StartX=98 StartY=1.0161e-12 StartZ=0 EndX=5.22862e-06 EndY=1.0161e-12 EndZ=0
    g4: LineSegment StartX=5.22862e-06 StartY=19 StartZ=0 EndX=5.22862e-06 EndY=1.0161e-12 EndZ=0
    g5: ArcOfCircle CenterX=98 CenterY=19 CenterZ=0 NormalX=0 NormalY=0 NormalZ=1 AngleXU=0 Radius=19 StartAngle=4.71239 EndAngle=6.28319
  constraints (16):
    c: Horizontal(g0)
    c: Distance(g0) = 98
    c: Coincident(g1,g0)
    c: Block(g1)
    c: Coincident(g2,g0)
    c: Vertical(g2)
    c: Distance(g2) = 19
    c: Horizontal(g3)
    c: Coincident(g4,g1)
    c: Vertical(g4)
    c: Coincident(g3,g4)
    c: Block(g3)
    c: Coincident(g5,g2)
    c: Coincident(g5,g3)
    c: Block(g0)
    c: Block(g5)
FEATURE [Part::Extrusion] Extrude027  label="sideB001"
  Base = -> Sketch036
  Dir = (0,0,1)
  DirMode = 2
  FaceMakerClass = Part::FaceMakerBullseye
  LengthFwd = 3
  LengthRev = 0
  Placement = pos=(0,0,71.7) rot=(0,0,1;0rad)
  Solid = true
  Symmetric = false
FEATURE [Part::MultiFuse] Fusion064  label="removeFromBottom"
  Shapes = -> [Extrude026,Extrude027]
FEATURE [Part::Cut] Cut024  label="bottom009"
  Base = -> Fusion060
  Tool = -> Fusion064
FEATURE [Sketcher::SketchObject] Sketch037  label="topSketch009"
  FullyConstrained = true
  sketch-geometry (6):
    g0: ArcOfCircle CenterX=19 CenterY=19 CenterZ=0 NormalX=0 NormalY=0 NormalZ=1 AngleXU=0 Radius=19 StartAngle=1.5708 EndAngle=3.14159
    g1: LineSegment StartX=5.22862e-06 StartY=19 StartZ=0 EndX=5.22862e-06 EndY=1.19904e-11 EndZ=0
    g2: LineSegment StartX=19 StartY=38 StartZ=0 EndX=124 EndY=38 EndZ=0
    g3: LineSegment StartX=5.22862e-06 StartY=1.19904e-11 StartZ=0 EndX=105 EndY=1.19904e-11 EndZ=0
    g4: ArcOfCircle CenterX=105 CenterY=19 CenterZ=0 NormalX=0 NormalY=0 NormalZ=1 AngleXU=0 Radius=19 StartAngle=4.71239 EndAngle=6.28319
    g5: LineSegment StartX=124 StartY=38 StartZ=0 EndX=124 EndY=19 EndZ=0
  constraints (16):
    c: Block(g0)
    c: Coincident(g1,g0)
    c: Vertical(g1)
    c: Horizontal(g2)
    c: Distance(g2) = 105
    c: Coincident(g2,g0)
    c: Distance(g1) = 19
    c: Coincident(g3,g1)
    c: Horizontal(g3)
    c: Distance(g3) = 105
    c: Block(g4)
    c: Coincident(g4,g3)
    c: Coincident(g5,g2)
    c: Coincident(g5,g4)
    c: Vertical(g5)
    c: Distance(g5) = 19
FEATURE [Part::Extrusion] Extrude028  label="sideB"
  Base = -> Sketch037
  Dir = (0,0,1)
  DirMode = 2
  FaceMakerClass = Part::FaceMakerBullseye
  LengthFwd = 3
  LengthRev = 0
  Placement = pos=(0,0,72) rot=(0,0,1;0rad)
  Solid = true
  Symmetric = false
FEATURE [Sketcher::SketchObject] Sketch038  label="topSketch010"
  FullyConstrained = true
  sketch-geometry (22):
    g0: LineSegment StartX=5.21097e-06 StartY=3 StartZ=0 EndX=5.21097e-06 EndY=19 EndZ=0
    g1: ArcOfCircle CenterX=19 CenterY=19 CenterZ=0 NormalX=0 NormalY=0 NormalZ=1 AngleXU=0 Radius=19 StartAngle=1.5708 EndAngle=3.14159
    g2: ArcOfCircle CenterX=19 CenterY=19 CenterZ=0 NormalX=0 NormalY=0 NormalZ=1 AngleXU=0 Radius=16 StartAngle=1.5708 EndAngle=3.14159
    g3: LineSegment StartX=114 StartY=35 StartZ=0 EndX=19 EndY=35 EndZ=0
    g4: LineSegment StartX=5.21097e-06 StartY=3 StartZ=0 EndX=5.21097e-06 EndY=0 EndZ=0
    g5: LineSegment StartX=3 StartY=0 StartZ=0 EndX=5.21097e-06 EndY=0 EndZ=0
    g6: LineSegment StartX=3 StartY=19 StartZ=0 EndX=3 EndY=0 EndZ=0
    g7: LineSegment StartX=19 StartY=38 StartZ=0 EndX=124 EndY=38 EndZ=0
    g8: Circle CenterX=119 CenterY=35 CenterZ=0 NormalX=0 NormalY=0 NormalZ=1 AngleXU=0 Radius=1
    g9: Circle CenterX=121 CenterY=35 CenterZ=0 NormalX=0 NormalY=0 NormalZ=1 AngleXU=0 Radius=1
    g10: Circle CenterX=121 CenterY=33 CenterZ=0 NormalX=0 NormalY=0 NormalZ=1 AngleXU=0 Radius=1
    g11: BSplineCurve PolesCount=3 KnotsCount=2 Degree=2 IsPeriodic=0
    g12: GeomPoint X=119 Y=35 Z=0
    g13: GeomPoint X=121 Y=33 Z=0
    g14: LineSegment StartX=119 StartY=35 StartZ=0 EndX=114 EndY=35 EndZ=0
    g15: ArcOfCircle CenterX=105 CenterY=19 CenterZ=0 NormalX=0 NormalY=0 NormalZ=1 AngleXU=0 Radius=16 StartAngle=5.60905 EndAngle=6.28319
    g16: LineSegment StartX=121 StartY=33 StartZ=0 EndX=121 EndY=19 EndZ=0
    g17: LineSegment StartX=117.5 StartY=9.01251 StartZ=0 EndX=121.163 EndY=9.0125 EndZ=0
    g18: ArcOfCircle CenterX=105 CenterY=19 CenterZ=0 NormalX=0 NormalY=0 NormalZ=1 AngleXU=0 Radius=20.6155 StartAngle=5.7297 EndAngle=6.28319
    g19: LineSegment StartX=121.163 StartY=9.0125 StartZ=0 EndX=122.538 EndY=8.16329 EndZ=0
    g20: LineSegment StartX=124 StartY=38 StartZ=0 EndX=125.616 EndY=38 EndZ=0
    g21: LineSegment StartX=125.616 StartY=19 StartZ=0 EndX=125.616 EndY=38 EndZ=0
  constraints (49):
    c: Vertical(g0)
    c: Block(g0)
    c: Coincident(g1,g0)
    c: Block(g1)
    c: Coincident(g2,g1)
    c: Block(g2)
    c: Coincident(g3,g2)
    c: Horizontal(g3)
    c: Tangent(g3,g2)
    c: Coincident(g4,g0)
    c: Distance(g4) = 3
    c: Vertical(g4)
    c: Coincident(g5,g4)
    c: Horizontal(g5)
    c: Coincident(g6,g2)
    c: Coincident(g6,g5)
    c: Vertical(g6)
    c: Horizontal(g7)
    c: Distance(g7) = 105
    c: Coincident(g7,g1)
    c: Block(g3)
    c: Weight(g8) = 1
    c: Equal(g8,g9)
    c: Equal(g8,g10)
    c: InternalAlignment(g8,g11)
    c: InternalAlignment(g9,g11)
    c: InternalAlignment(g10,g11)
    c: InternalAlignment(g12,g11)
    c: InternalAlignment(g13,g11)
    c: Block(g11)
    c: Coincident(g14,g11)
    c: Coincident(g14,g3)
    c: Horizontal(g14)
    c: Block(g15)
    c: Coincident(g16,g11)
    c: Coincident(g16,g15)
    c: Vertical(g16)
    c: Distance(g16) = 14
    c: Coincident(g17,g15)
    c: Block(g18)
    c: Coincident(g19,g18)
    c: Coincident(g20,g7)
    c: Horizontal(g20)
    c: Vertical(g21)
    c: Coincident(g20,g21)
    c: Block(g20)
    c: Block(g21)
    c: Block(g19)
    c: Block(g17)
FEATURE [Part::Extrusion] Extrude029
  Base = -> Sketch038
  Dir = (0,0,1)
  DirMode = 2
  FaceMakerClass = Part::FaceMakerBullseye
  LengthFwd = 72
  LengthRev = 0
  Solid = true
  Symmetric = false
FEATURE [Part::Feature] Face085
  shape: bbox 4.8 x 25.5 x 2e-07 mm, 1 faces, 0 solids (baked)
FEATURE [Part::Revolution] Revolve089  label="moreFrontCaseScrewPost003"
  Angle = 360
  Axis = (0,1,0)
  Base = (0,0,0)
  FaceMakerClass = Part::FaceMakerBullseye
  Placement = pos=(109.5,4.5,3.5) rot=(0,0,1;0rad)
  Solid = false
  Source = -> Face085
  Symmetric = false
FEATURE [Part::Feature] Face086
  shape: bbox 4.8 x 25.5 x 2e-07 mm, 1 faces, 0 solids (baked)
FEATURE [Part::Revolution] Revolve090  label="moreFrontCaseScrewPost004"
  Angle = 360
  Axis = (0,1,0)
  Base = (0,0,0)
  FaceMakerClass = Part::FaceMakerBullseye
  Placement = pos=(109.5,4.5,68.5) rot=(0,0,1;0rad)
  Solid = false
  Source = -> Face086
  Symmetric = false
FEATURE [Part::Fillet] Fillet026  label="top013"
  Base = -> Extrude029
  Edges = 1 edges r=2: [Edge35]
FEATURE [Sketcher::SketchObject] Sketch039
  FullyConstrained = true
  sketch-geometry (7):
    g0: LineSegment StartX=0 StartY=0 StartZ=0 EndX=0 EndY=6 EndZ=0
    g1: Circle CenterX=0 CenterY=0 CenterZ=0 NormalX=0 NormalY=0 NormalZ=1 AngleXU=0 Radius=1
    g2: Circle CenterX=8 CenterY=6 CenterZ=0 NormalX=0 NormalY=0 NormalZ=1 AngleXU=0 Radius=1
    g3: BSplineCurve PolesCount=3 KnotsCount=2 Degree=2 IsPeriodic=0
    g4: GeomPoint X=0 Y=0 Z=0
    g5: GeomPoint X=8 Y=6 Z=0
    g6: LineSegment StartX=0 StartY=6 StartZ=0 EndX=8 EndY=6 EndZ=0
  constraints (14):
    c: Coincident(g0,g-1)
    c: Distance(g0) = 6
    c: Vertical(g0)
    c: Coincident(g3,g0)
    c: Weight(g1) = 1
    c: Equal(g1,g2)
    c: InternalAlignment(g1,g3)
    c: InternalAlignment(g2,g3)
    c: InternalAlignment(g4,g3)
    c: InternalAlignment(g5,g3)
    c: Block(g3)
    c: Coincident(g6,g0)
    c: Coincident(g6,g3)
    c: Horizontal(g6)
FEATURE [Sketcher::SketchObject] Sketch040
  FullyConstrained = true
  sketch-geometry (7):
    g0: LineSegment StartX=0 StartY=0 StartZ=0 EndX=0 EndY=6 EndZ=0
    g1: Circle CenterX=0 CenterY=0 CenterZ=0 NormalX=0 NormalY=0 NormalZ=1 AngleXU=0 Radius=1
    g2: Circle CenterX=8 CenterY=6 CenterZ=0 NormalX=0 NormalY=0 NormalZ=1 AngleXU=0 Radius=1
    g3: BSplineCurve PolesCount=3 KnotsCount=2 Degree=2 IsPeriodic=0
    g4: GeomPoint X=0 Y=0 Z=0
    g5: GeomPoint X=8 Y=6 Z=0
    g6: LineSegment StartX=0 StartY=6 StartZ=0 EndX=8 EndY=6 EndZ=0
  constraints (14):
    c: Coincident(g0,g-1)
    c: Distance(g0) = 6
    c: Vertical(g0)
    c: Coincident(g3,g0)
    c: Weight(g1) = 1
    c: Equal(g1,g2)
    c: InternalAlignment(g1,g3)
    c: InternalAlignment(g2,g3)
    c: InternalAlignment(g4,g3)
    c: InternalAlignment(g5,g3)
    c: Block(g3)
    c: Coincident(g6,g0)
    c: Coincident(g6,g3)
    c: Horizontal(g6)
FEATURE [Sketcher::SketchObject] Sketch041
  FullyConstrained = true
  sketch-geometry (7):
    g0: LineSegment StartX=0 StartY=0 StartZ=0 EndX=0 EndY=6 EndZ=0
    g1: Circle CenterX=0 CenterY=0 CenterZ=0 NormalX=0 NormalY=0 NormalZ=1 AngleXU=0 Radius=1
    g2: Circle CenterX=8 CenterY=6 CenterZ=0 NormalX=0 NormalY=0 NormalZ=1 AngleXU=0 Radius=1
    g3: BSplineCurve PolesCount=3 KnotsCount=2 Degree=2 IsPeriodic=0
    g4: GeomPoint X=0 Y=0 Z=0
    g5: GeomPoint X=8 Y=6 Z=0
    g6: LineSegment StartX=0 StartY=6 StartZ=0 EndX=8 EndY=6 EndZ=0
  constraints (14):
    c: Coincident(g0,g-1)
    c: Distance(g0) = 6
    c: Vertical(g0)
    c: Coincident(g3,g0)
    c: Weight(g1) = 1
    c: Equal(g1,g2)
    c: InternalAlignment(g1,g3)
    c: InternalAlignment(g2,g3)
    c: InternalAlignment(g4,g3)
    c: InternalAlignment(g5,g3)
    c: Block(g3)
    c: Coincident(g6,g0)
    c: Coincident(g6,g3)
    c: Horizontal(g6)
FEATURE [Sketcher::SketchObject] Sketch042
  FullyConstrained = true
  sketch-geometry (7):
    g0: LineSegment StartX=0 StartY=0 StartZ=0 EndX=0 EndY=6 EndZ=0
    g1: Circle CenterX=0 CenterY=0 CenterZ=0 NormalX=0 NormalY=0 NormalZ=1 AngleXU=0 Radius=1
    g2: Circle CenterX=8 CenterY=6 CenterZ=0 NormalX=0 NormalY=0 NormalZ=1 AngleXU=0 Radius=1
    g3: BSplineCurve PolesCount=3 KnotsCount=2 Degree=2 IsPeriodic=0
    g4: GeomPoint X=0 Y=0 Z=0
    g5: GeomPoint X=8 Y=6 Z=0
    g6: LineSegment StartX=0 StartY=6 StartZ=0 EndX=8 EndY=6 EndZ=0
  constraints (14):
    c: Coincident(g0,g-1)
    c: Distance(g0) = 6
    c: Vertical(g0)
    c: Coincident(g3,g0)
    c: Weight(g1) = 1
    c: Equal(g1,g2)
    c: InternalAlignment(g1,g3)
    c: InternalAlignment(g2,g3)
    c: InternalAlignment(g4,g3)
    c: InternalAlignment(g5,g3)
    c: Block(g3)
    c: Coincident(g6,g0)
    c: Coincident(g6,g3)
    c: Horizontal(g6)
FEATURE [Part::Extrusion] Extrude030  label="caseScrewPillarBracket008"
  Base = -> Sketch039
  Dir = (0,0,1)
  DirMode = 2
  FaceMakerClass = Part::FaceMakerBullseye
  LengthFwd = 2.4
  LengthRev = 0
  Placement = pos=(15.76,29,8.8) rot=(0,1,0;0rad)
  Solid = true
  Symmetric = false
FEATURE [Part::Extrusion] Extrude031  label="caseScrewPillarBracket009"
  Base = -> Sketch040
  Dir = (0,0,1)
  DirMode = 2
  FaceMakerClass = Part::FaceMakerBullseye
  LengthFwd = 2.4
  LengthRev = 0
  Placement = pos=(15.76,29,60.8) rot=(0,0,1;0rad)
  Solid = true
  Symmetric = false
FEATURE [Part::Extrusion] Extrude032  label="caseScrewPillarBracket010"
  Base = -> Sketch041
  Dir = (0,0,1)
  DirMode = 2
  FaceMakerClass = Part::FaceMakerBullseye
  LengthFwd = 2.4
  LengthRev = 0
  Placement = pos=(13.7,29,13.26) rot=(0,-1,0;1.5708rad)
  Solid = true
  Symmetric = false
FEATURE [Part::Extrusion] Extrude033  label="caseScrewPillarBracket011"
  Base = -> Sketch042
  Dir = (0,0,1)
  DirMode = 2
  FaceMakerClass = Part::FaceMakerBullseye
  LengthFwd = 2.4
  LengthRev = 0
  Placement = pos=(11.3,29,58.74) rot=(0,1,0;1.5708rad)
  Solid = true
  Symmetric = false
FEATURE [Sketcher::SketchObject] Sketch043
  FullyConstrained = true
  sketch-geometry (7):
    g0: LineSegment StartX=0 StartY=0 StartZ=0 EndX=0 EndY=6 EndZ=0
    g1: Circle CenterX=0 CenterY=0 CenterZ=0 NormalX=0 NormalY=0 NormalZ=1 AngleXU=0 Radius=1
    g2: Circle CenterX=8 CenterY=6 CenterZ=0 NormalX=0 NormalY=0 NormalZ=1 AngleXU=0 Radius=1
    g3: BSplineCurve PolesCount=3 KnotsCount=2 Degree=2 IsPeriodic=0
    g4: GeomPoint X=0 Y=0 Z=0
    g5: GeomPoint X=8 Y=6 Z=0
    g6: LineSegment StartX=0 StartY=6 StartZ=0 EndX=8 EndY=6 EndZ=0
  constraints (14):
    c: Coincident(g0,g-1)
    c: Distance(g0) = 6
    c: Vertical(g0)
    c: Coincident(g3,g0)
    c: Weight(g1) = 1
    c: Equal(g1,g2)
    c: InternalAlignment(g1,g3)
    c: InternalAlignment(g2,g3)
    c: InternalAlignment(g4,g3)
    c: InternalAlignment(g5,g3)
    c: Block(g3)
    c: Coincident(g6,g0)
    c: Coincident(g6,g3)
    c: Horizontal(g6)
FEATURE [Part::Extrusion] Extrude034  label="caseScrewPillarBracket012"
  Base = -> Sketch043
  Dir = (0,0,1)
  DirMode = 2
  FaceMakerClass = Part::FaceMakerBullseye
  LengthFwd = 2.4
  LengthRev = 0
  Placement = pos=(88.3,29,65.23) rot=(0,1,0;1.5708rad)
  Solid = true
  Symmetric = false
FEATURE [Sketcher::SketchObject] Sketch044
  FullyConstrained = true
  sketch-geometry (7):
    g0: LineSegment StartX=0 StartY=0 StartZ=0 EndX=0 EndY=6 EndZ=0
    g1: Circle CenterX=0 CenterY=0 CenterZ=0 NormalX=0 NormalY=0 NormalZ=1 AngleXU=0 Radius=1
    g2: Circle CenterX=8 CenterY=6 CenterZ=0 NormalX=0 NormalY=0 NormalZ=1 AngleXU=0 Radius=1
    g3: BSplineCurve PolesCount=3 KnotsCount=2 Degree=2 IsPeriodic=0
    g4: GeomPoint X=0 Y=0 Z=0
    g5: GeomPoint X=8 Y=6 Z=0
    g6: LineSegment StartX=0 StartY=6 StartZ=0 EndX=8 EndY=6 EndZ=0
  constraints (14):
    c: Coincident(g0,g-1)
    c: Distance(g0) = 6
    c: Vertical(g0)
    c: Coincident(g3,g0)
    c: Weight(g1) = 1
    c: Equal(g1,g2)
    c: InternalAlignment(g1,g3)
    c: InternalAlignment(g2,g3)
    c: InternalAlignment(g4,g3)
    c: InternalAlignment(g5,g3)
    c: Block(g3)
    c: Coincident(g6,g0)
    c: Coincident(g6,g3)
    c: Horizontal(g6)
FEATURE [Part::Extrusion] Extrude035  label="caseScrewPillarBracket013"
  Base = -> Sketch044
  Dir = (0,0,1)
  DirMode = 2
  FaceMakerClass = Part::FaceMakerBullseye
  LengthFwd = 2.4
  LengthRev = 0
  Placement = pos=(90.7,29,6.77) rot=(0,-1,0;1.5708rad)
  Solid = true
  Symmetric = false
FEATURE [Sketcher::SketchObject] Sketch045
  FullyConstrained = true
  sketch-geometry (7):
    g0: LineSegment StartX=0 StartY=0 StartZ=0 EndX=0 EndY=6 EndZ=0
    g1: Circle CenterX=0 CenterY=0 CenterZ=0 NormalX=0 NormalY=0 NormalZ=1 AngleXU=0 Radius=1
    g2: Circle CenterX=8 CenterY=6 CenterZ=0 NormalX=0 NormalY=0 NormalZ=1 AngleXU=0 Radius=1
    g3: BSplineCurve PolesCount=3 KnotsCount=2 Degree=2 IsPeriodic=0
    g4: GeomPoint X=0 Y=0 Z=0
    g5: GeomPoint X=8 Y=6 Z=0
    g6: LineSegment StartX=0 StartY=6 StartZ=0 EndX=8 EndY=6 EndZ=0
  constraints (14):
    c: Coincident(g0,g-1)
    c: Distance(g0) = 6
    c: Vertical(g0)
    c: Coincident(g3,g0)
    c: Weight(g1) = 1
    c: Equal(g1,g2)
    c: InternalAlignment(g1,g3)
    c: InternalAlignment(g2,g3)
    c: InternalAlignment(g4,g3)
    c: InternalAlignment(g5,g3)
    c: Block(g3)
    c: Coincident(g6,g0)
    c: Coincident(g6,g3)
    c: Horizontal(g6)
FEATURE [Sketcher::SketchObject] Sketch046
  FullyConstrained = true
  sketch-geometry (7):
    g0: LineSegment StartX=0 StartY=0 StartZ=0 EndX=0 EndY=6 EndZ=0
    g1: Circle CenterX=0 CenterY=0 CenterZ=0 NormalX=0 NormalY=0 NormalZ=1 AngleXU=0 Radius=1
    g2: Circle CenterX=8 CenterY=6 CenterZ=0 NormalX=0 NormalY=0 NormalZ=1 AngleXU=0 Radius=1
    g3: BSplineCurve PolesCount=3 KnotsCount=2 Degree=2 IsPeriodic=0
    g4: GeomPoint X=0 Y=0 Z=0
    g5: GeomPoint X=8 Y=6 Z=0
    g6: LineSegment StartX=0 StartY=6 StartZ=0 EndX=8 EndY=6 EndZ=0
  constraints (14):
    c: Coincident(g0,g-1)
    c: Distance(g0) = 6
    c: Vertical(g0)
    c: Coincident(g3,g0)
    c: Weight(g1) = 1
    c: Equal(g1,g2)
    c: InternalAlignment(g1,g3)
    c: InternalAlignment(g2,g3)
    c: InternalAlignment(g4,g3)
    c: InternalAlignment(g5,g3)
    c: Block(g3)
    c: Coincident(g6,g0)
    c: Coincident(g6,g3)
    c: Horizontal(g6)
FEATURE [Part::Extrusion] Extrude036  label="caseScrewPillarBracket014"
  Base = -> Sketch045
  Dir = (0,0,1)
  DirMode = 2
  FaceMakerClass = Part::FaceMakerBullseye
  LengthFwd = 2.4
  LengthRev = 0
  Placement = pos=(110.7,29,6.77) rot=(0,-1,0;1.5708rad)
  Solid = true
  Symmetric = false
FEATURE [Part::Extrusion] Extrude037  label="caseScrewPillarBracket015"
  Base = -> Sketch046
  Dir = (0,0,1)
  DirMode = 2
  FaceMakerClass = Part::FaceMakerBullseye
  LengthFwd = 2.4
  LengthRev = 0
  Placement = pos=(108.3,29,65.23) rot=(0,1,0;1.5708rad)
  Solid = true
  Symmetric = false
FEATURE [Part::Box] Box013  label="frontCaseScrewPillarBracket002"
  AttacherType = Attacher::AttachEngine3D
  Height = 2.4
  Length = 22
  Placement = pos=(87,28,2.3) rot=(0,0,1;0rad)
  Width = 7
FEATURE [Part::Box] Box014  label="frontCaseScrewPillarBracket003"
  AttacherType = Attacher::AttachEngine3D
  Height = 2.4
  Length = 22
  Placement = pos=(87,28,67.3) rot=(0,0,1;0rad)
  Width = 7
FEATURE [Part::Feature] Face087
  shape: bbox 4.8 x 30.2 x 2e-07 mm, 1 faces, 0 solids (baked)
FEATURE [Part::Revolution] Revolve091  label="frontCaseScrewPost004"
  Angle = 360
  Axis = (0,1,0)
  Base = (0,0,0)
  FaceMakerClass = Part::FaceMakerBullseye
  Placement = pos=(89.5,4.5,3.5) rot=(0,0,1;0rad)
  Solid = false
  Source = -> Face087
  Symmetric = false
FEATURE [Part::Feature] Face088
  shape: bbox 4.8 x 30.2 x 2e-07 mm, 1 faces, 0 solids (baked)
FEATURE [Part::Revolution] Revolve092  label="frontCaseScrewPost005"
  Angle = 360
  Axis = (0,1,0)
  Base = (0,0,0)
  FaceMakerClass = Part::FaceMakerBullseye
  Placement = pos=(89.5,4.5,68.5) rot=(0,0,1;0rad)
  Solid = false
  Source = -> Face088
  Symmetric = false
FEATURE [Part::Feature] Face089
  shape: bbox 3.5 x 30.2 x 2e-07 mm, 1 faces, 0 solids (baked)
FEATURE [Part::Revolution] Revolve093  label="backCaseScrewPost002"
  Angle = 360
  Axis = (0,1,0)
  Base = (0,0,0)
  FaceMakerClass = Part::FaceMakerBullseye
  Placement = pos=(12.5,4.5,10) rot=(0,0,1;0rad)
  Solid = false
  Source = -> Face089
  Symmetric = false
FEATURE [Part::Feature] Face090
  shape: bbox 3.5 x 30.2 x 2e-07 mm, 1 faces, 0 solids (baked)
FEATURE [Part::Revolution] Revolve094  label="backCaseScrewPost003"
  Angle = 360
  Axis = (0,1,0)
  Base = (0,0,0)
  FaceMakerClass = Part::FaceMakerBullseye
  Placement = pos=(12.5,4.5,62) rot=(0,0,1;0rad)
  Solid = false
  Source = -> Face090
  Symmetric = false
FEATURE [Part::Box] Box015  label="Cube011"
  AttacherType = Attacher::AttachEngine3D
  Height = 28.8
  Length = 3
  Placement = pos=(107.3,28,21.6) rot=(0,0,1;0rad)
  Width = 7
FEATURE [Part::Box] Box016  label="Cube012"
  AttacherType = Attacher::AttachEngine3D
  Height = 3
  Length = 7.4
  Placement = pos=(107.3,28,18.6) rot=(0,0,1;0rad)
  Width = 7
FEATURE [Part::Box] Box017  label="Cube013"
  AttacherType = Attacher::AttachEngine3D
  Height = 3
  Length = 7.4
  Placement = pos=(107.3,28,50.4) rot=(0,0,1;0rad)
  Width = 7
FEATURE [Part::Cylinder] Cylinder024
  Angle = 360
  AttacherType = Attacher::AttachEngine3D
  Height = 20
  Placement = pos=(0,0,36.15) rot=(0,0,1;0rad)
  Radius = 14.3
FEATURE [Part::Cylinder] Cylinder025
  Angle = 360
  AttacherType = Attacher::AttachEngine3D
  Height = 10
  Placement = pos=(0,0,36.15) rot=(0,0,1;0rad)
  Radius = 4
FEATURE [Part::MultiFuse] Fusion066  label="removeToCreteHoleForPlugHousing009"
  Placement = pos=(70,19,36) rot=(0,1,0;1.5708rad)
  Shapes = -> [Cylinder024,Cylinder025]
FEATURE [Part::MultiFuse] Fusion065  label="plugHousingBracketHolder002"
  Shapes = -> [Box017,Box015,Box016]
FEATURE [Part::Cut] Cut025  label="plugHousingBracketHolder003"
  Base = -> Fusion065
  Placement = pos=(7,0,0) rot=(0,0,1;0rad)
  Tool = -> Fusion066
FEATURE [Sketcher::SketchObject] Sketch047
  FullyConstrained = false
  Placement = pos=(0,0,0) rot=(1,0,0;1.5708rad)
  sketch-geometry (24):
    g0: ArcOfCircle CenterX=-4 CenterY=-10.5 CenterZ=0 NormalX=0 NormalY=0 NormalZ=1 AngleXU=0 Radius=1.5 StartAngle=6e-16 EndAngle=3.14159
    g1: ArcOfCircle CenterX=-34.2 CenterY=-10.5 CenterZ=0 NormalX=0 NormalY=0 NormalZ=1 AngleXU=0 Radius=1.5 StartAngle=0 EndAngle=3.14159
    g2: ArcOfCircle CenterX=-34.2 CenterY=-27.7 CenterZ=0 NormalX=0 NormalY=0 NormalZ=1 AngleXU=0 Radius=1.5 StartAngle=3.14159 EndAngle=6.28319
    g3: ArcOfCircle CenterX=-4 CenterY=-27.7 CenterZ=0 NormalX=0 NormalY=0 NormalZ=1 AngleXU=0 Radius=1.5 StartAngle=3.1416 EndAngle=6.28319
    g4: ArcOfCircle CenterX=-10 CenterY=-4.3 CenterZ=0 NormalX=0 NormalY=0 NormalZ=1 AngleXU=0 Radius=1.5 StartAngle=2e-16 EndAngle=3.14159
    g5: ArcOfCircle CenterX=-16.1 CenterY=-1.8 CenterZ=0 NormalX=0 NormalY=0 NormalZ=1 AngleXU=0 Radius=1.5 StartAngle=5e-16 EndAngle=3.14159
    g6: ArcOfCircle CenterX=-22.1 CenterY=-1.8 CenterZ=0 NormalX=0 NormalY=0 NormalZ=1 AngleXU=0 Radius=1.5 StartAngle=5e-16 EndAngle=3.14159
    g7: ArcOfCircle CenterX=-28.2 CenterY=-4.3 CenterZ=0 NormalX=0 NormalY=0 NormalZ=1 AngleXU=0 Radius=1.5 StartAngle=2e-16 EndAngle=3.14159
    g8: ArcOfCircle CenterX=-10 CenterY=-33.9 CenterZ=0 NormalX=0 NormalY=0 NormalZ=1 AngleXU=0 Radius=1.5 StartAngle=3.14159 EndAngle=6.28319
    g9: ArcOfCircle CenterX=-16.1 CenterY=-36.4 CenterZ=0 NormalX=0 NormalY=0 NormalZ=1 AngleXU=0 Radius=1.5 StartAngle=3.14159 EndAngle=6.28319
    g10: ArcOfCircle CenterX=-22.1 CenterY=-36.4 CenterZ=0 NormalX=0 NormalY=0 NormalZ=1 AngleXU=0 Radius=1.5 StartAngle=3.14159 EndAngle=6.28319
    g11: ArcOfCircle CenterX=-28.2 CenterY=-33.9 CenterZ=0 NormalX=0 NormalY=0 NormalZ=1 AngleXU=0 Radius=1.5 StartAngle=3.14159 EndAngle=6.28319
    g12: LineSegment StartX=-35.7 StartY=-10.5 StartZ=0 EndX=-35.7 EndY=-27.7 EndZ=0
    g13: LineSegment StartX=-32.7 StartY=-10.5 StartZ=0 EndX=-32.7 EndY=-27.7 EndZ=0
    g14: LineSegment StartX=-29.7 StartY=-33.9 StartZ=0 EndX=-29.7 EndY=-4.3 EndZ=0
    g15: LineSegment StartX=-26.7 StartY=-33.9 StartZ=0 EndX=-26.7 EndY=-4.3 EndZ=0
    g16: LineSegment StartX=-2.5 StartY=-10.5 StartZ=0 EndX=-2.5 EndY=-27.7 EndZ=0
    g17: LineSegment StartX=-8.5 StartY=-4.3 StartZ=0 EndX=-8.5 EndY=-33.9 EndZ=0
    g18: LineSegment StartX=-5.5 StartY=-10.5 StartZ=0 EndX=-5.5 EndY=-27.7 EndZ=0
    g19: LineSegment StartX=-11.5 StartY=-4.3 StartZ=0 EndX=-11.5 EndY=-33.9 EndZ=0
    g20: LineSegment StartX=-14.6 StartY=-1.8 StartZ=0 EndX=-14.6 EndY=-36.4 EndZ=0
    g21: LineSegment StartX=-17.6 StartY=-1.8 StartZ=0 EndX=-17.6 EndY=-36.4 EndZ=0
    g22: LineSegment StartX=-20.6 StartY=-36.4 StartZ=0 EndX=-20.6 EndY=-1.8 EndZ=0
    g23: LineSegment StartX=-23.6 StartY=-1.8 StartZ=0 EndX=-23.6 EndY=-36.4 EndZ=0
  constraints (48):
    c: Block(g0)
    c: Block(g1)
    c: Block(g2)
    c: Block(g3)
    c: Block(g4)
    c: Block(g5)
    c: Block(g6)
    c: Block(g7)
    c: Block(g8)
    c: Block(g9)
    c: Block(g10)
    c: Block(g11)
    c: Coincident(g12,g1)
    c: Coincident(g12,g2)
    c: Vertical(g12)
    c: Coincident(g13,g1)
    c: Coincident(g13,g2)
    c: Vertical(g13)
    c: Coincident(g14,g11)
    c: Coincident(g14,g7)
    c: Vertical(g14)
    c: Coincident(g15,g11)
    c: Coincident(g15,g7)
    c: Vertical(g15)
    c: Coincident(g16,g0)
    c: Coincident(g16,g3)
    c: Vertical(g16)
    c: Coincident(g17,g4)
    c: Coincident(g17,g8)
    c: Vertical(g17)
    c: Coincident(g18,g0)
    c: Coincident(g18,g3)
    c: Vertical(g18)
    c: Coincident(g19,g4)
    c: Coincident(g19,g8)
    c: Vertical(g19)
    c: Coincident(g20,g5)
    c: Coincident(g20,g9)
    c: Vertical(g20)
    c: Coincident(g21,g5)
    c: Coincident(g21,g9)
    c: Vertical(g21)
    c: Coincident(g22,g10)
    c: Coincident(g22,g6)
    c: Vertical(g22)
    c: Coincident(g23,g6)
    c: Coincident(g23,g10)
    c: Vertical(g23)
FEATURE [Part::Extrusion] Extrude038  label="removeToCreateFanGrillHoles001"
  Base = -> Sketch047
  Dir = (0,-1,6e-16)
  DirMode = 2
  FaceMakerClass = Part::FaceMakerBullseye
  LengthFwd = 10
  LengthRev = 0
  Placement = pos=(65.4,44,54.82) rot=(0,0,1;0rad)
  Solid = true
  Symmetric = false
FEATURE [Part::Feature] Wire004
  shape: bbox 11 x 5.2 x 2e-07 mm, 0 faces, 0 solids (baked)
FEATURE [Part::Revolution] Revolve095
  Angle = 360
  Axis = (0,1,0)
  Base = (0,0,0)
  FaceMakerClass = Part::FaceMakerBullseye
  Placement = pos=(30.3,38,19.7) rot=(0,0,1;0rad)
  Solid = true
  Source = -> Wire004
  Symmetric = false
FEATURE [Part::Feature] Wire005
  shape: bbox 11 x 5.2 x 2e-07 mm, 0 faces, 0 solids (baked)
FEATURE [Part::Revolution] Revolve096
  Angle = 360
  Axis = (0,1,0)
  Base = (0,0,0)
  FaceMakerClass = Part::FaceMakerBullseye
  Placement = pos=(30.3,38,51.7) rot=(0,0,1;0rad)
  Solid = true
  Source = -> Wire005
  Symmetric = false
FEATURE [Part::Feature] Wire006
  shape: bbox 11 x 5.2 x 2e-07 mm, 0 faces, 0 solids (baked)
FEATURE [Part::Revolution] Revolve097
  Angle = 360
  Axis = (0,1,0)
  Base = (0,0,0)
  FaceMakerClass = Part::FaceMakerBullseye
  Placement = pos=(62.3,38,51.7) rot=(0,0,1;0rad)
  Solid = true
  Source = -> Wire006
  Symmetric = false
FEATURE [Part::Feature] Wire007
  shape: bbox 11 x 5.2 x 2e-07 mm, 0 faces, 0 solids (baked)
FEATURE [Part::Revolution] Revolve098
  Angle = 360
  Axis = (0,1,0)
  Base = (0,0,0)
  FaceMakerClass = Part::FaceMakerBullseye
  Placement = pos=(62.3,38,19.7) rot=(0,0,1;0rad)
  Solid = true
  Source = -> Wire007
  Symmetric = false
FEATURE [Part::MultiFuse] Fusion067  label="fanScrewHousing002"
  Shapes = -> [Revolve098,Revolve097,Revolve096,Revolve095]
FEATURE [Part::Feature] Face091 .. Face094  x4 (patterned run collapsed; names and placements below)
  shape: bbox 3.5 x 17.8 x 2e-07 mm, 1 faces, 0 solids (baked)
FEATURE [Part::Revolution] Revolve099  label="removeToCreateScrewAndThreadedInsertHole026"
  Angle = 360
  Axis = (0,1,0)
  Base = (0,0,0)
  FaceMakerClass = Part::FaceMakerBullseye
  Placement = pos=(62.3,30.3,19.7) rot=(0,0,1;0rad)
  Solid = false
  Source = -> Face091
  Symmetric = false
FEATURE [Part::Revolution] Revolve100  label="removeToCreateScrewAndThreadedInsertHole027"
  Angle = 360
  Axis = (0,1,0)
  Base = (0,0,0)
  FaceMakerClass = Part::FaceMakerBullseye
  Placement = pos=(62.3,30.3,51.7) rot=(0,0,1;0rad)
  Solid = false
  Source = -> Face092
  Symmetric = false
FEATURE [Part::Revolution] Revolve101  label="removeToCreateScrewAndThreadedInsertHole028"
  Angle = 360
  Axis = (0,1,0)
  Base = (0,0,0)
  FaceMakerClass = Part::FaceMakerBullseye
  Placement = pos=(30.3,30.3,19.7) rot=(0,0,1;0rad)
  Solid = false
  Source = -> Face093
  Symmetric = false
FEATURE [Part::Revolution] Revolve102  label="removeToCreateScrewAndThreadedInsertHole029"
  Angle = 360
  Axis = (0,1,0)
  Base = (0,0,0)
  FaceMakerClass = Part::FaceMakerBullseye
  Placement = pos=(30.3,30.3,51.7) rot=(0,0,1;0rad)
  Solid = false
  Source = -> Face094
  Symmetric = false
FEATURE [Part::MultiFuse] Fusion068  label="createThreadedInsertHolesForFan002"
  Shapes = -> [Revolve099,Revolve100,Revolve101,Revolve102]
FEATURE [Part::Cut] Cut026  label="fanScrewHousing003"
  Base = -> Fusion067
  Tool = -> Fusion068
FEATURE [Sketcher::SketchObject] Sketch048
  FullyConstrained = false
  Placement = pos=(0,0,0) rot=(1,0,0;1.5708rad)
  sketch-geometry (24):
    g0: ArcOfCircle CenterX=-4 CenterY=-10.5 CenterZ=0 NormalX=0 NormalY=0 NormalZ=1 AngleXU=0 Radius=1.5 StartAngle=6e-16 EndAngle=3.14159
    g1: ArcOfCircle CenterX=-34.2 CenterY=-10.5 CenterZ=0 NormalX=0 NormalY=0 NormalZ=1 AngleXU=0 Radius=1.5 StartAngle=0 EndAngle=3.14159
    g2: ArcOfCircle CenterX=-34.2 CenterY=-27.7 CenterZ=0 NormalX=0 NormalY=0 NormalZ=1 AngleXU=0 Radius=1.5 StartAngle=3.14159 EndAngle=6.28319
    g3: ArcOfCircle CenterX=-4 CenterY=-27.7 CenterZ=0 NormalX=0 NormalY=0 NormalZ=1 AngleXU=0 Radius=1.5 StartAngle=3.1416 EndAngle=6.28319
    g4: ArcOfCircle CenterX=-10 CenterY=-4.3 CenterZ=0 NormalX=0 NormalY=0 NormalZ=1 AngleXU=0 Radius=1.5 StartAngle=2e-16 EndAngle=3.14159
    g5: ArcOfCircle CenterX=-16.1 CenterY=-1.8 CenterZ=0 NormalX=0 NormalY=0 NormalZ=1 AngleXU=0 Radius=1.5 StartAngle=5e-16 EndAngle=3.14159
    g6: ArcOfCircle CenterX=-22.1 CenterY=-1.8 CenterZ=0 NormalX=0 NormalY=0 NormalZ=1 AngleXU=0 Radius=1.5 StartAngle=5e-16 EndAngle=3.14159
    g7: ArcOfCircle CenterX=-28.2 CenterY=-4.3 CenterZ=0 NormalX=0 NormalY=0 NormalZ=1 AngleXU=0 Radius=1.5 StartAngle=2e-16 EndAngle=3.14159
    g8: ArcOfCircle CenterX=-10 CenterY=-33.9 CenterZ=0 NormalX=0 NormalY=0 NormalZ=1 AngleXU=0 Radius=1.5 StartAngle=3.14159 EndAngle=6.28319
    g9: ArcOfCircle CenterX=-16.1 CenterY=-36.4 CenterZ=0 NormalX=0 NormalY=0 NormalZ=1 AngleXU=0 Radius=1.5 StartAngle=3.14159 EndAngle=6.28319
    g10: ArcOfCircle CenterX=-22.1 CenterY=-36.4 CenterZ=0 NormalX=0 NormalY=0 NormalZ=1 AngleXU=0 Radius=1.5 StartAngle=3.14159 EndAngle=6.28319
    g11: ArcOfCircle CenterX=-28.2 CenterY=-33.9 CenterZ=0 NormalX=0 NormalY=0 NormalZ=1 AngleXU=0 Radius=1.5 StartAngle=3.14159 EndAngle=6.28319
    g12: LineSegment StartX=-35.7 StartY=-10.5 StartZ=0 EndX=-35.7 EndY=-27.7 EndZ=0
    g13: LineSegment StartX=-32.7 StartY=-10.5 StartZ=0 EndX=-32.7 EndY=-27.7 EndZ=0
    g14: LineSegment StartX=-29.7 StartY=-33.9 StartZ=0 EndX=-29.7 EndY=-4.3 EndZ=0
    g15: LineSegment StartX=-26.7 StartY=-33.9 StartZ=0 EndX=-26.7 EndY=-4.3 EndZ=0
    g16: LineSegment StartX=-2.5 StartY=-10.5 StartZ=0 EndX=-2.5 EndY=-27.7 EndZ=0
    g17: LineSegment StartX=-8.5 StartY=-4.3 StartZ=0 EndX=-8.5 EndY=-33.9 EndZ=0
    g18: LineSegment StartX=-5.5 StartY=-10.5 StartZ=0 EndX=-5.5 EndY=-27.7 EndZ=0
    g19: LineSegment StartX=-11.5 StartY=-4.3 StartZ=0 EndX=-11.5 EndY=-33.9 EndZ=0
    g20: LineSegment StartX=-14.6 StartY=-1.8 StartZ=0 EndX=-14.6 EndY=-36.4 EndZ=0
    g21: LineSegment StartX=-17.6 StartY=-1.8 StartZ=0 EndX=-17.6 EndY=-36.4 EndZ=0
    g22: LineSegment StartX=-20.6 StartY=-36.4 StartZ=0 EndX=-20.6 EndY=-1.8 EndZ=0
    g23: LineSegment StartX=-23.6 StartY=-1.8 StartZ=0 EndX=-23.6 EndY=-36.4 EndZ=0
  constraints (48):
    c: Block(g0)
    c: Block(g1)
    c: Block(g2)
    c: Block(g3)
    c: Block(g4)
    c: Block(g5)
    c: Block(g6)
    c: Block(g7)
    c: Block(g8)
    c: Block(g9)
    c: Block(g10)
    c: Block(g11)
    c: Coincident(g12,g1)
    c: Coincident(g12,g2)
    c: Vertical(g12)
    c: Coincident(g13,g1)
    c: Coincident(g13,g2)
    c: Vertical(g13)
    c: Coincident(g14,g11)
    c: Coincident(g14,g7)
    c: Vertical(g14)
    c: Coincident(g15,g11)
    c: Coincident(g15,g7)
    c: Vertical(g15)
    c: Coincident(g16,g0)
    c: Coincident(g16,g3)
    c: Vertical(g16)
    c: Coincident(g17,g4)
    c: Coincident(g17,g8)
    c: Vertical(g17)
    c: Coincident(g18,g0)
    c: Coincident(g18,g3)
    c: Vertical(g18)
    c: Coincident(g19,g4)
    c: Coincident(g19,g8)
    c: Vertical(g19)
    c: Coincident(g20,g5)
    c: Coincident(g20,g9)
    c: Vertical(g20)
    c: Coincident(g21,g5)
    c: Coincident(g21,g9)
    c: Vertical(g21)
    c: Coincident(g22,g10)
    c: Coincident(g22,g6)
    c: Vertical(g22)
    c: Coincident(g23,g6)
    c: Coincident(g23,g10)
    c: Vertical(g23)
FEATURE [Part::Extrusion] Extrude039  label="removeToCreateFanGrillHoles002"
  Base = -> Sketch048
  Dir = (0,-1,6e-16)
  DirMode = 2
  FaceMakerClass = Part::FaceMakerBullseye
  LengthFwd = 10
  LengthRev = 0
  Placement = pos=(65.4,44,54.82) rot=(0,0,1;0rad)
  Solid = true
  Symmetric = false
FEATURE [Part::Cut] Cut027  label="fanScrewHousing004"
  Base = -> Cut026
  Tool = -> Extrude038
FEATURE [Part::Cut] Cut028  label="top014"
  Base = -> Fillet026
  Tool = -> Extrude039
FEATURE [Part::Feature] Face095 .. Face098  x4 (patterned run collapsed; names and placements below)
  shape: bbox 3.5 x 17.8 x 2e-07 mm, 1 faces, 0 solids (baked)
FEATURE [Part::Revolution] Revolve103  label="removeToCreateScrewAndThreadedInsertHole030"
  Angle = 360
  Axis = (0,1,0)
  Base = (0,0,0)
  FaceMakerClass = Part::FaceMakerBullseye
  Placement = pos=(62.3,30.3,19.7) rot=(0,0,1;0rad)
  Solid = false
  Source = -> Face095
  Symmetric = false
FEATURE [Part::Revolution] Revolve104  label="removeToCreateScrewAndThreadedInsertHole031"
  Angle = 360
  Axis = (0,1,0)
  Base = (0,0,0)
  FaceMakerClass = Part::FaceMakerBullseye
  Placement = pos=(62.3,30.3,51.7) rot=(0,0,1;0rad)
  Solid = false
  Source = -> Face096
  Symmetric = false
FEATURE [Part::Revolution] Revolve105  label="removeToCreateScrewAndThreadedInsertHole032"
  Angle = 360
  Axis = (0,1,0)
  Base = (0,0,0)
  FaceMakerClass = Part::FaceMakerBullseye
  Placement = pos=(30.3,30.3,19.7) rot=(0,0,1;0rad)
  Solid = false
  Source = -> Face097
  Symmetric = false
FEATURE [Part::Revolution] Revolve106  label="removeToCreateScrewAndThreadedInsertHole033"
  Angle = 360
  Axis = (0,1,0)
  Base = (0,0,0)
  FaceMakerClass = Part::FaceMakerBullseye
  Placement = pos=(30.3,30.3,51.7) rot=(0,0,1;0rad)
  Solid = false
  Source = -> Face098
  Symmetric = false
FEATURE [Part::MultiFuse] Fusion069  label="createThreadedInsertHolesForFan003"
  Shapes = -> [Revolve103,Revolve104,Revolve105,Revolve106]
FEATURE [Part::Cut] Cut029  label="top015"
  Base = -> Cut028
  Tool = -> Fusion054
FEATURE [Part::Cut] Cut030  label="fanScrewHousing005"
  Base = -> Cut027
  Tool = -> Fusion069
FEATURE [Part::Cylinder] Cylinder026  label="removeToCreteHoleForPlugHousing010"
  Angle = 360
  AttacherType = Attacher::AttachEngine3D
  Height = 20
  Placement = pos=(-2,19,36) rot=(0,1,0;1.5708rad)
  Radius = 14.3
FEATURE [Part::Box] Box018  label="removeToCreteHoleForPlugHousing011"
  AttacherType = Attacher::AttachEngine3D
  Height = 28.6
  Length = 10
  Placement = pos=(-2,0,21.7) rot=(0,0,1;0rad)
  Width = 19
FEATURE [Part::Box] Box019  label="wireHolderBottomCaseBit"
  AttacherType = Attacher::AttachEngine3D
  Height = 28
  Length = 3
  Placement = pos=(0,0,22) rot=(0,0,1;0rad)
  Width = 21
FEATURE [Part::Cylinder] Cylinder027  label="removeToCreteHoleForPlugHousing012"
  Angle = 360
  AttacherType = Attacher::AttachEngine3D
  Height = 20
  Placement = pos=(-2,19,36) rot=(0,1,0;1.5708rad)
  Radius = 14.3
FEATURE [Part::Cut] Cut031  label="wireHolderBottomCaseBit001"
  Base = -> Box019
  Tool = -> Cylinder027
FEATURE [Part::MultiFuse] Fusion070  label="removeToCreteHoleForPlugHousing013"
  Shapes = -> [Box018,Cylinder026]
FEATURE [Part::Cut] Cut032  label="top016"
  Base = -> Cut029
  Tool = -> Fusion070
FEATURE [Part::Cylinder] Cylinder028
  Angle = 360
  AttacherType = Attacher::AttachEngine3D
  Height = 20
  Placement = pos=(0,0,36.15) rot=(0,0,1;0rad)
  Radius = 14.3
FEATURE [Part::Cylinder] Cylinder029
  Angle = 360
  AttacherType = Attacher::AttachEngine3D
  Height = 10
  Placement = pos=(0,0,36.15) rot=(0,0,1;0rad)
  Radius = 4
FEATURE [Part::MultiFuse] Fusion071  label="removeToCreteHoleForPlugHousing014"
  Placement = pos=(70,19,36) rot=(0,1,0;1.5708rad)
  Shapes = -> [Cylinder028,Cylinder029]
FEATURE [Sketcher::SketchObject] Sketch049  label="topSketch011"
  FullyConstrained = true
  sketch-geometry (4):
    g0: ArcOfCircle CenterX=105 CenterY=19 CenterZ=0 NormalX=0 NormalY=0 NormalZ=1 AngleXU=0 Radius=20.6155 StartAngle=5.54125 EndAngle=6.28319
    g1: ArcOfCircle CenterX=105 CenterY=19 CenterZ=0 NormalX=0 NormalY=0 NormalZ=1 AngleXU=0 Radius=13 StartAngle=5.54125 EndAngle=6.28319
    g2: LineSegment StartX=118 StartY=19 StartZ=0 EndX=125.616 EndY=19 EndZ=0
    g3: LineSegment StartX=114.583 StartY=10.2157 StartZ=0 EndX=120.197 EndY=5.06982 EndZ=0
  constraints (7):
    c: Block(g0)
    c: Block(g1)
    c: Coincident(g2,g1)
    c: Coincident(g2,g0)
    c: Horizontal(g2)
    c: Coincident(g3,g1)
    c: Coincident(g3,g0)
FEATURE [Part::Box] Box020  label="removeToCreteHoleForPlugHousing015"
  AttacherType = Attacher::AttachEngine3D
  Height = 28.6
  Length = 20
  Placement = pos=(106.15,0,21.7) rot=(0,0,1;0rad)
  Width = 19
FEATURE [Part::MultiFuse] Fusion072  label="removeToCreteHoleForPlugHousing016"
  Shapes = -> [Box020,Fusion071]
FEATURE [Part::Cut] Cut033  label="removeToCreteHoleForPlugHousing017"
  Base = -> Cut032
  Tool = -> Fusion072
FEATURE [Part::Cylinder] Cylinder030
  Angle = 360
  AttacherType = Attacher::AttachEngine3D
  Height = 20
  Placement = pos=(0,0,36.15) rot=(0,0,1;0rad)
  Radius = 14.3
FEATURE [Part::Cylinder] Cylinder031
  Angle = 360
  AttacherType = Attacher::AttachEngine3D
  Height = 10
  Placement = pos=(0,0,36.15) rot=(0,0,1;0rad)
  Radius = 4
FEATURE [Part::Box] Box021  label="removeToCreteHoleForPlugHousing019"
  AttacherType = Attacher::AttachEngine3D
  Height = 28.6
  Length = 20
  Placement = pos=(106.15,0,21.7) rot=(0,0,1;0rad)
  Width = 19
FEATURE [Part::MultiFuse] Fusion074  label="removeToCreteHoleForPlugHousing020"
  Placement = pos=(70,19,36) rot=(0,1,0;1.5708rad)
  Shapes = -> [Cylinder030,Cylinder031]
FEATURE [Part::MultiFuse] Fusion073  label="removeToCreteHoleForPlugHousing018"
  Placement = pos=(0,0,28.3) rot=(0,0,1;0rad)
  Shapes = -> [Box021,Fusion074]
FEATURE [Part::Cylinder] Cylinder032
  Angle = 360
  AttacherType = Attacher::AttachEngine3D
  Height = 20
  Placement = pos=(0,0,36.15) rot=(0,0,1;0rad)
  Radius = 14.3
FEATURE [Part::Cylinder] Cylinder033
  Angle = 360
  AttacherType = Attacher::AttachEngine3D
  Height = 10
  Placement = pos=(0,0,36.15) rot=(0,0,1;0rad)
  Radius = 4
FEATURE [Part::Box] Box022  label="removeToCreteHoleForPlugHousing021"
  AttacherType = Attacher::AttachEngine3D
  Height = 28.6
  Length = 20
  Placement = pos=(106.15,0,21.7) rot=(0,0,1;0rad)
  Width = 19
FEATURE [Part::MultiFuse] Fusion076  label="removeToCreteHoleForPlugHousing023"
  Placement = pos=(70,19,36) rot=(0,1,0;1.5708rad)
  Shapes = -> [Cylinder032,Cylinder033]
FEATURE [Part::MultiFuse] Fusion075  label="removeToCreteHoleForPlugHousing022"
  Placement = pos=(0,0,-28.3) rot=(0,0,1;0rad)
  Shapes = -> [Box022,Fusion076]
FEATURE [Part::MultiFuse] Fusion077  label="removeToCreatePlugHousingBottomBit"
  Shapes = -> [Fusion075,Fusion073]
FEATURE [Part::Cylinder] Cylinder034
  Angle = 360
  AttacherType = Attacher::AttachEngine3D
  Height = 20
  Placement = pos=(0,0,36.15) rot=(0,0,1;0rad)
  Radius = 14.3
FEATURE [Part::Cylinder] Cylinder035
  Angle = 360
  AttacherType = Attacher::AttachEngine3D
  Height = 10
  Placement = pos=(0,0,36.15) rot=(0,0,1;0rad)
  Radius = 4
FEATURE [Part::MultiFuse] Fusion078  label="removeToCreteHoleForPlugHousing024"
  Placement = pos=(70,19,36) rot=(0,1,0;1.5708rad)
  Shapes = -> [Cylinder034,Cylinder035]
FEATURE [Part::MultiFuse] Fusion079  label="removeToCreatePlugHousingBottomBit001"
  Shapes = -> [Fusion078,Fusion077]
FEATURE [Part::Extrusion] Extrude040  label="bottomPlugHousingBit"
  Base = -> Sketch049
  Dir = (0,0,1)
  DirMode = 2
  FaceMakerClass = Part::FaceMakerBullseye
  LengthFwd = 72
  LengthRev = 0
  Solid = true
  Symmetric = false
FEATURE [Part::Cut] Cut034  label="bottomPlugHousingBit001"
  Base = -> Extrude040
  Tool = -> Fusion079
FEATURE [Part::Box] Box023  label="Cube014"
  AttacherType = Attacher::AttachEngine3D
  Height = 16
  Length = 8
  Placement = pos=(12.7,31.52,28) rot=(0,0,1;0rad)
  Width = 4
FEATURE [Part::Cylinder] Cylinder036
  Angle = 360
  AttacherType = Attacher::AttachEngine3D
  Height = 10
  Placement = pos=(0,0,36.15) rot=(0,0,1;0rad)
  Radius = 4
FEATURE [Part::Cylinder] Cylinder037
  Angle = 360
  AttacherType = Attacher::AttachEngine3D
  Height = 20
  Placement = pos=(0,0,36.15) rot=(0,0,1;0rad)
  Radius = 8.2
FEATURE [Part::MultiFuse] Fusion080  label="removeToCreteHoleForPlugHousing025"
  Placement = pos=(-42,19,36) rot=(0,1,0;1.5708rad)
  Shapes = -> [Cylinder037,Cylinder036]
FEATURE [Sketcher::SketchObject] Sketch050  label="topSketch012"
  FullyConstrained = true
  sketch-geometry (4):
    g0: LineSegment StartX=16.8446 StartY=31.512 StartZ=0 EndX=16.3251 EndY=34.4666 EndZ=0
    g1: ArcOfCircle CenterX=19 CenterY=19.2524 CenterZ=0 NormalX=0 NormalY=0 NormalZ=1 AngleXU=0 Radius=15.4476 StartAngle=1.74483 EndAngle=2.72717
    g2: ArcOfCircle CenterX=19 CenterY=19.2524 CenterZ=0 NormalX=0 NormalY=0 NormalZ=1 AngleXU=0 Radius=12.4476 StartAngle=1.74483 EndAngle=2.73189
    g3: LineSegment StartX=4.86004 StartY=25.4725 StartZ=0 EndX=7.58253 EndY=24.2107 EndZ=0
  constraints (7):
    c: Block(g0)
    c: Coincident(g1,g0)
    c: Coincident(g2,g0)
    c: Coincident(g3,g1)
    c: Coincident(g3,g2)
    c: Block(g1)
    c: Block(g2)
FEATURE [Part::Extrusion] Extrude041
  Base = -> Sketch050
  Dir = (0,0,1)
  DirMode = 2
  FaceMakerClass = Part::FaceMakerBullseye
  LengthFwd = 10.6
  LengthRev = 0
  Placement = pos=(0,0,31) rot=(0,0,1;0rad)
  Solid = true
  Symmetric = false
FEATURE [Part::Cut] Cut035
  Base = -> Extrude041
  Placement = pos=(0,0,-0.3) rot=(0,0,1;0rad)
  Tool = -> Fusion080
FEATURE [Part::Cut] Cut036
  Base = -> Box023
  Tool = -> Cut035
FEATURE [Part::Fillet] Fillet027
  Base = -> Cut036
  Edges = 1 edges r=0.7: [Edge13]
FEATURE [Part::Fillet] Fillet028
  Base = -> Fillet027
  Edges = 1 edges r=0.7: [Edge13]
FEATURE [Part::Fillet] Fillet029
  Base = -> Fillet028
  Edges = 1 edges r=0.7: [Edge16]
FEATURE [Part::Fillet] Fillet030
  Base = -> Fillet029
  Edges = 1 edges r=0.7: [Edge11]
FEATURE [Part::Fillet] Fillet031
  Base = -> Fillet030
  Edges = 1 edges r=0.7: [Edge10]
FEATURE [Part::Fillet] Fillet032
  Base = -> Fillet031
  Edges = 1 edges r=1.2: [Edge5]
FEATURE [Part::Fillet] Fillet033
  Base = -> Fillet032
  Edges = 1 edges r=1.2: [Edge12]
FEATURE [Part::Fillet] Fillet034  label="wireHousingRetainer"
  Base = -> Fillet033
  Edges = 1 edges r=2: [Edge1]
  Placement = pos=(0.3,0,0) rot=(0,0,1;0rad)
FEATURE [Part::Feature] Face099
  shape: bbox 3.5 x 17.8 x 2e-07 mm, 1 faces, 0 solids (baked)
FEATURE [Part::Revolution] Revolve107  label="removeToCreateScrewAndThreadedInsertHole034"
  Angle = 360
  Axis = (0,1,0)
  Base = (0,0,0)
  FaceMakerClass = Part::FaceMakerBullseye
  Placement = pos=(12.5,0,10) rot=(0,0,1;0rad)
  Solid = false
  Source = -> Face099
  Symmetric = false
FEATURE [Part::Feature] Face100
  shape: bbox 3.5 x 17.8 x 2e-07 mm, 1 faces, 0 solids (baked)
FEATURE [Part::Revolution] Revolve108  label="removeToCreateScrewAndThreadedInsertHole035"
  Angle = 360
  Axis = (0,1,0)
  Base = (0,0,0)
  FaceMakerClass = Part::FaceMakerBullseye
  Placement = pos=(12.5,0,62) rot=(0,0,1;0rad)
  Solid = false
  Source = -> Face100
  Symmetric = false
FEATURE [Part::Feature] Face101
  shape: bbox 3.5 x 17.8 x 2e-07 mm, 1 faces, 0 solids (baked)
FEATURE [Part::Revolution] Revolve109  label="removeToCreateScrewAndThreadedInsertHole036"
  Angle = 360
  Axis = (0,1,0)
  Base = (0,0,0)
  FaceMakerClass = Part::FaceMakerBullseye
  Placement = pos=(89.5,0,68.5) rot=(0,0,1;0rad)
  Solid = false
  Source = -> Face101
  Symmetric = false
FEATURE [Part::Feature] Face102
  shape: bbox 3.5 x 17.8 x 2e-07 mm, 1 faces, 0 solids (baked)
FEATURE [Part::Revolution] Revolve110  label="removeToCreateScrewAndThreadedInsertHole037"
  Angle = 360
  Axis = (0,1,0)
  Base = (0,0,0)
  FaceMakerClass = Part::FaceMakerBullseye
  Placement = pos=(89.5,0,3.5) rot=(0,0,1;0rad)
  Solid = false
  Source = -> Face102
  Symmetric = false
FEATURE [Part::Feature] Face103
  shape: bbox 3.5 x 17.8 x 2e-07 mm, 1 faces, 0 solids (baked)
FEATURE [Part::Revolution] Revolve111  label="removeToCreateScrewAndThreadedInsertHole038"
  Angle = 360
  Axis = (0,1,0)
  Base = (0,0,0)
  FaceMakerClass = Part::FaceMakerBullseye
  Placement = pos=(109.5,4.7,3.5) rot=(0,0,1;0rad)
  Solid = false
  Source = -> Face103
  Symmetric = false
FEATURE [Part::Feature] Face104
  shape: bbox 3.5 x 17.8 x 2e-07 mm, 1 faces, 0 solids (baked)
FEATURE [Part::Revolution] Revolve112  label="removeToCreateScrewAndThreadedInsertHole039"
  Angle = 360
  Axis = (0,1,0)
  Base = (0,0,0)
  FaceMakerClass = Part::FaceMakerBullseye
  Placement = pos=(109.5,4.7,68.5) rot=(0,0,1;0rad)
  Solid = false
  Source = -> Face104
  Symmetric = false
FEATURE [Part::MultiFuse] Fusion081  label="removeToCreateScrewAndThreadedInsertHole040"
  Shapes = -> [Revolve107,Revolve108,Revolve109,Revolve110,Revolve111,Revolve112]
FEATURE [Part::MultiFuse] Fusion082  label="casePillars002"
  Shapes = -> [Revolve094,Revolve092,Revolve090,Revolve089,Revolve091,Revolve093]
FEATURE [Part::Cut] Cut037  label="casePillars003"
  Base = -> Fusion082
  Tool = -> Fusion081
FEATURE [Sketcher::SketchObject] Sketch051
  FullyConstrained = true
  Placement = pos=(117,19,0) rot=(0.57735,0.57735,0.57735;2.0944rad)
  sketch-geometry (48):
    g0: LineSegment StartX=-49.19 StartY=69.25 StartZ=0 EndX=-49.19 EndY=66.25 EndZ=0
    g1: LineSegment StartX=-49.19 StartY=63.5 StartZ=0 EndX=-49.19 EndY=60.5 EndZ=0
    g2: LineSegment StartX=-49.19 StartY=57.75 StartZ=0 EndX=-49.19 EndY=54.75 EndZ=0
    g3: LineSegment StartX=-49.19 StartY=52 StartZ=0 EndX=-49.19 EndY=49 EndZ=0
    g4: LineSegment StartX=-49.19 StartY=46.25 StartZ=0 EndX=-49.19 EndY=43.25 EndZ=0
    g5: LineSegment StartX=-49.19 StartY=40.5 StartZ=0 EndX=-49.19 EndY=37.5 EndZ=0
    g6: LineSegment StartX=-49.19 StartY=34.5 StartZ=0 EndX=-49.19 EndY=31.5 EndZ=0
    g7: LineSegment StartX=-49.19 StartY=28.75 StartZ=0 EndX=-49.19 EndY=25.75 EndZ=0
    g8: LineSegment StartX=-49.19 StartY=23 StartZ=0 EndX=-49.19 EndY=20 EndZ=0
    g9: LineSegment StartX=-49.19 StartY=17.25 StartZ=0 EndX=-49.19 EndY=14.25 EndZ=0
    g10: LineSegment StartX=-49.19 StartY=11.5 StartZ=0 EndX=-49.19 EndY=8.5 EndZ=0
    g11: LineSegment StartX=-49.19 StartY=5.75 StartZ=0 EndX=-49.19 EndY=2.75 EndZ=0
    g12: ArcOfCircle CenterX=-1.5 CenterY=67.75 CenterZ=0 NormalX=0 NormalY=0 NormalZ=1 AngleXU=0 Radius=1.5 StartAngle=4.71239 EndAngle=7.85398
    g13: ArcOfCircle CenterX=-1.5 CenterY=62 CenterZ=0 NormalX=0 NormalY=0 NormalZ=1 AngleXU=0 Radius=1.5 StartAngle=4.71239 EndAngle=7.85398
    g14: ArcOfCircle CenterX=-1.5 CenterY=56.25 CenterZ=0 NormalX=0 NormalY=0 NormalZ=1 AngleXU=0 Radius=1.5 StartAngle=4.71239 EndAngle=7.85398
    g15: ArcOfCircle CenterX=-11.49 CenterY=50.5 CenterZ=0 NormalX=0 NormalY=0 NormalZ=1 AngleXU=0 Radius=1.5 StartAngle=4.71239 EndAngle=7.85398
    g16: ArcOfCircle CenterX=-16.28 CenterY=44.75 CenterZ=0 NormalX=0 NormalY=0 NormalZ=1 AngleXU=0 Radius=1.5 StartAngle=4.71239 EndAngle=7.85398
    g17: ArcOfCircle CenterX=-18.2337 CenterY=39 CenterZ=0 NormalX=0 NormalY=0 NormalZ=1 AngleXU=0 Radius=1.5 StartAngle=4.71485 EndAngle=7.85398
    g18: ArcOfCircle CenterX=-16.2837 CenterY=27.25 CenterZ=0 NormalX=0 NormalY=0 NormalZ=1 AngleXU=0 Radius=1.5 StartAngle=4.71485 EndAngle=7.85398
    g19: ArcOfCircle CenterX=-18.2337 CenterY=33 CenterZ=0 NormalX=0 NormalY=0 NormalZ=1 AngleXU=0 Radius=1.5 StartAngle=4.71485 EndAngle=7.85398
    g20: ArcOfCircle CenterX=-11.49 CenterY=21.5 CenterZ=0 NormalX=0 NormalY=0 NormalZ=1 AngleXU=0 Radius=1.5 StartAngle=4.71239 EndAngle=7.85398
    g21: ArcOfCircle CenterX=-1.5 CenterY=4.25 CenterZ=0 NormalX=0 NormalY=0 NormalZ=1 AngleXU=0 Radius=1.5 StartAngle=4.71239 EndAngle=7.85398
    g22: ArcOfCircle CenterX=-1.5 CenterY=10 CenterZ=0 NormalX=0 NormalY=0 NormalZ=1 AngleXU=0 Radius=1.5 StartAngle=4.71239 EndAngle=7.85398
    g23: ArcOfCircle CenterX=-1.5 CenterY=15.75 CenterZ=0 NormalX=0 NormalY=0 NormalZ=1 AngleXU=0 Radius=1.5 StartAngle=4.71239 EndAngle=7.85398
    g24: LineSegment StartX=-49.19 StartY=69.25 StartZ=0 EndX=-1.5 EndY=69.25 EndZ=0
    g25: LineSegment StartX=-49.19 StartY=66.25 StartZ=0 EndX=-1.5 EndY=66.25 EndZ=0
    g26: LineSegment StartX=-49.19 StartY=63.5 StartZ=0 EndX=-1.5 EndY=63.5 EndZ=0
    g27: LineSegment StartX=-49.19 StartY=60.5 StartZ=0 EndX=-1.5 EndY=60.5 EndZ=0
    g28: LineSegment StartX=-49.19 StartY=57.75 StartZ=0 EndX=-1.5 EndY=57.75 EndZ=0
    g29: LineSegment StartX=-49.19 StartY=54.75 StartZ=0 EndX=-1.5 EndY=54.75 EndZ=0
    g30: LineSegment StartX=-49.19 StartY=52 StartZ=0 EndX=-11.49 EndY=52 EndZ=0
    g31: LineSegment StartX=-49.19 StartY=49 StartZ=0 EndX=-11.49 EndY=49 EndZ=0
    g32: LineSegment StartX=-49.19 StartY=46.25 StartZ=0 EndX=-16.28 EndY=46.25 EndZ=0
    g33: LineSegment StartX=-49.19 StartY=43.25 StartZ=0 EndX=-16.28 EndY=43.25 EndZ=0
    g34: LineSegment StartX=-49.19 StartY=40.5 StartZ=0 EndX=-18.2337 EndY=40.5 EndZ=0
    g35: LineSegment StartX=-49.19 StartY=37.5 StartZ=0 EndX=-18.23 EndY=37.5 EndZ=0
    g36: LineSegment StartX=-49.19 StartY=34.5 StartZ=0 EndX=-18.2337 EndY=34.5 EndZ=0
    g37: LineSegment StartX=-49.19 StartY=31.5 StartZ=0 EndX=-18.23 EndY=31.5 EndZ=0
    g38: LineSegment StartX=-49.19 StartY=28.75 StartZ=0 EndX=-16.2837 EndY=28.75 EndZ=0
    g39: LineSegment StartX=-49.19 StartY=25.75 StartZ=0 EndX=-16.28 EndY=25.75 EndZ=0
    g40: LineSegment StartX=-49.19 StartY=23 StartZ=0 EndX=-11.49 EndY=23 EndZ=0
    g41: LineSegment StartX=-49.19 StartY=20 StartZ=0 EndX=-11.49 EndY=20 EndZ=0
    g42: LineSegment StartX=-49.19 StartY=17.25 StartZ=0 EndX=-1.5 EndY=17.25 EndZ=0
    g43: LineSegment StartX=-49.19 StartY=14.25 StartZ=0 EndX=-1.5 EndY=14.25 EndZ=0
    g44: LineSegment StartX=-49.19 StartY=11.5 StartZ=0 EndX=-1.5 EndY=11.5 EndZ=0
    g45: LineSegment StartX=-49.19 StartY=8.5 StartZ=0 EndX=-1.5 EndY=8.5 EndZ=0
    g46: LineSegment StartX=-49.19 StartY=5.75 StartZ=0 EndX=-1.5 EndY=5.75 EndZ=0
    g47: LineSegment StartX=-49.19 StartY=2.75 StartZ=0 EndX=-1.5 EndY=2.75 EndZ=0
  constraints (120):
    c: Vertical(g0)
    c: Distance(g0) = 3
    c: Block(g0)
    c: Vertical(g1)
    c: Distance(g1) = 3
    c: Vertical(g2)
    c: Equal(g0,g2) = 3
    c: Block(g2)
    c: Vertical(g3)
    c: Equal(g1,g3) = 3
    c: Vertical(g4)
    c: Equal(g0,g4) = 3
    c: Block(g4)
    c: Vertical(g5)
    c: Equal(g1,g5) = 3
    c: Vertical(g6)
    c: Equal(g0,g6) = 3
    c: Block(g6)
    c: Vertical(g7)
    c: Equal(g1,g7) = 3
    c: Vertical(g8)
    c: Equal(g0,g8) = 3
    c: Block(g8)
    c: Vertical(g9)
    c: Equal(g1,g9) = 3
    c: Vertical(g10)
    c: Equal(g0,g10) = 3
    c: Block(g10)
    c: Vertical(g11)
    c: Equal(g1,g11) = 3
    c: Block(g12)
    c: Block(g13)
    c: Block(g14)
    c: Block(g15)
    c: Block(g16)
    c: Block(g17)
    c: Block(g18)
    c: Block(g19)
    c: Block(g20)
    c: Block(g21)
    c: Block(g22)
    c: Block(g23)
    c: Block(g11)
    c: Block(g9)
    c: Block(g7)
    c: Block(g5)
    c: Block(g3)
    c: Block(g1)
    c: Coincident(g24,g0)
    c: Coincident(g24,g12)
    c: Horizontal(g24)
    c: Coincident(g25,g0)
    c: Coincident(g25,g12)
    c: Horizontal(g25)
    c: Coincident(g26,g1)
    c: Coincident(g26,g13)
    c: Horizontal(g26)
    c: Coincident(g27,g1)
    c: Coincident(g27,g13)
    c: Horizontal(g27)
    c: Coincident(g28,g2)
    c: Coincident(g28,g14)
    c: Horizontal(g28)
    c: Coincident(g29,g2)
    c: Coincident(g29,g14)
    c: Horizontal(g29)
    c: Coincident(g30,g3)
    c: Coincident(g30,g15)
    c: Horizontal(g30)
    c: Coincident(g31,g3)
    c: Coincident(g31,g15)
    c: Horizontal(g31)
    c: Coincident(g32,g4)
    c: Coincident(g32,g16)
    c: Horizontal(g32)
    c: Coincident(g33,g4)
    c: Coincident(g33,g16)
    c: Horizontal(g33)
    c: Coincident(g34,g5)
    c: Coincident(g34,g17)
    c: Horizontal(g34)
    c: Coincident(g35,g5)
    c: Coincident(g35,g17)
    c: Horizontal(g35)
    c: Coincident(g36,g6)
    c: Coincident(g36,g19)
    c: Horizontal(g36)
    c: Coincident(g37,g6)
    c: Coincident(g37,g19)
    c: Horizontal(g37)
    c: Coincident(g38,g7)
    c: Coincident(g38,g18)
    c: Horizontal(g38)
    c: Coincident(g39,g7)
    c: Coincident(g39,g18)
    c: Horizontal(g39)
    c: Coincident(g40,g8)
    c: Coincident(g40,g20)
    c: Horizontal(g40)
    c: Coincident(g41,g8)
    c: Coincident(g41,g20)
    c: Horizontal(g41)
    c: Coincident(g42,g9)
    c: Coincident(g42,g23)
    c: Horizontal(g42)
    c: Coincident(g43,g9)
    c: Coincident(g43,g23)
    c: Horizontal(g43)
    c: Coincident(g44,g10)
    c: Coincident(g44,g22)
    c: Horizontal(g44)
    c: Coincident(g45,g10)
    c: Coincident(g45,g22)
    c: Horizontal(g45)
    c: Coincident(g46,g11)
    c: Coincident(g46,g21)
    c: Horizontal(g46)
    c: Coincident(g47,g11)
    c: Coincident(g47,g21)
    c: Horizontal(g47)
FEATURE [Part::Extrusion] Extrude042
  Base = -> Sketch051
  Dir = (1,-2e-16,2e-16)
  DirMode = 2
  FaceMakerClass = Part::FaceMakerBullseye
  LengthFwd = 19
  LengthRev = 0
  Placement = pos=(-19,0,0) rot=(0,0,1;0rad)
  Solid = true
  Symmetric = false
FEATURE [Part::Fillet] Fillet035  label="removeToCreateVentalationHoles"
  Base = -> Extrude042
  Edges = <same value as first occurrence — deduplicated (x4 in doc)>
  Placement = pos=(7,0,0) rot=(0,0,1;0rad)
FEATURE [Part::Cut] Cut038  label="top017"
  Base = -> Cut033
  Tool = -> Fillet035
FEATURE [Sketcher::SketchObject] Sketch052  label="bottomSketch001"
  FullyConstrained = true
  sketch-geometry (26):
    g0: LineSegment StartX=6.29999 StartY=8 StartZ=0 EndX=3.29999 EndY=8 EndZ=0
    g1: LineSegment StartX=3.29999 StartY=8 StartZ=0 EndX=3.29999 EndY=-6.03275e-07 EndZ=0
    g2: ArcOfCircle CenterX=8.29999 CenterY=5 CenterZ=0 NormalX=0 NormalY=0 NormalZ=1 AngleXU=0 Radius=2 StartAngle=3.14159 EndAngle=4.71239
    g3: LineSegment StartX=6.29999 StartY=8 StartZ=0 EndX=6.29999 EndY=5 EndZ=0
    g4: ArcOfCircle CenterX=105 CenterY=19 CenterZ=0 NormalX=0 NormalY=0 NormalZ=1 AngleXU=0 Radius=12.7 StartAngle=4.71239 EndAngle=6.28319
    g5-g11: Circle x7 (B-spline internal-alignment scaffolding for g12; pole/knot coordinates omitted)
    g12: BSplineCurve PolesCount=7 KnotsCount=5 Degree=3 IsPeriodic=0
    g13-g17: GeomPoint x5 (B-spline internal-alignment scaffolding for g12; pole/knot coordinates omitted)
    g18: ArcOfCircle CenterX=105 CenterY=19 CenterZ=0 NormalX=0 NormalY=0 NormalZ=1 AngleXU=0 Radius=15.7 StartAngle=5.81226 EndAngle=6.28319
    g19: LineSegment StartX=117.7 StartY=19 StartZ=0 EndX=120.7 EndY=19 EndZ=0
    g20: BSplineCurve PolesCount=5 KnotsCount=3 Degree=3 IsPeriodic=0
    g21: LineSegment StartX=8.29999 StartY=3 StartZ=0 EndX=101.7 EndY=3 EndZ=0
    g22: LineSegment StartX=3.29999 StartY=-6.03275e-07 StartZ=0 EndX=105 EndY=-6.03275e-07 EndZ=0
    g23: LineSegment StartX=120.974 StartY=8.71251 StartZ=0 EndX=122.332 EndY=7.83778 EndZ=0
    g24: LineSegment StartX=105 StartY=-6.03274e-07 StartZ=0 EndX=113 EndY=-6.03274e-07 EndZ=0
    g25: ArcOfCircle CenterX=105 CenterY=19 CenterZ=0 NormalX=0 NormalY=0 NormalZ=1 AngleXU=0 Radius=20.6155 StartAngle=5.11091 EndAngle=5.71103
  constraints (38):
    c: Horizontal(g0)
    c: Distance(g0) = 3
    c: Coincident(g1,g0)
    c: Vertical(g1)
    c: Block(g2)
    c: Block(g0)
    c: Coincident(g3,g0)
    c: Coincident(g3,g2)
    c: Vertical(g3)
    c: Block(g1)
    c: Block(g4)
    c: Coincident(g20,g4)
    c: Block(g20)
    c: Equal(g5, g6-g11) x6
    c: InternalAlignment(g5-g11 -> g12) x7
    c: InternalAlignment(g13-g17 -> g12) x5
    c: Block(g12)
    c: Coincident(g18,g12)
    c: Coincident(g19,g4)
    c: Coincident(g19,g18)
    c: Horizontal(g19)
    c: Block(g19)
    c: Block(g18)
    c: Coincident(g21,g2)
    c: Coincident(g21,g20)
    c: Horizontal(g21)
    c: Distance(g21) = 93.4
    c: Coincident(g22,g1)
    c: Horizontal(g22)
    c: Distance(g22) = 101.7
    c: Horizontal(g24)
    c: Distance(g24) = 8
    c: Coincident(g25,g24)
    c: Block(g24)
    c: Coincident(g23,g25)
    c: Block(g25)
    c: Block(g23)
    c: Distance(g23) = 1.61553
FEATURE [Part::Extrusion] Extrude043  label="bottom010"
  Base = -> Sketch052
  Dir = (0,0,1)
  DirMode = 2
  FaceMakerClass = Part::FaceMakerBullseye
  LengthFwd = 71.4
  LengthRev = 0
  Placement = pos=(0,0,0.3) rot=(0,0,1;0rad)
  Solid = true
  Symmetric = false
FEATURE [Sketcher::SketchObject] Sketch053  label="topSketch013"
  FullyConstrained = true
  sketch-geometry (22):
    g0: LineSegment StartX=5.21097e-06 StartY=3 StartZ=0 EndX=5.21097e-06 EndY=19 EndZ=0
    g1: ArcOfCircle CenterX=19 CenterY=19 CenterZ=0 NormalX=0 NormalY=0 NormalZ=1 AngleXU=0 Radius=19 StartAngle=1.5708 EndAngle=3.14159
    g2: ArcOfCircle CenterX=19 CenterY=19 CenterZ=0 NormalX=0 NormalY=0 NormalZ=1 AngleXU=0 Radius=16 StartAngle=1.5708 EndAngle=3.14159
    g3: LineSegment StartX=114 StartY=35 StartZ=0 EndX=19 EndY=35 EndZ=0
    g4: LineSegment StartX=5.21097e-06 StartY=3 StartZ=0 EndX=5.21097e-06 EndY=0 EndZ=0
    g5: LineSegment StartX=3 StartY=0 StartZ=0 EndX=5.21097e-06 EndY=0 EndZ=0
    g6: LineSegment StartX=3 StartY=19 StartZ=0 EndX=3 EndY=0 EndZ=0
    g7: LineSegment StartX=19 StartY=38 StartZ=0 EndX=124 EndY=38 EndZ=0
    g8: Circle CenterX=119 CenterY=35 CenterZ=0 NormalX=0 NormalY=0 NormalZ=1 AngleXU=0 Radius=1
    g9: Circle CenterX=121 CenterY=35 CenterZ=0 NormalX=0 NormalY=0 NormalZ=1 AngleXU=0 Radius=1
    g10: Circle CenterX=121 CenterY=33 CenterZ=0 NormalX=0 NormalY=0 NormalZ=1 AngleXU=0 Radius=1
    g11: BSplineCurve PolesCount=3 KnotsCount=2 Degree=2 IsPeriodic=0
    g12: GeomPoint X=119 Y=35 Z=0
    g13: GeomPoint X=121 Y=33 Z=0
    g14: LineSegment StartX=119 StartY=35 StartZ=0 EndX=114 EndY=35 EndZ=0
    g15: ArcOfCircle CenterX=105 CenterY=19 CenterZ=0 NormalX=0 NormalY=0 NormalZ=1 AngleXU=0 Radius=16 StartAngle=5.60905 EndAngle=6.28319
    g16: LineSegment StartX=121 StartY=33 StartZ=0 EndX=121 EndY=19 EndZ=0
    g17: LineSegment StartX=117.5 StartY=9.01251 StartZ=0 EndX=121.163 EndY=9.0125 EndZ=0
    g18: ArcOfCircle CenterX=105 CenterY=19 CenterZ=0 NormalX=0 NormalY=0 NormalZ=1 AngleXU=0 Radius=20.6155 StartAngle=5.7297 EndAngle=6.28319
    g19: LineSegment StartX=121.163 StartY=9.0125 StartZ=0 EndX=122.538 EndY=8.16329 EndZ=0
    g20: LineSegment StartX=124 StartY=38 StartZ=0 EndX=125.616 EndY=38 EndZ=0
    g21: LineSegment StartX=125.616 StartY=19 StartZ=0 EndX=125.616 EndY=38 EndZ=0
  constraints (49):
    c: Vertical(g0)
    c: Block(g0)
    c: Coincident(g1,g0)
    c: Block(g1)
    c: Coincident(g2,g1)
    c: Block(g2)
    c: Coincident(g3,g2)
    c: Horizontal(g3)
    c: Tangent(g3,g2)
    c: Coincident(g4,g0)
    c: Distance(g4) = 3
    c: Vertical(g4)
    c: Coincident(g5,g4)
    c: Horizontal(g5)
    c: Coincident(g6,g2)
    c: Coincident(g6,g5)
    c: Vertical(g6)
    c: Horizontal(g7)
    c: Distance(g7) = 105
    c: Coincident(g7,g1)
    c: Block(g3)
    c: Weight(g8) = 1
    c: Equal(g8,g9)
    c: Equal(g8,g10)
    c: InternalAlignment(g8,g11)
    c: InternalAlignment(g9,g11)
    c: InternalAlignment(g10,g11)
    c: InternalAlignment(g12,g11)
    c: InternalAlignment(g13,g11)
    c: Block(g11)
    c: Coincident(g14,g11)
    c: Coincident(g14,g3)
    c: Horizontal(g14)
    c: Block(g15)
    c: Coincident(g16,g11)
    c: Coincident(g16,g15)
    c: Vertical(g16)
    c: Distance(g16) = 14
    c: Coincident(g17,g15)
    c: Block(g18)
    c: Coincident(g19,g18)
    c: Coincident(g20,g7)
    c: Horizontal(g20)
    c: Vertical(g21)
    c: Coincident(g20,g21)
    c: Block(g20)
    c: Block(g21)
    c: Block(g19)
    c: Block(g17)
FEATURE [Part::Extrusion] Extrude044
  Base = -> Sketch053
  Dir = (0,0,1)
  DirMode = 2
  FaceMakerClass = Part::FaceMakerBullseye
  LengthFwd = 72
  LengthRev = 0
  Solid = true
  Symmetric = false
FEATURE [Part::Fillet] Fillet036  label="top018"
  Base = -> Extrude044
  Edges = 1 edges r=2: [Edge41]
FEATURE [Part::Fillet] Fillet037  label="bottom011"
  Base = -> Extrude043
  Edges = 1 edges r=2.4: [Edge26]
FEATURE [Sketcher::SketchObject] Sketch054
  FullyConstrained = false
  Placement = pos=(0,0,0) rot=(1,0,0;1.5708rad)
  sketch-geometry (24):
    g0: ArcOfCircle CenterX=-4 CenterY=-10.5 CenterZ=0 NormalX=0 NormalY=0 NormalZ=1 AngleXU=0 Radius=1.5 StartAngle=6e-16 EndAngle=3.14159
    g1: ArcOfCircle CenterX=-34.2 CenterY=-10.5 CenterZ=0 NormalX=0 NormalY=0 NormalZ=1 AngleXU=0 Radius=1.5 StartAngle=0 EndAngle=3.14159
    g2: ArcOfCircle CenterX=-34.2 CenterY=-27.7 CenterZ=0 NormalX=0 NormalY=0 NormalZ=1 AngleXU=0 Radius=1.5 StartAngle=3.14159 EndAngle=6.28319
    g3: ArcOfCircle CenterX=-4 CenterY=-27.7 CenterZ=0 NormalX=0 NormalY=0 NormalZ=1 AngleXU=0 Radius=1.5 StartAngle=3.1416 EndAngle=6.28319
    g4: ArcOfCircle CenterX=-10 CenterY=-4.3 CenterZ=0 NormalX=0 NormalY=0 NormalZ=1 AngleXU=0 Radius=1.5 StartAngle=2e-16 EndAngle=3.14159
    g5: ArcOfCircle CenterX=-16.1 CenterY=-1.8 CenterZ=0 NormalX=0 NormalY=0 NormalZ=1 AngleXU=0 Radius=1.5 StartAngle=5e-16 EndAngle=3.14159
    g6: ArcOfCircle CenterX=-22.1 CenterY=-1.8 CenterZ=0 NormalX=0 NormalY=0 NormalZ=1 AngleXU=0 Radius=1.5 StartAngle=5e-16 EndAngle=3.14159
    g7: ArcOfCircle CenterX=-28.2 CenterY=-4.3 CenterZ=0 NormalX=0 NormalY=0 NormalZ=1 AngleXU=0 Radius=1.5 StartAngle=2e-16 EndAngle=3.14159
    g8: ArcOfCircle CenterX=-10 CenterY=-33.9 CenterZ=0 NormalX=0 NormalY=0 NormalZ=1 AngleXU=0 Radius=1.5 StartAngle=3.14159 EndAngle=6.28319
    g9: ArcOfCircle CenterX=-16.1 CenterY=-36.4 CenterZ=0 NormalX=0 NormalY=0 NormalZ=1 AngleXU=0 Radius=1.5 StartAngle=3.14159 EndAngle=6.28319
    g10: ArcOfCircle CenterX=-22.1 CenterY=-36.4 CenterZ=0 NormalX=0 NormalY=0 NormalZ=1 AngleXU=0 Radius=1.5 StartAngle=3.14159 EndAngle=6.28319
    g11: ArcOfCircle CenterX=-28.2 CenterY=-33.9 CenterZ=0 NormalX=0 NormalY=0 NormalZ=1 AngleXU=0 Radius=1.5 StartAngle=3.14159 EndAngle=6.28319
    g12: LineSegment StartX=-35.7 StartY=-10.5 StartZ=0 EndX=-35.7 EndY=-27.7 EndZ=0
    g13: LineSegment StartX=-32.7 StartY=-10.5 StartZ=0 EndX=-32.7 EndY=-27.7 EndZ=0
    g14: LineSegment StartX=-29.7 StartY=-33.9 StartZ=0 EndX=-29.7 EndY=-4.3 EndZ=0
    g15: LineSegment StartX=-26.7 StartY=-33.9 StartZ=0 EndX=-26.7 EndY=-4.3 EndZ=0
    g16: LineSegment StartX=-2.5 StartY=-10.5 StartZ=0 EndX=-2.5 EndY=-27.7 EndZ=0
    g17: LineSegment StartX=-8.5 StartY=-4.3 StartZ=0 EndX=-8.5 EndY=-33.9 EndZ=0
    g18: LineSegment StartX=-5.5 StartY=-10.5 StartZ=0 EndX=-5.5 EndY=-27.7 EndZ=0
    g19: LineSegment StartX=-11.5 StartY=-4.3 StartZ=0 EndX=-11.5 EndY=-33.9 EndZ=0
    g20: LineSegment StartX=-14.6 StartY=-1.8 StartZ=0 EndX=-14.6 EndY=-36.4 EndZ=0
    g21: LineSegment StartX=-17.6 StartY=-1.8 StartZ=0 EndX=-17.6 EndY=-36.4 EndZ=0
    g22: LineSegment StartX=-20.6 StartY=-36.4 StartZ=0 EndX=-20.6 EndY=-1.8 EndZ=0
    g23: LineSegment StartX=-23.6 StartY=-1.8 StartZ=0 EndX=-23.6 EndY=-36.4 EndZ=0
  constraints (48):
    c: Block(g0)
    c: Block(g1)
    c: Block(g2)
    c: Block(g3)
    c: Block(g4)
    c: Block(g5)
    c: Block(g6)
    c: Block(g7)
    c: Block(g8)
    c: Block(g9)
    c: Block(g10)
    c: Block(g11)
    c: Coincident(g12,g1)
    c: Coincident(g12,g2)
    c: Vertical(g12)
    c: Coincident(g13,g1)
    c: Coincident(g13,g2)
    c: Vertical(g13)
    c: Coincident(g14,g11)
    c: Coincident(g14,g7)
    c: Vertical(g14)
    c: Coincident(g15,g11)
    c: Coincident(g15,g7)
    c: Vertical(g15)
    c: Coincident(g16,g0)
    c: Coincident(g16,g3)
    c: Vertical(g16)
    c: Coincident(g17,g4)
    c: Coincident(g17,g8)
    c: Vertical(g17)
    c: Coincident(g18,g0)
    c: Coincident(g18,g3)
    c: Vertical(g18)
    c: Coincident(g19,g4)
    c: Coincident(g19,g8)
    c: Vertical(g19)
    c: Coincident(g20,g5)
    c: Coincident(g20,g9)
    c: Vertical(g20)
    c: Coincident(g21,g5)
    c: Coincident(g21,g9)
    c: Vertical(g21)
    c: Coincident(g22,g10)
    c: Coincident(g22,g6)
    c: Vertical(g22)
    c: Coincident(g23,g6)
    c: Coincident(g23,g10)
    c: Vertical(g23)
FEATURE [Part::Extrusion] Extrude045  label="removeToCreateFanGrillHoles003"
  Base = -> Sketch054
  Dir = (0,-1,6e-16)
  DirMode = 2
  FaceMakerClass = Part::FaceMakerBullseye
  LengthFwd = 10
  LengthRev = 0
  Placement = pos=(65.4,44,54.82) rot=(0,0,1;0rad)
  Solid = true
  Symmetric = false
FEATURE [Part::Feature] Face105 .. Face108  x4 (patterned run collapsed; names and placements below)
  shape: bbox 3.5 x 17.8 x 2e-07 mm, 1 faces, 0 solids (baked)
FEATURE [Part::Revolution] Revolve113  label="removeToCreateScrewAndThreadedInsertHole041"
  Angle = 360
  Axis = (0,1,0)
  Base = (0,0,0)
  FaceMakerClass = Part::FaceMakerBullseye
  Placement = pos=(62.3,30.3,19.7) rot=(0,0,1;0rad)
  Solid = false
  Source = -> Face105
  Symmetric = false
FEATURE [Part::Revolution] Revolve114  label="removeToCreateScrewAndThreadedInsertHole042"
  Angle = 360
  Axis = (0,1,0)
  Base = (0,0,0)
  FaceMakerClass = Part::FaceMakerBullseye
  Placement = pos=(62.3,30.3,51.7) rot=(0,0,1;0rad)
  Solid = false
  Source = -> Face106
  Symmetric = false
FEATURE [Part::Revolution] Revolve115  label="removeToCreateScrewAndThreadedInsertHole043"
  Angle = 360
  Axis = (0,1,0)
  Base = (0,0,0)
  FaceMakerClass = Part::FaceMakerBullseye
  Placement = pos=(30.3,30.3,19.7) rot=(0,0,1;0rad)
  Solid = false
  Source = -> Face107
  Symmetric = false
FEATURE [Part::Revolution] Revolve116  label="removeToCreateScrewAndThreadedInsertHole044"
  Angle = 360
  Axis = (0,1,0)
  Base = (0,0,0)
  FaceMakerClass = Part::FaceMakerBullseye
  Placement = pos=(30.3,30.3,51.7) rot=(0,0,1;0rad)
  Solid = false
  Source = -> Face108
  Symmetric = false
FEATURE [Part::MultiFuse] Fusion083  label="createThreadedInsertHolesForFan004"
  Shapes = -> [Revolve113,Revolve114,Revolve115,Revolve116]
FEATURE [Part::Box] Box024  label="removeToCreteHoleForPlugHousing026"
  AttacherType = Attacher::AttachEngine3D
  Height = 28.6
  Length = 10
  Placement = pos=(-2,0,21.7) rot=(0,0,1;0rad)
  Width = 19
FEATURE [Part::Cylinder] Cylinder038  label="removeToCreteHoleForPlugHousing027"
  Angle = 360
  AttacherType = Attacher::AttachEngine3D
  Height = 20
  Placement = pos=(-2,19,36) rot=(0,1,0;1.5708rad)
  Radius = 14.3
FEATURE [Part::MultiFuse] Fusion084  label="removeToCreteHoleForPlugHousing028"
  Shapes = -> [Box024,Cylinder038]
FEATURE [Part::Cylinder] Cylinder039
  Angle = 360
  AttacherType = Attacher::AttachEngine3D
  Height = 20
  Placement = pos=(0,0,36.15) rot=(0,0,1;0rad)
  Radius = 14.3
FEATURE [Part::Cylinder] Cylinder040
  Angle = 360
  AttacherType = Attacher::AttachEngine3D
  Height = 10
  Placement = pos=(0,0,36.15) rot=(0,0,1;0rad)
  Radius = 4
FEATURE [Part::Box] Box025  label="removeToCreteHoleForPlugHousing030"
  AttacherType = Attacher::AttachEngine3D
  Height = 28.6
  Length = 20
  Placement = pos=(106.15,0,21.7) rot=(0,0,1;0rad)
  Width = 19
FEATURE [Part::MultiFuse] Fusion086  label="removeToCreteHoleForPlugHousing031"
  Placement = pos=(70,19,36) rot=(0,1,0;1.5708rad)
  Shapes = -> [Cylinder039,Cylinder040]
FEATURE [Part::MultiFuse] Fusion085  label="removeToCreteHoleForPlugHousing029"
  Shapes = -> [Box025,Fusion086]
FEATURE [Sketcher::SketchObject] Sketch055
  FullyConstrained = true
  Placement = pos=(117,19,0) rot=(0.57735,0.57735,0.57735;2.0944rad)
  sketch-geometry (48):
    g0: LineSegment StartX=-49.19 StartY=69.25 StartZ=0 EndX=-49.19 EndY=66.25 EndZ=0
    g1: LineSegment StartX=-49.19 StartY=63.5 StartZ=0 EndX=-49.19 EndY=60.5 EndZ=0
    g2: LineSegment StartX=-49.19 StartY=57.75 StartZ=0 EndX=-49.19 EndY=54.75 EndZ=0
    g3: LineSegment StartX=-49.19 StartY=52 StartZ=0 EndX=-49.19 EndY=49 EndZ=0
    g4: LineSegment StartX=-49.19 StartY=46.25 StartZ=0 EndX=-49.19 EndY=43.25 EndZ=0
    g5: LineSegment StartX=-49.19 StartY=40.5 StartZ=0 EndX=-49.19 EndY=37.5 EndZ=0
    g6: LineSegment StartX=-49.19 StartY=34.5 StartZ=0 EndX=-49.19 EndY=31.5 EndZ=0
    g7: LineSegment StartX=-49.19 StartY=28.75 StartZ=0 EndX=-49.19 EndY=25.75 EndZ=0
    g8: LineSegment StartX=-49.19 StartY=23 StartZ=0 EndX=-49.19 EndY=20 EndZ=0
    g9: LineSegment StartX=-49.19 StartY=17.25 StartZ=0 EndX=-49.19 EndY=14.25 EndZ=0
    g10: LineSegment StartX=-49.19 StartY=11.5 StartZ=0 EndX=-49.19 EndY=8.5 EndZ=0
    g11: LineSegment StartX=-49.19 StartY=5.75 StartZ=0 EndX=-49.19 EndY=2.75 EndZ=0
    g12: ArcOfCircle CenterX=-1.5 CenterY=67.75 CenterZ=0 NormalX=0 NormalY=0 NormalZ=1 AngleXU=0 Radius=1.5 StartAngle=4.71239 EndAngle=7.85398
    g13: ArcOfCircle CenterX=-1.5 CenterY=62 CenterZ=0 NormalX=0 NormalY=0 NormalZ=1 AngleXU=0 Radius=1.5 StartAngle=4.71239 EndAngle=7.85398
    g14: ArcOfCircle CenterX=-1.5 CenterY=56.25 CenterZ=0 NormalX=0 NormalY=0 NormalZ=1 AngleXU=0 Radius=1.5 StartAngle=4.71239 EndAngle=7.85398
    g15: ArcOfCircle CenterX=-11.49 CenterY=50.5 CenterZ=0 NormalX=0 NormalY=0 NormalZ=1 AngleXU=0 Radius=1.5 StartAngle=4.71239 EndAngle=7.85398
    g16: ArcOfCircle CenterX=-16.28 CenterY=44.75 CenterZ=0 NormalX=0 NormalY=0 NormalZ=1 AngleXU=0 Radius=1.5 StartAngle=4.71239 EndAngle=7.85398
    g17: ArcOfCircle CenterX=-18.2337 CenterY=39 CenterZ=0 NormalX=0 NormalY=0 NormalZ=1 AngleXU=0 Radius=1.5 StartAngle=4.71485 EndAngle=7.85398
    g18: ArcOfCircle CenterX=-16.2837 CenterY=27.25 CenterZ=0 NormalX=0 NormalY=0 NormalZ=1 AngleXU=0 Radius=1.5 StartAngle=4.71485 EndAngle=7.85398
    g19: ArcOfCircle CenterX=-18.2337 CenterY=33 CenterZ=0 NormalX=0 NormalY=0 NormalZ=1 AngleXU=0 Radius=1.5 StartAngle=4.71485 EndAngle=7.85398
    g20: ArcOfCircle CenterX=-11.49 CenterY=21.5 CenterZ=0 NormalX=0 NormalY=0 NormalZ=1 AngleXU=0 Radius=1.5 StartAngle=4.71239 EndAngle=7.85398
    g21: ArcOfCircle CenterX=-1.5 CenterY=4.25 CenterZ=0 NormalX=0 NormalY=0 NormalZ=1 AngleXU=0 Radius=1.5 StartAngle=4.71239 EndAngle=7.85398
    g22: ArcOfCircle CenterX=-1.5 CenterY=10 CenterZ=0 NormalX=0 NormalY=0 NormalZ=1 AngleXU=0 Radius=1.5 StartAngle=4.71239 EndAngle=7.85398
    g23: ArcOfCircle CenterX=-1.5 CenterY=15.75 CenterZ=0 NormalX=0 NormalY=0 NormalZ=1 AngleXU=0 Radius=1.5 StartAngle=4.71239 EndAngle=7.85398
    g24: LineSegment StartX=-49.19 StartY=69.25 StartZ=0 EndX=-1.5 EndY=69.25 EndZ=0
    g25: LineSegment StartX=-49.19 StartY=66.25 StartZ=0 EndX=-1.5 EndY=66.25 EndZ=0
    g26: LineSegment StartX=-49.19 StartY=63.5 StartZ=0 EndX=-1.5 EndY=63.5 EndZ=0
    g27: LineSegment StartX=-49.19 StartY=60.5 StartZ=0 EndX=-1.5 EndY=60.5 EndZ=0
    g28: LineSegment StartX=-49.19 StartY=57.75 StartZ=0 EndX=-1.5 EndY=57.75 EndZ=0
    g29: LineSegment StartX=-49.19 StartY=54.75 StartZ=0 EndX=-1.5 EndY=54.75 EndZ=0
    g30: LineSegment StartX=-49.19 StartY=52 StartZ=0 EndX=-11.49 EndY=52 EndZ=0
    g31: LineSegment StartX=-49.19 StartY=49 StartZ=0 EndX=-11.49 EndY=49 EndZ=0
    g32: LineSegment StartX=-49.19 StartY=46.25 StartZ=0 EndX=-16.28 EndY=46.25 EndZ=0
    g33: LineSegment StartX=-49.19 StartY=43.25 StartZ=0 EndX=-16.28 EndY=43.25 EndZ=0
    g34: LineSegment StartX=-49.19 StartY=40.5 StartZ=0 EndX=-18.2337 EndY=40.5 EndZ=0
    g35: LineSegment StartX=-49.19 StartY=37.5 StartZ=0 EndX=-18.23 EndY=37.5 EndZ=0
    g36: LineSegment StartX=-49.19 StartY=34.5 StartZ=0 EndX=-18.2337 EndY=34.5 EndZ=0
    g37: LineSegment StartX=-49.19 StartY=31.5 StartZ=0 EndX=-18.23 EndY=31.5 EndZ=0
    g38: LineSegment StartX=-49.19 StartY=28.75 StartZ=0 EndX=-16.2837 EndY=28.75 EndZ=0
    g39: LineSegment StartX=-49.19 StartY=25.75 StartZ=0 EndX=-16.28 EndY=25.75 EndZ=0
    g40: LineSegment StartX=-49.19 StartY=23 StartZ=0 EndX=-11.49 EndY=23 EndZ=0
    g41: LineSegment StartX=-49.19 StartY=20 StartZ=0 EndX=-11.49 EndY=20 EndZ=0
    g42: LineSegment StartX=-49.19 StartY=17.25 StartZ=0 EndX=-1.5 EndY=17.25 EndZ=0
    g43: LineSegment StartX=-49.19 StartY=14.25 StartZ=0 EndX=-1.5 EndY=14.25 EndZ=0
    g44: LineSegment StartX=-49.19 StartY=11.5 StartZ=0 EndX=-1.5 EndY=11.5 EndZ=0
    g45: LineSegment StartX=-49.19 StartY=8.5 StartZ=0 EndX=-1.5 EndY=8.5 EndZ=0
    g46: LineSegment StartX=-49.19 StartY=5.75 StartZ=0 EndX=-1.5 EndY=5.75 EndZ=0
    g47: LineSegment StartX=-49.19 StartY=2.75 StartZ=0 EndX=-1.5 EndY=2.75 EndZ=0
  constraints (120):
    c: Vertical(g0)
    c: Distance(g0) = 3
    c: Block(g0)
    c: Vertical(g1)
    c: Distance(g1) = 3
    c: Vertical(g2)
    c: Equal(g0,g2) = 3
    c: Block(g2)
    c: Vertical(g3)
    c: Equal(g1,g3) = 3
    c: Vertical(g4)
    c: Equal(g0,g4) = 3
    c: Block(g4)
    c: Vertical(g5)
    c: Equal(g1,g5) = 3
    c: Vertical(g6)
    c: Equal(g0,g6) = 3
    c: Block(g6)
    c: Vertical(g7)
    c: Equal(g1,g7) = 3
    c: Vertical(g8)
    c: Equal(g0,g8) = 3
    c: Block(g8)
    c: Vertical(g9)
    c: Equal(g1,g9) = 3
    c: Vertical(g10)
    c: Equal(g0,g10) = 3
    c: Block(g10)
    c: Vertical(g11)
    c: Equal(g1,g11) = 3
    c: Block(g12)
    c: Block(g13)
    c: Block(g14)
    c: Block(g15)
    c: Block(g16)
    c: Block(g17)
    c: Block(g18)
    c: Block(g19)
    c: Block(g20)
    c: Block(g21)
    c: Block(g22)
    c: Block(g23)
    c: Block(g11)
    c: Block(g9)
    c: Block(g7)
    c: Block(g5)
    c: Block(g3)
    c: Block(g1)
    c: Coincident(g24,g0)
    c: Coincident(g24,g12)
    c: Horizontal(g24)
    c: Coincident(g25,g0)
    c: Coincident(g25,g12)
    c: Horizontal(g25)
    c: Coincident(g26,g1)
    c: Coincident(g26,g13)
    c: Horizontal(g26)
    c: Coincident(g27,g1)
    c: Coincident(g27,g13)
    c: Horizontal(g27)
    c: Coincident(g28,g2)
    c: Coincident(g28,g14)
    c: Horizontal(g28)
    c: Coincident(g29,g2)
    c: Coincident(g29,g14)
    c: Horizontal(g29)
    c: Coincident(g30,g3)
    c: Coincident(g30,g15)
    c: Horizontal(g30)
    c: Coincident(g31,g3)
    c: Coincident(g31,g15)
    c: Horizontal(g31)
    c: Coincident(g32,g4)
    c: Coincident(g32,g16)
    c: Horizontal(g32)
    c: Coincident(g33,g4)
    c: Coincident(g33,g16)
    c: Horizontal(g33)
    c: Coincident(g34,g5)
    c: Coincident(g34,g17)
    c: Horizontal(g34)
    c: Coincident(g35,g5)
    c: Coincident(g35,g17)
    c: Horizontal(g35)
    c: Coincident(g36,g6)
    c: Coincident(g36,g19)
    c: Horizontal(g36)
    c: Coincident(g37,g6)
    c: Coincident(g37,g19)
    c: Horizontal(g37)
    c: Coincident(g38,g7)
    c: Coincident(g38,g18)
    c: Horizontal(g38)
    c: Coincident(g39,g7)
    c: Coincident(g39,g18)
    c: Horizontal(g39)
    c: Coincident(g40,g8)
    c: Coincident(g40,g20)
    c: Horizontal(g40)
    c: Coincident(g41,g8)
    c: Coincident(g41,g20)
    c: Horizontal(g41)
    c: Coincident(g42,g9)
    c: Coincident(g42,g23)
    c: Horizontal(g42)
    c: Coincident(g43,g9)
    c: Coincident(g43,g23)
    c: Horizontal(g43)
    c: Coincident(g44,g10)
    c: Coincident(g44,g22)
    c: Horizontal(g44)
    c: Coincident(g45,g10)
    c: Coincident(g45,g22)
    c: Horizontal(g45)
    c: Coincident(g46,g11)
    c: Coincident(g46,g21)
    c: Horizontal(g46)
    c: Coincident(g47,g11)
    c: Coincident(g47,g21)
    c: Horizontal(g47)
FEATURE [Part::Extrusion] Extrude046
  Base = -> Sketch055
  Dir = (1,0,0)
  DirMode = 2
  FaceMakerClass = Part::FaceMakerBullseye
  LengthFwd = 23
  LengthRev = 0
  Placement = pos=(-19,0,0) rot=(0,0,1;0rad)
  Solid = true
  Symmetric = false
FEATURE [Part::Fillet] Fillet038  label="removeToCreateVentalationHoles001"
  Base = -> Extrude046
  Edges = <same value as first occurrence — deduplicated (x4 in doc)>
  Placement = pos=(7,0,0) rot=(0,0,1;0rad)
FEATURE [Sketcher::SketchObject] Sketch056  label="topSketch014"
  FullyConstrained = true
  sketch-geometry (22):
    g0: LineSegment StartX=5.21097e-06 StartY=3 StartZ=0 EndX=5.21097e-06 EndY=19 EndZ=0
    g1: ArcOfCircle CenterX=19 CenterY=19 CenterZ=0 NormalX=0 NormalY=0 NormalZ=1 AngleXU=0 Radius=19 StartAngle=1.5708 EndAngle=3.14159
    g2: ArcOfCircle CenterX=19 CenterY=19 CenterZ=0 NormalX=0 NormalY=0 NormalZ=1 AngleXU=0 Radius=16 StartAngle=1.5708 EndAngle=3.14159
    g3: LineSegment StartX=114 StartY=35 StartZ=0 EndX=19 EndY=35 EndZ=0
    g4: LineSegment StartX=5.21097e-06 StartY=3 StartZ=0 EndX=5.21097e-06 EndY=0 EndZ=0
    g5: LineSegment StartX=3 StartY=0 StartZ=0 EndX=5.21097e-06 EndY=0 EndZ=0
    g6: LineSegment StartX=3 StartY=19 StartZ=0 EndX=3 EndY=0 EndZ=0
    g7: LineSegment StartX=19 StartY=38 StartZ=0 EndX=124 EndY=38 EndZ=0
    g8: Circle CenterX=119 CenterY=35 CenterZ=0 NormalX=0 NormalY=0 NormalZ=1 AngleXU=0 Radius=1
    g9: Circle CenterX=121 CenterY=35 CenterZ=0 NormalX=0 NormalY=0 NormalZ=1 AngleXU=0 Radius=1
    g10: Circle CenterX=121 CenterY=33 CenterZ=0 NormalX=0 NormalY=0 NormalZ=1 AngleXU=0 Radius=1
    g11: BSplineCurve PolesCount=3 KnotsCount=2 Degree=2 IsPeriodic=0
    g12: GeomPoint X=119 Y=35 Z=0
    g13: GeomPoint X=121 Y=33 Z=0
    g14: LineSegment StartX=119 StartY=35 StartZ=0 EndX=114 EndY=35 EndZ=0
    g15: ArcOfCircle CenterX=105 CenterY=19 CenterZ=0 NormalX=0 NormalY=0 NormalZ=1 AngleXU=0 Radius=16 StartAngle=5.60905 EndAngle=6.28319
    g16: LineSegment StartX=121 StartY=33 StartZ=0 EndX=121 EndY=19 EndZ=0
    g17: LineSegment StartX=117.5 StartY=9.01251 StartZ=0 EndX=121.163 EndY=9.0125 EndZ=0
    g18: ArcOfCircle CenterX=105 CenterY=19 CenterZ=0 NormalX=0 NormalY=0 NormalZ=1 AngleXU=0 Radius=20.6155 StartAngle=5.7297 EndAngle=6.28319
    g19: LineSegment StartX=121.163 StartY=9.0125 StartZ=0 EndX=122.538 EndY=8.16329 EndZ=0
    g20: LineSegment StartX=124 StartY=38 StartZ=0 EndX=125.616 EndY=38 EndZ=0
    g21: LineSegment StartX=125.616 StartY=19 StartZ=0 EndX=125.616 EndY=38 EndZ=0
  constraints (49):
    c: Vertical(g0)
    c: Block(g0)
    c: Coincident(g1,g0)
    c: Block(g1)
    c: Coincident(g2,g1)
    c: Block(g2)
    c: Coincident(g3,g2)
    c: Horizontal(g3)
    c: Tangent(g3,g2)
    c: Coincident(g4,g0)
    c: Distance(g4) = 3
    c: Vertical(g4)
    c: Coincident(g5,g4)
    c: Horizontal(g5)
    c: Coincident(g6,g2)
    c: Coincident(g6,g5)
    c: Vertical(g6)
    c: Horizontal(g7)
    c: Distance(g7) = 105
    c: Coincident(g7,g1)
    c: Block(g3)
    c: Weight(g8) = 1
    c: Equal(g8,g9)
    c: Equal(g8,g10)
    c: InternalAlignment(g8,g11)
    c: InternalAlignment(g9,g11)
    c: InternalAlignment(g10,g11)
    c: InternalAlignment(g12,g11)
    c: InternalAlignment(g13,g11)
    c: Block(g11)
    c: Coincident(g14,g11)
    c: Coincident(g14,g3)
    c: Horizontal(g14)
    c: Block(g15)
    c: Coincident(g16,g11)
    c: Coincident(g16,g15)
    c: Vertical(g16)
    c: Distance(g16) = 14
    c: Coincident(g17,g15)
    c: Block(g18)
    c: Coincident(g19,g18)
    c: Coincident(g20,g7)
    c: Horizontal(g20)
    c: Vertical(g21)
    c: Coincident(g20,g21)
    c: Block(g20)
    c: Block(g21)
    c: Block(g19)
    c: Block(g17)
FEATURE [Part::Box] Box026  label="removeToCreteHoleForPlugHousing032"
  AttacherType = Attacher::AttachEngine3D
  Height = 28.6
  Length = 10
  Placement = pos=(-2,0,21.7) rot=(0,0,1;0rad)
  Width = 19
FEATURE [Part::Feature] Face109 .. Face112  x4 (patterned run collapsed; names and placements below)
  shape: bbox 3.5 x 17.8 x 2e-07 mm, 1 faces, 0 solids (baked)
FEATURE [Part::Revolution] Revolve117  label="removeToCreateScrewAndThreadedInsertHole045"
  Angle = 360
  Axis = (0,1,0)
  Base = (0,0,0)
  FaceMakerClass = Part::FaceMakerBullseye
  Placement = pos=(62.3,30.3,19.7) rot=(0,0,1;0rad)
  Solid = false
  Source = -> Face109
  Symmetric = false
FEATURE [Part::Revolution] Revolve118  label="removeToCreateScrewAndThreadedInsertHole046"
  Angle = 360
  Axis = (0,1,0)
  Base = (0,0,0)
  FaceMakerClass = Part::FaceMakerBullseye
  Placement = pos=(62.3,30.3,51.7) rot=(0,0,1;0rad)
  Solid = false
  Source = -> Face110
  Symmetric = false
FEATURE [Part::Revolution] Revolve119  label="removeToCreateScrewAndThreadedInsertHole047"
  Angle = 360
  Axis = (0,1,0)
  Base = (0,0,0)
  FaceMakerClass = Part::FaceMakerBullseye
  Placement = pos=(30.3,30.3,19.7) rot=(0,0,1;0rad)
  Solid = false
  Source = -> Face111
  Symmetric = false
FEATURE [Part::Revolution] Revolve120  label="removeToCreateScrewAndThreadedInsertHole048"
  Angle = 360
  Axis = (0,1,0)
  Base = (0,0,0)
  FaceMakerClass = Part::FaceMakerBullseye
  Placement = pos=(30.3,30.3,51.7) rot=(0,0,1;0rad)
  Solid = false
  Source = -> Face112
  Symmetric = false
FEATURE [Part::MultiFuse] Fusion087  label="createThreadedInsertHolesForFan005"
  Shapes = -> [Revolve117,Revolve118,Revolve119,Revolve120]
FEATURE [Part::Extrusion] Extrude047
  Base = -> Sketch056
  Dir = (0,0,1)
  DirMode = 2
  FaceMakerClass = Part::FaceMakerBullseye
  LengthFwd = 72
  LengthRev = 0
  Solid = true
  Symmetric = false
FEATURE [Part::Fillet] Fillet039  label="top019"
  Base = -> Extrude047
  Edges = 1 edges r=2: [Edge35]
FEATURE [Sketcher::SketchObject] Sketch057
  FullyConstrained = false
  Placement = pos=(0,0,0) rot=(1,0,0;1.5708rad)
  sketch-geometry (24):
    g0: ArcOfCircle CenterX=-4 CenterY=-10.5 CenterZ=0 NormalX=0 NormalY=0 NormalZ=1 AngleXU=0 Radius=1.5 StartAngle=6e-16 EndAngle=3.14159
    g1: ArcOfCircle CenterX=-34.2 CenterY=-10.5 CenterZ=0 NormalX=0 NormalY=0 NormalZ=1 AngleXU=0 Radius=1.5 StartAngle=0 EndAngle=3.14159
    g2: ArcOfCircle CenterX=-34.2 CenterY=-27.7 CenterZ=0 NormalX=0 NormalY=0 NormalZ=1 AngleXU=0 Radius=1.5 StartAngle=3.14159 EndAngle=6.28319
    g3: ArcOfCircle CenterX=-4 CenterY=-27.7 CenterZ=0 NormalX=0 NormalY=0 NormalZ=1 AngleXU=0 Radius=1.5 StartAngle=3.1416 EndAngle=6.28319
    g4: ArcOfCircle CenterX=-10 CenterY=-4.3 CenterZ=0 NormalX=0 NormalY=0 NormalZ=1 AngleXU=0 Radius=1.5 StartAngle=2e-16 EndAngle=3.14159
    g5: ArcOfCircle CenterX=-16.1 CenterY=-1.8 CenterZ=0 NormalX=0 NormalY=0 NormalZ=1 AngleXU=0 Radius=1.5 StartAngle=5e-16 EndAngle=3.14159
    g6: ArcOfCircle CenterX=-22.1 CenterY=-1.8 CenterZ=0 NormalX=0 NormalY=0 NormalZ=1 AngleXU=0 Radius=1.5 StartAngle=5e-16 EndAngle=3.14159
    g7: ArcOfCircle CenterX=-28.2 CenterY=-4.3 CenterZ=0 NormalX=0 NormalY=0 NormalZ=1 AngleXU=0 Radius=1.5 StartAngle=2e-16 EndAngle=3.14159
    g8: ArcOfCircle CenterX=-10 CenterY=-33.9 CenterZ=0 NormalX=0 NormalY=0 NormalZ=1 AngleXU=0 Radius=1.5 StartAngle=3.14159 EndAngle=6.28319
    g9: ArcOfCircle CenterX=-16.1 CenterY=-36.4 CenterZ=0 NormalX=0 NormalY=0 NormalZ=1 AngleXU=0 Radius=1.5 StartAngle=3.14159 EndAngle=6.28319
    g10: ArcOfCircle CenterX=-22.1 CenterY=-36.4 CenterZ=0 NormalX=0 NormalY=0 NormalZ=1 AngleXU=0 Radius=1.5 StartAngle=3.14159 EndAngle=6.28319
    g11: ArcOfCircle CenterX=-28.2 CenterY=-33.9 CenterZ=0 NormalX=0 NormalY=0 NormalZ=1 AngleXU=0 Radius=1.5 StartAngle=3.14159 EndAngle=6.28319
    g12: LineSegment StartX=-35.7 StartY=-10.5 StartZ=0 EndX=-35.7 EndY=-27.7 EndZ=0
    g13: LineSegment StartX=-32.7 StartY=-10.5 StartZ=0 EndX=-32.7 EndY=-27.7 EndZ=0
    g14: LineSegment StartX=-29.7 StartY=-33.9 StartZ=0 EndX=-29.7 EndY=-4.3 EndZ=0
    g15: LineSegment StartX=-26.7 StartY=-33.9 StartZ=0 EndX=-26.7 EndY=-4.3 EndZ=0
    g16: LineSegment StartX=-2.5 StartY=-10.5 StartZ=0 EndX=-2.5 EndY=-27.7 EndZ=0
    g17: LineSegment StartX=-8.5 StartY=-4.3 StartZ=0 EndX=-8.5 EndY=-33.9 EndZ=0
    g18: LineSegment StartX=-5.5 StartY=-10.5 StartZ=0 EndX=-5.5 EndY=-27.7 EndZ=0
    g19: LineSegment StartX=-11.5 StartY=-4.3 StartZ=0 EndX=-11.5 EndY=-33.9 EndZ=0
    g20: LineSegment StartX=-14.6 StartY=-1.8 StartZ=0 EndX=-14.6 EndY=-36.4 EndZ=0
    g21: LineSegment StartX=-17.6 StartY=-1.8 StartZ=0 EndX=-17.6 EndY=-36.4 EndZ=0
    g22: LineSegment StartX=-20.6 StartY=-36.4 StartZ=0 EndX=-20.6 EndY=-1.8 EndZ=0
    g23: LineSegment StartX=-23.6 StartY=-1.8 StartZ=0 EndX=-23.6 EndY=-36.4 EndZ=0
  constraints (48):
    c: Block(g0)
    c: Block(g1)
    c: Block(g2)
    c: Block(g3)
    c: Block(g4)
    c: Block(g5)
    c: Block(g6)
    c: Block(g7)
    c: Block(g8)
    c: Block(g9)
    c: Block(g10)
    c: Block(g11)
    c: Coincident(g12,g1)
    c: Coincident(g12,g2)
    c: Vertical(g12)
    c: Coincident(g13,g1)
    c: Coincident(g13,g2)
    c: Vertical(g13)
    c: Coincident(g14,g11)
    c: Coincident(g14,g7)
    c: Vertical(g14)
    c: Coincident(g15,g11)
    c: Coincident(g15,g7)
    c: Vertical(g15)
    c: Coincident(g16,g0)
    c: Coincident(g16,g3)
    c: Vertical(g16)
    c: Coincident(g17,g4)
    c: Coincident(g17,g8)
    c: Vertical(g17)
    c: Coincident(g18,g0)
    c: Coincident(g18,g3)
    c: Vertical(g18)
    c: Coincident(g19,g4)
    c: Coincident(g19,g8)
    c: Vertical(g19)
    c: Coincident(g20,g5)
    c: Coincident(g20,g9)
    c: Vertical(g20)
    c: Coincident(g21,g5)
    c: Coincident(g21,g9)
    c: Vertical(g21)
    c: Coincident(g22,g10)
    c: Coincident(g22,g6)
    c: Vertical(g22)
    c: Coincident(g23,g6)
    c: Coincident(g23,g10)
    c: Vertical(g23)
FEATURE [Part::Extrusion] Extrude048  label="removeToCreateFanGrillHoles004"
  Base = -> Sketch057
  Dir = (0,-1,6e-16)
  DirMode = 2
  FaceMakerClass = Part::FaceMakerBullseye
  LengthFwd = 10
  LengthRev = 0
  Placement = pos=(65.4,44,54.82) rot=(0,0,1;0rad)
  Solid = true
  Symmetric = false
FEATURE [Part::Cut] Cut040  label="top021"
  Base = -> Fillet039
  Tool = -> Extrude048
FEATURE [Part::Cylinder] Cylinder041  label="removeToCreteHoleForPlugHousing034"
  Angle = 360
  AttacherType = Attacher::AttachEngine3D
  Height = 20
  Placement = pos=(-2,19,36) rot=(0,1,0;1.5708rad)
  Radius = 14.3
FEATURE [Part::MultiFuse] Fusion089  label="removeToCreteHoleForPlugHousing035"
  Shapes = -> [Box026,Cylinder041]
FEATURE [Part::Cylinder] Cylinder042
  Angle = 360
  AttacherType = Attacher::AttachEngine3D
  Height = 20
  Placement = pos=(0,0,36.15) rot=(0,0,1;0rad)
  Radius = 14.3
FEATURE [Part::Cylinder] Cylinder043
  Angle = 360
  AttacherType = Attacher::AttachEngine3D
  Height = 10
  Placement = pos=(0,0,36.15) rot=(0,0,1;0rad)
  Radius = 4
FEATURE [Part::Box] Box027  label="removeToCreteHoleForPlugHousing036"
  AttacherType = Attacher::AttachEngine3D
  Height = 28.6
  Length = 20
  Placement = pos=(106.15,0,21.7) rot=(0,0,1;0rad)
  Width = 19
FEATURE [Part::Cut] Cut041  label="top022"
  Base = -> Cut040
  Tool = -> Fusion087
FEATURE [Part::Cut] Cut039  label="top020"
  Base = -> Cut041
  Tool = -> Fusion089
FEATURE [Part::MultiFuse] Fusion090  label="removeToCreteHoleForPlugHousing037"
  Placement = pos=(70,19,36) rot=(0,1,0;1.5708rad)
  Shapes = -> [Cylinder042,Cylinder043]
FEATURE [Part::MultiFuse] Fusion088  label="removeToCreteHoleForPlugHousing033"
  Shapes = -> [Box027,Fusion090]
FEATURE [Part::Cut] Cut042  label="removeToCreteHoleForPlugHousing038"
  Base = -> Cut039
  Tool = -> Fusion088
FEATURE [Part::MultiFuse] Fusion091  label="removeFromTop"
  Shapes = -> [Fillet038,Fusion085,Fusion084,Fusion083,Extrude045]
FEATURE [Part::Cut] Cut043  label="removeToCreteHoleForPlugHousing039"
  Base = -> Fillet036
  Tool = -> Fusion091
FEATURE [Part::MultiFuse] Fusion092  label="caseScrewPillarBracket016"
  Shapes = -> [Extrude030,Extrude031,Extrude032,Extrude033,Extrude034,Extrude035,Extrude036,Extrude037,Box013,Box014]
FEATURE [Part::MultiFuse] Fusion093  label="bottom012"
  Shapes = -> [Cut034,Fillet037]
FEATURE [Sketcher::SketchObject] Sketch058  label="topSketch015"
  FullyConstrained = true
  sketch-geometry (20):
    g0: LineSegment StartX=5.21097e-06 StartY=3 StartZ=0 EndX=5.21097e-06 EndY=19 EndZ=0
    g1: ArcOfCircle CenterX=19 CenterY=19 CenterZ=0 NormalX=0 NormalY=0 NormalZ=1 AngleXU=0 Radius=19 StartAngle=1.5708 EndAngle=3.14159
    g2: ArcOfCircle CenterX=19 CenterY=19 CenterZ=0 NormalX=0 NormalY=0 NormalZ=1 AngleXU=0 Radius=16 StartAngle=1.5708 EndAngle=3.14159
    g3: LineSegment StartX=114 StartY=35 StartZ=0 EndX=19 EndY=35 EndZ=0
    g4: LineSegment StartX=5.21097e-06 StartY=3 StartZ=0 EndX=5.21097e-06 EndY=0 EndZ=0
    g5: LineSegment StartX=3 StartY=0 StartZ=0 EndX=5.21097e-06 EndY=0 EndZ=0
    g6: LineSegment StartX=3 StartY=19 StartZ=0 EndX=3 EndY=0 EndZ=0
    g7: LineSegment StartX=19 StartY=38 StartZ=0 EndX=124 EndY=38 EndZ=0
    g8: Circle CenterX=119 CenterY=35 CenterZ=0 NormalX=0 NormalY=0 NormalZ=1 AngleXU=0 Radius=1
    g9: Circle CenterX=121 CenterY=35 CenterZ=0 NormalX=0 NormalY=0 NormalZ=1 AngleXU=0 Radius=1
    g10: Circle CenterX=121 CenterY=33 CenterZ=0 NormalX=0 NormalY=0 NormalZ=1 AngleXU=0 Radius=1
    g11: BSplineCurve PolesCount=3 KnotsCount=2 Degree=2 IsPeriodic=0
    g12: GeomPoint X=119 Y=35 Z=0
    g13: GeomPoint X=121 Y=33 Z=0
    g14: LineSegment StartX=119 StartY=35 StartZ=0 EndX=114 EndY=35 EndZ=0
    g15: ArcOfCircle CenterX=105 CenterY=19 CenterZ=0 NormalX=0 NormalY=0 NormalZ=1 AngleXU=0 Radius=19 StartAngle=5.7297 EndAngle=6.28319
    g16: ArcOfCircle CenterX=105 CenterY=19 CenterZ=0 NormalX=0 NormalY=0 NormalZ=1 AngleXU=0 Radius=16 StartAngle=5.60905 EndAngle=6.28319
    g17: LineSegment StartX=121 StartY=33 StartZ=0 EndX=121 EndY=19 EndZ=0
    g18: LineSegment StartX=124 StartY=38 StartZ=0 EndX=124 EndY=19 EndZ=0
    g19: LineSegment StartX=117.5 StartY=9.01251 StartZ=0 EndX=121.163 EndY=9.0125 EndZ=0
  constraints (46):
    c: Vertical(g0)
    c: Block(g0)
    c: Coincident(g1,g0)
    c: Block(g1)
    c: Coincident(g2,g1)
    c: Block(g2)
    c: Coincident(g3,g2)
    c: Horizontal(g3)
    c: Tangent(g3,g2)
    c: Coincident(g4,g0)
    c: Distance(g4) = 3
    c: Vertical(g4)
    c: Coincident(g5,g4)
    c: Horizontal(g5)
    c: Coincident(g6,g2)
    c: Coincident(g6,g5)
    c: Vertical(g6)
    c: Horizontal(g7)
    c: Distance(g7) = 105
    c: Coincident(g7,g1)
    c: Block(g3)
    c: Weight(g8) = 1
    c: Equal(g8,g9)
    c: Equal(g8,g10)
    c: InternalAlignment(g8,g11)
    c: InternalAlignment(g9,g11)
    c: InternalAlignment(g10,g11)
    c: InternalAlignment(g12,g11)
    c: InternalAlignment(g13,g11)
    c: Block(g11)
    c: Coincident(g14,g11)
    c: Coincident(g14,g3)
    c: Horizontal(g14)
    c: Block(g15)
    c: Coincident(g16,g15)
    c: Block(g16)
    c: Coincident(g17,g11)
    c: Coincident(g17,g16)
    c: Vertical(g17)
    c: Distance(g17) = 14
    c: Coincident(g18,g7)
    c: Coincident(g18,g15)
    c: Vertical(g18)
    c: Distance(g18) = 19
    c: Coincident(g19,g16)
    c: Coincident(g19,g15)
FEATURE [Part::Extrusion] Extrude049  label="top023"
  Base = -> Sketch058
  Dir = (0,0,1)
  DirMode = 2
  FaceMakerClass = Part::FaceMakerBullseye
  LengthFwd = 72
  LengthRev = 0
  Solid = true
  Symmetric = false
FEATURE [Sketcher::SketchObject] Sketch059
  FullyConstrained = true
  MapMode = 3
  Placement = pos=(0,0,0) rot=(1,0,0;1.5708rad)
  Support = -> [Extrude049]
  sketch-geometry (8):
    g0: Circle CenterX=80.351 CenterY=-67.6202 CenterZ=0 NormalX=0 NormalY=0 NormalZ=1 AngleXU=0 Radius=2
    g1: Circle CenterX=80.351 CenterY=-67.6202 CenterZ=0 NormalX=0 NormalY=0 NormalZ=1 AngleXU=0 Radius=3
    g2: Circle CenterX=80.351 CenterY=-4.92017 CenterZ=0 NormalX=0 NormalY=0 NormalZ=1 AngleXU=0 Radius=2
    g3: Circle CenterX=80.351 CenterY=-4.92017 CenterZ=0 NormalX=0 NormalY=0 NormalZ=1 AngleXU=0 Radius=3
    g4: Circle CenterX=23.851 CenterY=-4.92017 CenterZ=0 NormalX=0 NormalY=0 NormalZ=1 AngleXU=0 Radius=2
    g5: Circle CenterX=23.851 CenterY=-4.92017 CenterZ=0 NormalX=0 NormalY=0 NormalZ=1 AngleXU=0 Radius=3
    g6: Circle CenterX=23.851 CenterY=-67.6202 CenterZ=0 NormalX=0 NormalY=0 NormalZ=1 AngleXU=0 Radius=2
    g7: Circle CenterX=23.851 CenterY=-67.6202 CenterZ=0 NormalX=0 NormalY=0 NormalZ=1 AngleXU=0 Radius=3
  constraints (8):
    c: Block(g3)
    c: Block(g2)
    c: Block(g1)
    c: Block(g0)
    c: Block(g6)
    c: Block(g7)
    c: Block(g4)
    c: Block(g5)
FEATURE [Sketcher::SketchObject] Sketch060
  FullyConstrained = true
  MapMode = 3
  Placement = pos=(0,0,0) rot=(1,0,0;1.5708rad)
  Support = -> [Extrude049]
  sketch-geometry (8):
    g0: Circle CenterX=80.351 CenterY=-67.6202 CenterZ=0 NormalX=0 NormalY=0 NormalZ=1 AngleXU=0 Radius=3
    g1: Circle CenterX=80.351 CenterY=-4.92017 CenterZ=0 NormalX=0 NormalY=0 NormalZ=1 AngleXU=0 Radius=3
    g2: Circle CenterX=23.851 CenterY=-4.92017 CenterZ=0 NormalX=0 NormalY=0 NormalZ=1 AngleXU=0 Radius=3
    g3: Circle CenterX=23.851 CenterY=-67.6202 CenterZ=0 NormalX=0 NormalY=0 NormalZ=1 AngleXU=0 Radius=3
    g4: Circle CenterX=23.851 CenterY=-67.6202 CenterZ=0 NormalX=0 NormalY=0 NormalZ=1 AngleXU=0 Radius=5
    g5: Circle CenterX=80.351 CenterY=-67.6202 CenterZ=0 NormalX=0 NormalY=0 NormalZ=1 AngleXU=0 Radius=5
    g6: Circle CenterX=23.851 CenterY=-4.92017 CenterZ=0 NormalX=0 NormalY=0 NormalZ=1 AngleXU=0 Radius=5
    g7: Circle CenterX=80.351 CenterY=-4.92017 CenterZ=0 NormalX=0 NormalY=0 NormalZ=1 AngleXU=0 Radius=5
  constraints (8):
    c: Block(g1)
    c: Block(g0)
    c: Block(g3)
    c: Block(g2)
    c: Block(g5)
    c: Block(g4)
    c: Block(g6)
    c: Block(g7)
FEATURE [Sketcher::SketchObject] Sketch061
  FullyConstrained = true
  MapMode = 3
  Placement = pos=(0,0,0) rot=(1,0,0;1.5708rad)
  sketch-geometry (8):
    g0: Circle CenterX=80.351 CenterY=-67.6202 CenterZ=0 NormalX=0 NormalY=0 NormalZ=1 AngleXU=0 Radius=3
    g1: Circle CenterX=80.351 CenterY=-4.92017 CenterZ=0 NormalX=0 NormalY=0 NormalZ=1 AngleXU=0 Radius=3
    g2: Circle CenterX=23.851 CenterY=-4.92017 CenterZ=0 NormalX=0 NormalY=0 NormalZ=1 AngleXU=0 Radius=3
    g3: Circle CenterX=23.851 CenterY=-67.6202 CenterZ=0 NormalX=0 NormalY=0 NormalZ=1 AngleXU=0 Radius=3
    g4: Circle CenterX=23.851 CenterY=-67.6202 CenterZ=0 NormalX=0 NormalY=0 NormalZ=1 AngleXU=0 Radius=5
    g5: Circle CenterX=80.351 CenterY=-67.6202 CenterZ=0 NormalX=0 NormalY=0 NormalZ=1 AngleXU=0 Radius=5
    g6: Circle CenterX=23.851 CenterY=-4.92017 CenterZ=0 NormalX=0 NormalY=0 NormalZ=1 AngleXU=0 Radius=5
    g7: Circle CenterX=80.351 CenterY=-4.92017 CenterZ=0 NormalX=0 NormalY=0 NormalZ=1 AngleXU=0 Radius=5
  constraints (8):
    c: Block(g1)
    c: Block(g0)
    c: Block(g3)
    c: Block(g2)
    c: Block(g5)
    c: Block(g4)
    c: Block(g6)
    c: Block(g7)
FEATURE [Sketcher::SketchObject] Sketch062  label="topSketch016"
  FullyConstrained = true
  sketch-geometry (20):
    g0: LineSegment StartX=5.21097e-06 StartY=3 StartZ=0 EndX=5.21097e-06 EndY=19 EndZ=0
    g1: ArcOfCircle CenterX=19 CenterY=19 CenterZ=0 NormalX=0 NormalY=0 NormalZ=1 AngleXU=0 Radius=19 StartAngle=1.5708 EndAngle=3.14159
    g2: ArcOfCircle CenterX=19 CenterY=19 CenterZ=0 NormalX=0 NormalY=0 NormalZ=1 AngleXU=0 Radius=16 StartAngle=1.5708 EndAngle=3.14159
    g3: LineSegment StartX=114 StartY=35 StartZ=0 EndX=19 EndY=35 EndZ=0
    g4: LineSegment StartX=5.21097e-06 StartY=3 StartZ=0 EndX=5.21097e-06 EndY=0 EndZ=0
    g5: LineSegment StartX=3 StartY=0 StartZ=0 EndX=5.21097e-06 EndY=0 EndZ=0
    g6: LineSegment StartX=3 StartY=19 StartZ=0 EndX=3 EndY=0 EndZ=0
    g7: LineSegment StartX=19 StartY=38 StartZ=0 EndX=124 EndY=38 EndZ=0
    g8: Circle CenterX=119 CenterY=35 CenterZ=0 NormalX=0 NormalY=0 NormalZ=1 AngleXU=0 Radius=1
    g9: Circle CenterX=121 CenterY=35 CenterZ=0 NormalX=0 NormalY=0 NormalZ=1 AngleXU=0 Radius=1
    g10: Circle CenterX=121 CenterY=33 CenterZ=0 NormalX=0 NormalY=0 NormalZ=1 AngleXU=0 Radius=1
    g11: BSplineCurve PolesCount=3 KnotsCount=2 Degree=2 IsPeriodic=0
    g12: GeomPoint X=119 Y=35 Z=0
    g13: GeomPoint X=121 Y=33 Z=0
    g14: LineSegment StartX=119 StartY=35 StartZ=0 EndX=114 EndY=35 EndZ=0
    g15: ArcOfCircle CenterX=105 CenterY=19 CenterZ=0 NormalX=0 NormalY=0 NormalZ=1 AngleXU=0 Radius=19 StartAngle=5.7297 EndAngle=6.28319
    g16: ArcOfCircle CenterX=105 CenterY=19 CenterZ=0 NormalX=0 NormalY=0 NormalZ=1 AngleXU=0 Radius=16 StartAngle=5.60905 EndAngle=6.28319
    g17: LineSegment StartX=121 StartY=33 StartZ=0 EndX=121 EndY=19 EndZ=0
    g18: LineSegment StartX=124 StartY=38 StartZ=0 EndX=124 EndY=19 EndZ=0
    g19: LineSegment StartX=117.5 StartY=9.01251 StartZ=0 EndX=121.163 EndY=9.0125 EndZ=0
  constraints (46):
    c: Vertical(g0)
    c: Block(g0)
    c: Coincident(g1,g0)
    c: Block(g1)
    c: Coincident(g2,g1)
    c: Block(g2)
    c: Coincident(g3,g2)
    c: Horizontal(g3)
    c: Tangent(g3,g2)
    c: Coincident(g4,g0)
    c: Distance(g4) = 3
    c: Vertical(g4)
    c: Coincident(g5,g4)
    c: Horizontal(g5)
    c: Coincident(g6,g2)
    c: Coincident(g6,g5)
    c: Vertical(g6)
    c: Horizontal(g7)
    c: Distance(g7) = 105
    c: Coincident(g7,g1)
    c: Block(g3)
    c: Weight(g8) = 1
    c: Equal(g8,g9)
    c: Equal(g8,g10)
    c: InternalAlignment(g8,g11)
    c: InternalAlignment(g9,g11)
    c: InternalAlignment(g10,g11)
    c: InternalAlignment(g12,g11)
    c: InternalAlignment(g13,g11)
    c: Block(g11)
    c: Coincident(g14,g11)
    c: Coincident(g14,g3)
    c: Horizontal(g14)
    c: Block(g15)
    c: Coincident(g16,g15)
    c: Block(g16)
    c: Coincident(g17,g11)
    c: Coincident(g17,g16)
    c: Vertical(g17)
    c: Distance(g17) = 14
    c: Coincident(g18,g7)
    c: Coincident(g18,g15)
    c: Vertical(g18)
    c: Distance(g18) = 19
    c: Coincident(g19,g16)
    c: Coincident(g19,g15)
FEATURE [Part::Extrusion] Extrude053  label="top024"
  Base = -> Sketch062
  Dir = (0,0,1)
  DirMode = 2
  FaceMakerClass = Part::FaceMakerBullseye
  LengthFwd = 72
  LengthRev = 0
  Solid = true
  Symmetric = false
FEATURE [Sketcher::SketchObject] Sketch063
  FullyConstrained = true
  MapMode = 3
  Placement = pos=(0,0,0) rot=(1,0,0;1.5708rad)
  Support = -> [Extrude053]
  sketch-geometry (8):
    g0: Circle CenterX=80.351 CenterY=-67.6202 CenterZ=0 NormalX=0 NormalY=0 NormalZ=1 AngleXU=0 Radius=2
    g1: Circle CenterX=80.351 CenterY=-67.6202 CenterZ=0 NormalX=0 NormalY=0 NormalZ=1 AngleXU=0 Radius=3
    g2: Circle CenterX=80.351 CenterY=-4.92017 CenterZ=0 NormalX=0 NormalY=0 NormalZ=1 AngleXU=0 Radius=2
    g3: Circle CenterX=80.351 CenterY=-4.92017 CenterZ=0 NormalX=0 NormalY=0 NormalZ=1 AngleXU=0 Radius=3
    g4: Circle CenterX=23.851 CenterY=-4.92017 CenterZ=0 NormalX=0 NormalY=0 NormalZ=1 AngleXU=0 Radius=2
    g5: Circle CenterX=23.851 CenterY=-4.92017 CenterZ=0 NormalX=0 NormalY=0 NormalZ=1 AngleXU=0 Radius=3
    g6: Circle CenterX=23.851 CenterY=-67.6202 CenterZ=0 NormalX=0 NormalY=0 NormalZ=1 AngleXU=0 Radius=2
    g7: Circle CenterX=23.851 CenterY=-67.6202 CenterZ=0 NormalX=0 NormalY=0 NormalZ=1 AngleXU=0 Radius=3
  constraints (8):
    c: Block(g3)
    c: Block(g2)
    c: Block(g1)
    c: Block(g0)
    c: Block(g6)
    c: Block(g7)
    c: Block(g4)
    c: Block(g5)
FEATURE [Part::Extrusion] Extrude054
  Base = -> Sketch063
  Dir = (0,-1,2e-16)
  DirMode = 2
  FaceMakerClass = Part::FaceMakerBullseye
  LengthFwd = 6
  LengthRev = 0
  Placement = pos=(0,9,0) rot=(0,0,1;0rad)
  Solid = true
  Symmetric = false
FEATURE [Sketcher::SketchObject] Sketch064  label="topSketch017"
  FullyConstrained = true
  sketch-geometry (20):
    g0: LineSegment StartX=5.21097e-06 StartY=3 StartZ=0 EndX=5.21097e-06 EndY=19 EndZ=0
    g1: ArcOfCircle CenterX=19 CenterY=19 CenterZ=0 NormalX=0 NormalY=0 NormalZ=1 AngleXU=0 Radius=19 StartAngle=1.5708 EndAngle=3.14159
    g2: ArcOfCircle CenterX=19 CenterY=19 CenterZ=0 NormalX=0 NormalY=0 NormalZ=1 AngleXU=0 Radius=16 StartAngle=1.5708 EndAngle=3.14159
    g3: LineSegment StartX=114 StartY=35 StartZ=0 EndX=19 EndY=35 EndZ=0
    g4: LineSegment StartX=5.21097e-06 StartY=3 StartZ=0 EndX=5.21097e-06 EndY=0 EndZ=0
    g5: LineSegment StartX=3 StartY=0 StartZ=0 EndX=5.21097e-06 EndY=0 EndZ=0
    g6: LineSegment StartX=3 StartY=19 StartZ=0 EndX=3 EndY=0 EndZ=0
    g7: LineSegment StartX=19 StartY=38 StartZ=0 EndX=124 EndY=38 EndZ=0
    g8: Circle CenterX=119 CenterY=35 CenterZ=0 NormalX=0 NormalY=0 NormalZ=1 AngleXU=0 Radius=1
    g9: Circle CenterX=121 CenterY=35 CenterZ=0 NormalX=0 NormalY=0 NormalZ=1 AngleXU=0 Radius=1
    g10: Circle CenterX=121 CenterY=33 CenterZ=0 NormalX=0 NormalY=0 NormalZ=1 AngleXU=0 Radius=1
    g11: BSplineCurve PolesCount=3 KnotsCount=2 Degree=2 IsPeriodic=0
    g12: GeomPoint X=119 Y=35 Z=0
    g13: GeomPoint X=121 Y=33 Z=0
    g14: LineSegment StartX=119 StartY=35 StartZ=0 EndX=114 EndY=35 EndZ=0
    g15: ArcOfCircle CenterX=105 CenterY=19 CenterZ=0 NormalX=0 NormalY=0 NormalZ=1 AngleXU=0 Radius=19 StartAngle=5.7297 EndAngle=6.28319
    g16: ArcOfCircle CenterX=105 CenterY=19 CenterZ=0 NormalX=0 NormalY=0 NormalZ=1 AngleXU=0 Radius=16 StartAngle=5.60905 EndAngle=6.28319
    g17: LineSegment StartX=121 StartY=33 StartZ=0 EndX=121 EndY=19 EndZ=0
    g18: LineSegment StartX=124 StartY=38 StartZ=0 EndX=124 EndY=19 EndZ=0
    g19: LineSegment StartX=117.5 StartY=9.01251 StartZ=0 EndX=121.163 EndY=9.0125 EndZ=0
  constraints (46):
    c: Vertical(g0)
    c: Block(g0)
    c: Coincident(g1,g0)
    c: Block(g1)
    c: Coincident(g2,g1)
    c: Block(g2)
    c: Coincident(g3,g2)
    c: Horizontal(g3)
    c: Tangent(g3,g2)
    c: Coincident(g4,g0)
    c: Distance(g4) = 3
    c: Vertical(g4)
    c: Coincident(g5,g4)
    c: Horizontal(g5)
    c: Coincident(g6,g2)
    c: Coincident(g6,g5)
    c: Vertical(g6)
    c: Horizontal(g7)
    c: Distance(g7) = 105
    c: Coincident(g7,g1)
    c: Block(g3)
    c: Weight(g8) = 1
    c: Equal(g8,g9)
    c: Equal(g8,g10)
    c: InternalAlignment(g8,g11)
    c: InternalAlignment(g9,g11)
    c: InternalAlignment(g10,g11)
    c: InternalAlignment(g12,g11)
    c: InternalAlignment(g13,g11)
    c: Block(g11)
    c: Coincident(g14,g11)
    c: Coincident(g14,g3)
    c: Horizontal(g14)
    c: Block(g15)
    c: Coincident(g16,g15)
    c: Block(g16)
    c: Coincident(g17,g11)
    c: Coincident(g17,g16)
    c: Vertical(g17)
    c: Distance(g17) = 14
    c: Coincident(g18,g7)
    c: Coincident(g18,g15)
    c: Vertical(g18)
    c: Distance(g18) = 19
    c: Coincident(g19,g16)
    c: Coincident(g19,g15)
FEATURE [Sketcher::SketchObject] Sketch065
  FullyConstrained = true
  MapMode = 3
  Placement = pos=(0,0,0) rot=(1,0,0;1.5708rad)
  sketch-geometry (8):
    g0: Circle CenterX=80.351 CenterY=-67.6202 CenterZ=0 NormalX=0 NormalY=0 NormalZ=1 AngleXU=0 Radius=3
    g1: Circle CenterX=80.351 CenterY=-4.92017 CenterZ=0 NormalX=0 NormalY=0 NormalZ=1 AngleXU=0 Radius=3
    g2: Circle CenterX=23.851 CenterY=-4.92017 CenterZ=0 NormalX=0 NormalY=0 NormalZ=1 AngleXU=0 Radius=3
    g3: Circle CenterX=23.851 CenterY=-67.6202 CenterZ=0 NormalX=0 NormalY=0 NormalZ=1 AngleXU=0 Radius=3
    g4: Circle CenterX=23.851 CenterY=-67.6202 CenterZ=0 NormalX=0 NormalY=0 NormalZ=1 AngleXU=0 Radius=5
    g5: Circle CenterX=80.351 CenterY=-67.6202 CenterZ=0 NormalX=0 NormalY=0 NormalZ=1 AngleXU=0 Radius=5
    g6: Circle CenterX=23.851 CenterY=-4.92017 CenterZ=0 NormalX=0 NormalY=0 NormalZ=1 AngleXU=0 Radius=5
    g7: Circle CenterX=80.351 CenterY=-4.92017 CenterZ=0 NormalX=0 NormalY=0 NormalZ=1 AngleXU=0 Radius=5
  constraints (8):
    c: Block(g1)
    c: Block(g0)
    c: Block(g3)
    c: Block(g2)
    c: Block(g5)
    c: Block(g4)
    c: Block(g6)
    c: Block(g7)
FEATURE [Part::Extrusion] Extrude056
  Base = -> Sketch065
  Dir = (0,-1,2e-16)
  DirMode = 2
  FaceMakerClass = Part::FaceMakerBullseye
  LengthFwd = 2
  LengthRev = 0
  Solid = true
  Symmetric = false
FEATURE [Part::Extrusion] Extrude057  label="top025"
  Base = -> Sketch064
  Dir = (0,0,1)
  DirMode = 2
  FaceMakerClass = Part::FaceMakerBullseye
  LengthFwd = 72
  LengthRev = 0
  Solid = true
  Symmetric = false
FEATURE [Sketcher::SketchObject] Sketch066
  FullyConstrained = true
  MapMode = 3
  Placement = pos=(0,0,0) rot=(1,0,0;1.5708rad)
  Support = -> [Extrude057]
  sketch-geometry (8):
    g0: Circle CenterX=80.351 CenterY=-67.6202 CenterZ=0 NormalX=0 NormalY=0 NormalZ=1 AngleXU=0 Radius=3
    g1: Circle CenterX=80.351 CenterY=-4.92017 CenterZ=0 NormalX=0 NormalY=0 NormalZ=1 AngleXU=0 Radius=3
    g2: Circle CenterX=23.851 CenterY=-4.92017 CenterZ=0 NormalX=0 NormalY=0 NormalZ=1 AngleXU=0 Radius=3
    g3: Circle CenterX=23.851 CenterY=-67.6202 CenterZ=0 NormalX=0 NormalY=0 NormalZ=1 AngleXU=0 Radius=3
    g4: Circle CenterX=23.851 CenterY=-67.6202 CenterZ=0 NormalX=0 NormalY=0 NormalZ=1 AngleXU=0 Radius=5
    g5: Circle CenterX=80.351 CenterY=-67.6202 CenterZ=0 NormalX=0 NormalY=0 NormalZ=1 AngleXU=0 Radius=5
    g6: Circle CenterX=23.851 CenterY=-4.92017 CenterZ=0 NormalX=0 NormalY=0 NormalZ=1 AngleXU=0 Radius=5
    g7: Circle CenterX=80.351 CenterY=-4.92017 CenterZ=0 NormalX=0 NormalY=0 NormalZ=1 AngleXU=0 Radius=5
  constraints (8):
    c: Block(g1)
    c: Block(g0)
    c: Block(g3)
    c: Block(g2)
    c: Block(g5)
    c: Block(g4)
    c: Block(g6)
    c: Block(g7)
FEATURE [Part::Extrusion] Extrude055
  Base = -> Sketch066
  Dir = (0,-1,2e-16)
  DirMode = 2
  FaceMakerClass = Part::FaceMakerBullseye
  LengthFwd = 2
  LengthRev = 0
  Solid = true
  Symmetric = false
FEATURE [Part::Fillet] Fillet041
  Base = -> Extrude056
  Edges = 4 edges r=1.99: [Edge6,Edge12,Edge18,Edge24]
FEATURE [Part::Cut] Cut045
  Base = -> Extrude055
  Placement = pos=(0,6,0) rot=(0,0,1;0rad)
  Tool = -> Fillet041
FEATURE [Part::MultiFuse] Fusion095
  Placement = pos=(-3.2,-1,72.3) rot=(0,0,1;0rad)
  Shapes = -> [Cut045,Extrude054]
